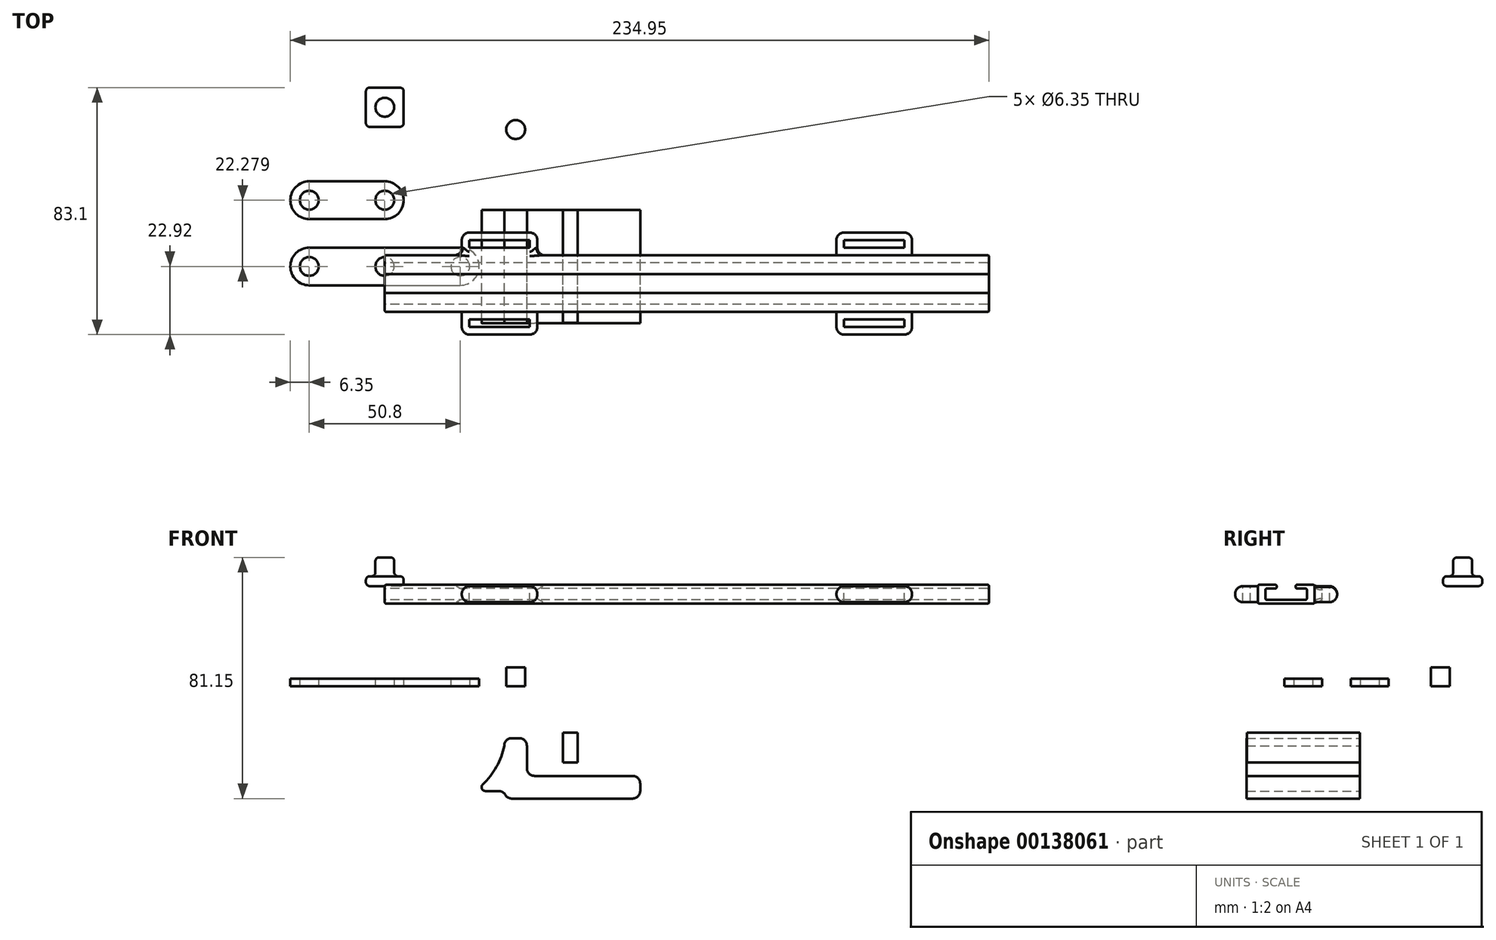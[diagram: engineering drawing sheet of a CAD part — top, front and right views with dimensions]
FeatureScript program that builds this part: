
annotation { "Feature Type Name" : "Feature", "Feature Type Description" : "" }
export const myFeature = defineFeature(function(context is Context, id is Id, definition is map)
    precondition{}
    {
        {
            var Q0;
            Q0=qCreatedBy(makeId("Top.planeOp"),FACE);
            var sketch = newSketch(context, id + "F0", { "sketchPlane" : qUnion([Q0])});
            skLineSegment(sketch, "E0.bottom", {"start": v(-25.4, 6.35) * mm, "end": v(25.4, 6.35) * mm});
            skLineSegment(sketch, "E0.top", {"start": v(-25.4, -6.35) * mm, "end": v(25.4, -6.35) * mm});
            skLineSegment(sketch, "E0.left", {"start": v(-25.4, 6.35) * mm, "end": v(-25.4, -6.35) * mm});
            skLineSegment(sketch, "E0.right", {"start": v(25.4, 6.35) * mm, "end": v(25.4, -6.35) * mm});
            skPoint(sketch, "E0.middle", {"position": v(0, 0) * mm});
            skLineSegment(sketch, "E1", {"start": v(-25.4, 0) * mm, "end": v(25.4, 0) * mm});
            skCircle(sketch, "E2", {"center": v(25.4, 0) * mm, "radius": 6.35 * mm});
            skCircle(sketch, "E3", {"center": v(25.4, 0) * mm, "radius": 3.18 * mm});
            skCircle(sketch, "E4", {"center": v(0, 0) * mm, "radius": 3.18 * mm});
            skCircle(sketch, "E5", {"center": v(-25.4, 0) * mm, "radius": 6.35 * mm});
            skCircle(sketch, "E6", {"center": v(-25.4, 0) * mm, "radius": 3.18 * mm});
            skSolve(sketch);
        }
        {
            var Q0;
            Q0 = qSketchRegion(id + "F0", true);
            extrude(context, id + "F1", {"entities" : qUnion([Q0]), "depth" : 2.54 * mm});
        }
        {
            var Q0;
            Q0=qCreatedBy(makeId("Right.planeOp"),FACE);
            var sketch = newSketch(context, id + "F2", { "sketchPlane" : qUnion([Q0])});
            skLineSegment(sketch, "E7", {"start": v(-8.95, 34.15) * mm, "end": v(-15.3, 34.15) * mm});
            skLineSegment(sketch, "E8", {"start": v(-15.3, 34.15) * mm, "end": v(-15.3, 27.8) * mm});
            skLineSegment(sketch, "E9", {"start": v(-15.3, 27.8) * mm, "end": v(3.75, 27.8) * mm});
            skLineSegment(sketch, "E10", {"start": v(3.75, 27.8) * mm, "end": v(3.75, 34.15) * mm});
            skLineSegment(sketch, "E11", {"start": v(3.75, 34.15) * mm, "end": v(-2.6, 34.15) * mm});
            skLineSegment(sketch, "E12", {"start": v(-8.95, 34.15) * mm, "end": v(-8.95, 32.88) * mm});
            skLineSegment(sketch, "E13", {"start": v(-8.95, 32.88) * mm, "end": v(-15.3, 32.88) * mm});
            skLineSegment(sketch, "E14", {"start": v(-15.3, 34.15) * mm, "end": v(-12.76, 34.15) * mm});
            skLineSegment(sketch, "E15", {"start": v(-12.76, 34.15) * mm, "end": v(-12.76, 27.8) * mm});
            skLineSegment(sketch, "E16", {"start": v(-12.76, 27.8) * mm, "end": v(-15.3, 27.8) * mm});
            skLineSegment(sketch, "E17", {"start": v(-15.3, 27.8) * mm, "end": v(-15.3, 29.07) * mm});
            skLineSegment(sketch, "E18", {"start": v(-15.3, 29.07) * mm, "end": v(3.75, 29.07) * mm});
            skLineSegment(sketch, "E19", {"start": v(3.75, 27.8) * mm, "end": v(1.21, 27.8) * mm});
            skLineSegment(sketch, "E20", {"start": v(1.21, 27.8) * mm, "end": v(1.21, 34.15) * mm});
            skLineSegment(sketch, "E21", {"start": v(1.21, 34.15) * mm, "end": v(3.75, 34.15) * mm});
            skLineSegment(sketch, "E22", {"start": v(3.75, 34.15) * mm, "end": v(3.75, 32.88) * mm});
            skLineSegment(sketch, "E23", {"start": v(3.75, 32.88) * mm, "end": v(-2.6, 32.88) * mm});
            skLineSegment(sketch, "E24", {"start": v(-2.6, 34.15) * mm, "end": v(-2.6, 32.88) * mm});
            skSolve(sketch);
        }
        {
            var Q0;
            {var subQ0=sQuery(id+"F2.wireOp",EDGE,"E21");Q0=makeQuery(id+"F2.imprint","IMPRINT",FACE,{"disambiguationData":[TD([[makeQuery(id+"F2.imprint","IMPRINT",EDGE,{"derivedFrom":subQ0}),-1.0]])]});}
            var Q1;
            {var subQ0=sQuery(id+"F2.wireOp",EDGE,"E16");Q1=makeQuery(id+"F2.imprint","IMPRINT",FACE,{"disambiguationData":[TD([[makeQuery(id+"F2.imprint","IMPRINT",EDGE,{"derivedFrom":subQ0}),-1.0]])]});}
            var Q2;
            {var subQ1=sQuery(id+"F2.wireOp",EDGE,"E10");var subQ3=sQuery(id+"F2.wireOp",EDGE,"E18");var subQ4=makeQuery(id+"F2.imprint","INTERSECT",VERTEX,{"derivedFrom":[subQ1,subQ3]});Q2=makeQuery(id+"F2.imprint","IMPRINT",FACE,{"disambiguationData":[TD([[makeQuery(id+"F2.imprint","IMPRINT",EDGE,{"disambiguationData":[TD([[subQ4,1.0]])],"derivedFrom":subQ3}),1.0]])]});}
            var Q3;
            {var subQ0=sQuery(id+"F2.wireOp",EDGE,"E19");Q3=makeQuery(id+"F2.imprint","IMPRINT",FACE,{"disambiguationData":[TD([[makeQuery(id+"F2.imprint","IMPRINT",EDGE,{"derivedFrom":subQ0}),-1.0]])]});}
            var Q4;
            {var subQ0=sQuery(id+"F2.wireOp",EDGE,"E9");Q4=makeQuery(id+"F2.imprint","IMPRINT",FACE,{"disambiguationData":[TD([[makeQuery(id+"F2.imprint","IMPRINT",EDGE,{"derivedFrom":subQ0}),1.0]])]});}
            var Q5;
            {var subQ1=sQuery(id+"F2.wireOp",EDGE,"E8");var subQ3=sQuery(id+"F2.wireOp",EDGE,"E13");var subQ4=makeQuery(id+"F2.imprint","INTERSECT",VERTEX,{"derivedFrom":[subQ1,subQ3]});Q5=makeQuery(id+"F2.imprint","IMPRINT",FACE,{"disambiguationData":[TD([[makeQuery(id+"F2.imprint","IMPRINT",EDGE,{"disambiguationData":[TD([[subQ4,1.0]])],"derivedFrom":subQ3}),1.0]])]});}
            var Q6;
            {var subQ0=sQuery(id+"F2.wireOp",EDGE,"E7");Q6=makeQuery(id+"F2.imprint","IMPRINT",FACE,{"disambiguationData":[TD([[makeQuery(id+"F2.imprint","IMPRINT",EDGE,{"derivedFrom":subQ0}),1.0]])]});}
            var Q7;
            {var subQ0=sQuery(id+"F2.wireOp",EDGE,"E14");Q7=makeQuery(id+"F2.imprint","IMPRINT",FACE,{"disambiguationData":[TD([[makeQuery(id+"F2.imprint","IMPRINT",EDGE,{"derivedFrom":subQ0}),-1.0]])]});}
            var Q8;
            {var subQ0=sQuery(id+"F2.wireOp",EDGE,"E11");Q8=makeQuery(id+"F2.imprint","IMPRINT",FACE,{"disambiguationData":[TD([[makeQuery(id+"F2.imprint","IMPRINT",EDGE,{"derivedFrom":subQ0}),1.0]])]});}
            var Q9;
            Q9 = qSketchRegion(id + "F60yiXwkqJstQ9W_2", true);
            extrude(context, id + "F3", {"entities" : qUnion([Q0, Q1, Q2, Q3, Q4, Q5, Q6, Q7, Q8, Q9]), "depth" : 203.2 * mm});
        }
        {
            var Q0;
            {var subQ0=sQuery(id+"F2.wireOp",EDGE,"E13");var subQ1=sQuery(id+"F2.wireOp",EDGE,"E12");Q0=makeQuery(id+"FPISK7QOFB9ojP9_2.opFillet","BLEND_FACE",FACE,{"disambiguationData":[OSD([subQ1,subQ0]),TDD([makeQuery(id+"F3.opExtrude","SWEPT_EDGE",EDGE,{"disambiguationData":[OSD([subQ1,subQ0])]})])]});}
            var Q1;
            {var subQ0=sQuery(id+"F2.wireOp",EDGE,"E14");Q1=makeQuery(id+"FPISK7QOFB9ojP9_2.opFillet","BLEND_EDGE",EDGE,{"blendedFrom":[makeQuery(id+"F3.opExtrude","SWEPT_EDGE",EDGE,{"disambiguationData":[OSD([sQuery(id+"F2.wireOp",EDGE,"E8"),subQ0])]}),makeQuery(id+"F3.opExtrude","SWEPT_FACE",FACE,{"disambiguationData":[OSD([sQuery(id+"F2.wireOp",EDGE,"E7"),subQ0])]})],"blendedInto":[makeQuery(id+"F3.opExtrude","SWEPT_FACE",FACE,{"disambiguationData":[OSD([sQuery(id+"F2.wireOp",EDGE,"E7"),subQ0])]})]});}
            var Q2;
            {var subQ0=sQuery(id+"F2.wireOp",EDGE,"E21");var subQ1=sQuery(id+"F2.wireOp",EDGE,"E11");Q2=makeQuery(id+"FPISK7QOFB9ojP9_2.opFillet","BLEND_FACE",FACE,{"disambiguationData":[OSD([subQ1,subQ0]),TDD([makeQuery(id+"F3.opExtrude","CAP_EDGE",EDGE,{"disambiguationData":[OSD([subQ1,subQ0])],"isStart":true})])]});}
            var Q3;
            {var subQ0=sQuery(id+"F2.wireOp",EDGE,"E12");var subQ1=sQuery(id+"F2.wireOp",EDGE,"E7");Q3=makeQuery(id+"FPISK7QOFB9ojP9_2.opFillet","BLEND_FACE",FACE,{"disambiguationData":[OSD([subQ1,subQ0]),TDD([makeQuery(id+"F3.opExtrude","SWEPT_EDGE",EDGE,{"disambiguationData":[OSD([subQ1,subQ0])]})])]});}
            var Q4;
            {var subQ0=sQuery(id+"F2.wireOp",EDGE,"E19");var subQ1=sQuery(id+"F2.wireOp",EDGE,"E16");var subQ2=sQuery(id+"F2.wireOp",EDGE,"E9");Q4=makeQuery(id+"FPISK7QOFB9ojP9_2.opFillet","BLEND_FACE",FACE,{"disambiguationData":[OSD([subQ2,subQ1,subQ0]),TDD([makeQuery(id+"F3.opExtrude","CAP_EDGE",EDGE,{"disambiguationData":[OSD([subQ2,subQ1,subQ0])],"isStart":false})])]});}
            var Q5;
            {var subQ0=sQuery(id+"F2.wireOp",EDGE,"E14");var subQ1=sQuery(id+"F2.wireOp",EDGE,"E8");Q5=makeQuery(id+"FPISK7QOFB9ojP9_2.opFillet","BLEND_FACE",FACE,{"disambiguationData":[OSD([subQ1,subQ0]),TDD([makeQuery(id+"F3.opExtrude","SWEPT_EDGE",EDGE,{"disambiguationData":[OSD([subQ1,subQ0])]})])]});}
            var Q6;
            {var subQ0=sQuery(id+"F2.wireOp",EDGE,"E13");Q6=makeQuery(id+"FPISK7QOFB9ojP9_2.opFillet","BLEND_EDGE",EDGE,{"blendedFrom":[makeQuery(id+"F3.opExtrude","SWEPT_EDGE",EDGE,{"disambiguationData":[OSD([sQuery(id+"F2.wireOp",EDGE,"E12"),subQ0])]}),makeQuery(id+"F3.opExtrude","SWEPT_FACE",FACE,{"disambiguationData":[OSD([subQ0])]})],"blendedInto":[makeQuery(id+"F3.opExtrude","SWEPT_FACE",FACE,{"disambiguationData":[OSD([subQ0])]})]});}
            var Q7;
            Q7=makeQuery(id+"F3.opExtrude","SWEPT_FACE",FACE,{"disambiguationData":[OSD([sQuery(id+"F2.wireOp",EDGE,"E11"),sQuery(id+"F2.wireOp",EDGE,"E21")])]});
            var Q8;
            {var subQ0=sQuery(id+"F2.wireOp",EDGE,"E11");Q8=makeQuery(id+"FPISK7QOFB9ojP9_2.opFillet","BLEND_EDGE",EDGE,{"blendedFrom":[makeQuery(id+"F3.opExtrude","SWEPT_EDGE",EDGE,{"disambiguationData":[OSD([subQ0,sQuery(id+"F2.wireOp",EDGE,"E24")])]}),makeQuery(id+"F3.opExtrude","SWEPT_FACE",FACE,{"disambiguationData":[OSD([subQ0,sQuery(id+"F2.wireOp",EDGE,"E21")])]})],"blendedInto":[makeQuery(id+"F3.opExtrude","SWEPT_FACE",FACE,{"disambiguationData":[OSD([subQ0,sQuery(id+"F2.wireOp",EDGE,"E21")])]})]});}
            var Q9;
            {var subQ0=sQuery(id+"F2.wireOp",EDGE,"E23");Q9=makeQuery(id+"FPISK7QOFB9ojP9_2.opFillet","BLEND_FACE",FACE,{"disambiguationData":[OSD([subQ0]),TDD([makeQuery(id+"F3.opExtrude","CAP_EDGE",EDGE,{"disambiguationData":[OSD([subQ0])],"isStart":false})])]});}
            var Q10;
            Q10=makeQuery(id+"F3.opExtrude","SWEPT_FACE",FACE,{"disambiguationData":[OSD([sQuery(id+"F2.wireOp",EDGE,"E12")])]});
            var Q11;
            {var subQ0=sQuery(id+"F2.wireOp",EDGE,"E15");Q11=makeQuery(id+"FPISK7QOFB9ojP9_2.opFillet","BLEND_FACE",FACE,{"disambiguationData":[OSD([subQ0]),TDD([makeQuery(id+"F3.opExtrude","CAP_EDGE",EDGE,{"disambiguationData":[OSD([subQ0])],"isStart":false})])]});}
            var Q12;
            {var subQ0=sQuery(id+"F2.wireOp",EDGE,"E18");Q12=makeQuery(id+"FPISK7QOFB9ojP9_2.opFillet","BLEND_EDGE",EDGE,{"blendedFrom":[makeQuery(id+"F3.opExtrude","SWEPT_EDGE",EDGE,{"disambiguationData":[OSD([sQuery(id+"F2.wireOp",EDGE,"E15"),subQ0])]}),makeQuery(id+"F3.opExtrude","SWEPT_FACE",FACE,{"disambiguationData":[OSD([subQ0])]})],"blendedInto":[makeQuery(id+"F3.opExtrude","SWEPT_FACE",FACE,{"disambiguationData":[OSD([subQ0])]})]});}
            var Q13;
            Q13=makeQuery(id+"F3.opExtrude","SWEPT_FACE",FACE,{"disambiguationData":[OSD([sQuery(id+"F2.wireOp",EDGE,"E18")])]});
            var Q14;
            {var subQ0=sQuery(id+"F2.wireOp",EDGE,"E24");var subQ1=sQuery(id+"F2.wireOp",EDGE,"E23");Q14=makeQuery(id+"FPISK7QOFB9ojP9_2.opFillet","BLEND_FACE",FACE,{"disambiguationData":[OSD([subQ1,subQ0]),TDD([makeQuery(id+"F3.opExtrude","CAP_VERTEX",VERTEX,{"disambiguationData":[OSD([subQ1,subQ0])],"isStart":false})])]});}
            var Q15;
            {var subQ0=sQuery(id+"F2.wireOp",EDGE,"E22");var subQ1=sQuery(id+"F2.wireOp",EDGE,"E10");Q15=makeQuery(id+"FPISK7QOFB9ojP9_2.opFillet","BLEND_FACE",FACE,{"disambiguationData":[OSD([subQ1,subQ0]),TDD([makeQuery(id+"F3.opExtrude","CAP_EDGE",EDGE,{"disambiguationData":[OSD([subQ1,subQ0])],"isStart":true})])]});}
            var Q16;
            {var subQ0=sQuery(id+"F2.wireOp",EDGE,"E19");var subQ1=sQuery(id+"F2.wireOp",EDGE,"E10");Q16=makeQuery(id+"FPISK7QOFB9ojP9_2.opFillet","BLEND_FACE",FACE,{"disambiguationData":[OSD([subQ1,subQ0]),TDD([makeQuery(id+"F3.opExtrude","SWEPT_EDGE",EDGE,{"disambiguationData":[OSD([subQ1,subQ0])]})])]});}
            var Q17;
            {var subQ0=sQuery(id+"F2.wireOp",EDGE,"E7");Q17=makeQuery(id+"FPISK7QOFB9ojP9_2.opFillet","BLEND_EDGE",EDGE,{"blendedFrom":[makeQuery(id+"F3.opExtrude","SWEPT_EDGE",EDGE,{"disambiguationData":[OSD([subQ0,sQuery(id+"F2.wireOp",EDGE,"E12")])]}),makeQuery(id+"F3.opExtrude","SWEPT_FACE",FACE,{"disambiguationData":[OSD([subQ0,sQuery(id+"F2.wireOp",EDGE,"E14")])]})],"blendedInto":[makeQuery(id+"F3.opExtrude","SWEPT_FACE",FACE,{"disambiguationData":[OSD([subQ0,sQuery(id+"F2.wireOp",EDGE,"E14")])]})]});}
            var Q18;
            {var subQ0=sQuery(id+"F2.wireOp",EDGE,"E14");var subQ1=sQuery(id+"F2.wireOp",EDGE,"E8");Q18=makeQuery(id+"FPISK7QOFB9ojP9_2.opFillet","BLEND_FACE",FACE,{"disambiguationData":[OSD([subQ1,subQ0]),TDD([makeQuery(id+"F3.opExtrude","CAP_VERTEX",VERTEX,{"disambiguationData":[OSD([subQ1,subQ0])],"isStart":false})])]});}
            var Q19;
            Q19=makeQuery(id+"F3.opExtrude","SWEPT_FACE",FACE,{"disambiguationData":[OSD([sQuery(id+"F2.wireOp",EDGE,"E13")])]});
            var Q20;
            Q20=makeQuery(id+"F3.opExtrude","CAP_FACE",FACE,{"disambiguationData":[OSD([sQuery(id+"F2.wireOp",EDGE,"E7"),sQuery(id+"F2.wireOp",EDGE,"E8"),sQuery(id+"F2.wireOp",EDGE,"E9"),sQuery(id+"F2.wireOp",EDGE,"E10"),sQuery(id+"F2.wireOp",EDGE,"E11"),sQuery(id+"F2.wireOp",EDGE,"E12"),sQuery(id+"F2.wireOp",EDGE,"E13"),sQuery(id+"F2.wireOp",EDGE,"E14"),sQuery(id+"F2.wireOp",EDGE,"E15"),sQuery(id+"F2.wireOp",EDGE,"E16"),sQuery(id+"F2.wireOp",EDGE,"E17"),sQuery(id+"F2.wireOp",EDGE,"E18"),sQuery(id+"F2.wireOp",EDGE,"E19"),sQuery(id+"F2.wireOp",EDGE,"E20"),sQuery(id+"F2.wireOp",EDGE,"E21"),sQuery(id+"F2.wireOp",EDGE,"E22"),sQuery(id+"F2.wireOp",EDGE,"E23"),sQuery(id+"F2.wireOp",EDGE,"E24")])],"isStart":false});
            var Q21;
            {var subQ0=sQuery(id+"F2.wireOp",EDGE,"E18");Q21=makeQuery(id+"FPISK7QOFB9ojP9_2.opFillet","BLEND_FACE",FACE,{"disambiguationData":[OSD([subQ0]),TDD([makeQuery(id+"F3.opExtrude","CAP_EDGE",EDGE,{"disambiguationData":[OSD([subQ0])],"isStart":true})])]});}
            var Q22;
            {var subQ0=sQuery(id+"F2.wireOp",EDGE,"E21");var subQ1=sQuery(id+"F2.wireOp",EDGE,"E11");Q22=makeQuery(id+"FPISK7QOFB9ojP9_2.opFillet","BLEND_FACE",FACE,{"disambiguationData":[OSD([subQ1,subQ0]),TDD([makeQuery(id+"F3.opExtrude","CAP_EDGE",EDGE,{"disambiguationData":[OSD([subQ1,subQ0])],"isStart":false})])]});}
            var Q23;
            {var subQ0=sQuery(id+"F2.wireOp",EDGE,"E14");var subQ1=sQuery(id+"F2.wireOp",EDGE,"E7");Q23=makeQuery(id+"FPISK7QOFB9ojP9_2.opFillet","BLEND_FACE",FACE,{"disambiguationData":[OSD([subQ1,subQ0]),TDD([makeQuery(id+"F3.opExtrude","CAP_EDGE",EDGE,{"disambiguationData":[OSD([subQ1,subQ0])],"isStart":true})])]});}
            var Q24;
            {var subQ0=sQuery(id+"F2.wireOp",EDGE,"E19");var subQ1=sQuery(id+"F2.wireOp",EDGE,"E10");Q24=makeQuery(id+"FPISK7QOFB9ojP9_2.opFillet","BLEND_FACE",FACE,{"disambiguationData":[OSD([subQ1,subQ0]),TDD([makeQuery(id+"F3.opExtrude","CAP_VERTEX",VERTEX,{"disambiguationData":[OSD([subQ1,subQ0])],"isStart":false})])]});}
            var Q25;
            {var subQ0=sQuery(id+"F2.wireOp",EDGE,"E24");var subQ1=sQuery(id+"F2.wireOp",EDGE,"E11");Q25=makeQuery(id+"FPISK7QOFB9ojP9_2.opFillet","BLEND_FACE",FACE,{"disambiguationData":[OSD([subQ1,subQ0]),TDD([makeQuery(id+"F3.opExtrude","CAP_VERTEX",VERTEX,{"disambiguationData":[OSD([subQ1,subQ0])],"isStart":true})])]});}
            var Q26;
            {var subQ0=sQuery(id+"F2.wireOp",EDGE,"E17");var subQ1=sQuery(id+"F2.wireOp",EDGE,"E16");Q26=makeQuery(id+"FPISK7QOFB9ojP9_2.opFillet","BLEND_FACE",FACE,{"disambiguationData":[OSD([subQ1,subQ0]),TDD([makeQuery(id+"F3.opExtrude","CAP_VERTEX",VERTEX,{"disambiguationData":[OSD([subQ1,subQ0])],"isStart":false})])]});}
            var Q27;
            {var subQ0=sQuery(id+"F2.wireOp",EDGE,"E21");Q27=makeQuery(id+"FPISK7QOFB9ojP9_2.opFillet","BLEND_EDGE",EDGE,{"blendedFrom":[makeQuery(id+"F3.opExtrude","SWEPT_EDGE",EDGE,{"disambiguationData":[OSD([subQ0,sQuery(id+"F2.wireOp",EDGE,"E22")])]}),makeQuery(id+"F3.opExtrude","SWEPT_FACE",FACE,{"disambiguationData":[OSD([sQuery(id+"F2.wireOp",EDGE,"E11"),subQ0])]})],"blendedInto":[makeQuery(id+"F3.opExtrude","SWEPT_FACE",FACE,{"disambiguationData":[OSD([sQuery(id+"F2.wireOp",EDGE,"E11"),subQ0])]})]});}
            var Q28;
            Q28=makeQuery(id+"F3.opExtrude","SWEPT_FACE",FACE,{"disambiguationData":[OSD([sQuery(id+"F2.wireOp",EDGE,"E20")])]});
            var Q29;
            {var subQ0=sQuery(id+"F2.wireOp",EDGE,"E20");Q29=makeQuery(id+"FPISK7QOFB9ojP9_2.opFillet","BLEND_FACE",FACE,{"disambiguationData":[OSD([subQ0]),TDD([makeQuery(id+"F3.opExtrude","CAP_EDGE",EDGE,{"disambiguationData":[OSD([subQ0])],"isStart":false})])]});}
            var Q30;
            {var subQ0=sQuery(id+"F2.wireOp",EDGE,"E22");var subQ1=sQuery(id+"F2.wireOp",EDGE,"E10");Q30=makeQuery(id+"FPISK7QOFB9ojP9_2.opFillet","BLEND_FACE",FACE,{"disambiguationData":[OSD([subQ1,subQ0]),TDD([makeQuery(id+"F3.opExtrude","CAP_EDGE",EDGE,{"disambiguationData":[OSD([subQ1,subQ0])],"isStart":false})])]});}
            var Q31;
            {var subQ0=sQuery(id+"F2.wireOp",EDGE,"E24");var subQ1=sQuery(id+"F2.wireOp",EDGE,"E11");Q31=makeQuery(id+"FPISK7QOFB9ojP9_2.opFillet","BLEND_FACE",FACE,{"disambiguationData":[OSD([subQ1,subQ0]),TDD([makeQuery(id+"F3.opExtrude","SWEPT_EDGE",EDGE,{"disambiguationData":[OSD([subQ1,subQ0])]})])]});}
            var Q32;
            {var subQ0=sQuery(id+"F2.wireOp",EDGE,"E17");var subQ1=sQuery(id+"F2.wireOp",EDGE,"E8");Q32=makeQuery(id+"FPISK7QOFB9ojP9_2.opFillet","BLEND_FACE",FACE,{"disambiguationData":[OSD([subQ1,subQ0]),TDD([makeQuery(id+"F3.opExtrude","CAP_EDGE",EDGE,{"disambiguationData":[OSD([subQ1,subQ0])],"isStart":false})])]});}
            var Q33;
            {var subQ0=sQuery(id+"F2.wireOp",EDGE,"E12");Q33=makeQuery(id+"FPISK7QOFB9ojP9_2.opFillet","BLEND_EDGE",EDGE,{"blendedFrom":[makeQuery(id+"F3.opExtrude","SWEPT_EDGE",EDGE,{"disambiguationData":[OSD([sQuery(id+"F2.wireOp",EDGE,"E7"),subQ0])]}),makeQuery(id+"F3.opExtrude","SWEPT_FACE",FACE,{"disambiguationData":[OSD([subQ0])]})],"blendedInto":[makeQuery(id+"F3.opExtrude","SWEPT_FACE",FACE,{"disambiguationData":[OSD([subQ0])]})]});}
            var Q34;
            {var subQ0=sQuery(id+"F2.wireOp",EDGE,"E22");Q34=makeQuery(id+"FPISK7QOFB9ojP9_2.opFillet","BLEND_EDGE",EDGE,{"blendedFrom":[makeQuery(id+"F3.opExtrude","SWEPT_EDGE",EDGE,{"disambiguationData":[OSD([sQuery(id+"F2.wireOp",EDGE,"E21"),subQ0])]}),makeQuery(id+"F3.opExtrude","SWEPT_FACE",FACE,{"disambiguationData":[OSD([sQuery(id+"F2.wireOp",EDGE,"E10"),subQ0])]})],"blendedInto":[makeQuery(id+"F3.opExtrude","SWEPT_FACE",FACE,{"disambiguationData":[OSD([sQuery(id+"F2.wireOp",EDGE,"E10"),subQ0])]})]});}
            var Q35;
            Q35=makeQuery(id+"F3.opExtrude","SWEPT_FACE",FACE,{"disambiguationData":[OSD([sQuery(id+"F2.wireOp",EDGE,"E15")])]});
            var Q36;
            Q36=makeQuery(id+"F3.opExtrude","SWEPT_FACE",FACE,{"disambiguationData":[OSD([sQuery(id+"F2.wireOp",EDGE,"E7"),sQuery(id+"F2.wireOp",EDGE,"E14")])]});
            var Q37;
            {var subQ0=sQuery(id+"F2.wireOp",EDGE,"E18");Q37=makeQuery(id+"FPISK7QOFB9ojP9_2.opFillet","BLEND_FACE",FACE,{"disambiguationData":[OSD([subQ0]),TDD([makeQuery(id+"F3.opExtrude","CAP_EDGE",EDGE,{"disambiguationData":[OSD([subQ0])],"isStart":false})])]});}
            var Q38;
            {var subQ0=sQuery(id+"F2.wireOp",EDGE,"E22");var subQ1=sQuery(id+"F2.wireOp",EDGE,"E21");Q38=makeQuery(id+"FPISK7QOFB9ojP9_2.opFillet","BLEND_FACE",FACE,{"disambiguationData":[OSD([subQ1,subQ0]),TDD([makeQuery(id+"F3.opExtrude","SWEPT_EDGE",EDGE,{"disambiguationData":[OSD([subQ1,subQ0])]})])]});}
            var Q39;
            {var subQ0=sQuery(id+"F2.wireOp",EDGE,"E14");var subQ1=sQuery(id+"F2.wireOp",EDGE,"E7");Q39=makeQuery(id+"FPISK7QOFB9ojP9_2.opFillet","BLEND_FACE",FACE,{"disambiguationData":[OSD([subQ1,subQ0]),TDD([makeQuery(id+"F3.opExtrude","CAP_EDGE",EDGE,{"disambiguationData":[OSD([subQ1,subQ0])],"isStart":false})])]});}
            var Q40;
            {var subQ0=sQuery(id+"F2.wireOp",EDGE,"E12");Q40=makeQuery(id+"FPISK7QOFB9ojP9_2.opFillet","BLEND_EDGE",EDGE,{"blendedFrom":[makeQuery(id+"F3.opExtrude","SWEPT_EDGE",EDGE,{"disambiguationData":[OSD([subQ0,sQuery(id+"F2.wireOp",EDGE,"E13")])]}),makeQuery(id+"F3.opExtrude","SWEPT_FACE",FACE,{"disambiguationData":[OSD([subQ0])]})],"blendedInto":[makeQuery(id+"F3.opExtrude","SWEPT_FACE",FACE,{"disambiguationData":[OSD([subQ0])]})]});}
            var Q41;
            Q41=makeQuery(id+"F3.opExtrude","SWEPT_FACE",FACE,{"disambiguationData":[OSD([sQuery(id+"F2.wireOp",EDGE,"E10"),sQuery(id+"F2.wireOp",EDGE,"E22")])]});
            var Q42;
            {var subQ0=sQuery(id+"F2.wireOp",EDGE,"E13");Q42=makeQuery(id+"FPISK7QOFB9ojP9_2.opFillet","BLEND_FACE",FACE,{"disambiguationData":[OSD([subQ0]),TDD([makeQuery(id+"F3.opExtrude","CAP_EDGE",EDGE,{"disambiguationData":[OSD([subQ0])],"isStart":false})])]});}
            var Q43;
            {var subQ0=sQuery(id+"F2.wireOp",EDGE,"E18");var subQ1=sQuery(id+"F2.wireOp",EDGE,"E15");Q43=makeQuery(id+"FPISK7QOFB9ojP9_2.opFillet","BLEND_FACE",FACE,{"disambiguationData":[OSD([subQ1,subQ0]),TDD([makeQuery(id+"F3.opExtrude","SWEPT_EDGE",EDGE,{"disambiguationData":[OSD([subQ1,subQ0])]})])]});}
            var Q44;
            {var subQ0=sQuery(id+"F2.wireOp",EDGE,"E10");Q44=makeQuery(id+"FPISK7QOFB9ojP9_2.opFillet","BLEND_EDGE",EDGE,{"blendedFrom":[makeQuery(id+"F3.opExtrude","SWEPT_EDGE",EDGE,{"disambiguationData":[OSD([subQ0,sQuery(id+"F2.wireOp",EDGE,"E19")])]}),makeQuery(id+"F3.opExtrude","SWEPT_FACE",FACE,{"disambiguationData":[OSD([subQ0,sQuery(id+"F2.wireOp",EDGE,"E22")])]})],"blendedInto":[makeQuery(id+"F3.opExtrude","SWEPT_FACE",FACE,{"disambiguationData":[OSD([subQ0,sQuery(id+"F2.wireOp",EDGE,"E22")])]})]});}
            var Q45;
            {var subQ0=sQuery(id+"F2.wireOp",EDGE,"E19");var subQ1=sQuery(id+"F2.wireOp",EDGE,"E16");var subQ2=sQuery(id+"F2.wireOp",EDGE,"E9");Q45=makeQuery(id+"FPISK7QOFB9ojP9_2.opFillet","BLEND_FACE",FACE,{"disambiguationData":[OSD([subQ2,subQ1,subQ0]),TDD([makeQuery(id+"F3.opExtrude","CAP_EDGE",EDGE,{"disambiguationData":[OSD([subQ2,subQ1,subQ0])],"isStart":true})])]});}
            var Q46;
            Q46=makeQuery(id+"F3.opExtrude","SWEPT_FACE",FACE,{"disambiguationData":[OSD([sQuery(id+"F2.wireOp",EDGE,"E23")])]});
            var Q47;
            {var subQ0=sQuery(id+"F2.wireOp",EDGE,"E20");var subQ1=sQuery(id+"F2.wireOp",EDGE,"E18");Q47=makeQuery(id+"FPISK7QOFB9ojP9_2.opFillet","BLEND_FACE",FACE,{"disambiguationData":[OSD([subQ1,subQ0]),TDD([makeQuery(id+"F3.opExtrude","SWEPT_EDGE",EDGE,{"disambiguationData":[OSD([subQ1,subQ0])]})])]});}
            var Q48;
            {var subQ0=sQuery(id+"F2.wireOp",EDGE,"E12");Q48=makeQuery(id+"FPISK7QOFB9ojP9_2.opFillet","BLEND_FACE",FACE,{"disambiguationData":[OSD([subQ0]),TDD([makeQuery(id+"F3.opExtrude","CAP_EDGE",EDGE,{"disambiguationData":[OSD([subQ0])],"isStart":false})])]});}
            var Q49;
            {var subQ0=sQuery(id+"F2.wireOp",EDGE,"E23");Q49=makeQuery(id+"FPISK7QOFB9ojP9_2.opFillet","BLEND_FACE",FACE,{"disambiguationData":[OSD([subQ0]),TDD([makeQuery(id+"F3.opExtrude","CAP_EDGE",EDGE,{"disambiguationData":[OSD([subQ0])],"isStart":true})])]});}
            var Q50;
            {var subQ0=sQuery(id+"F2.wireOp",EDGE,"E14");var subQ1=sQuery(id+"F2.wireOp",EDGE,"E7");Q50=makeQuery(id+"FPISK7QOFB9ojP9_2.opFillet","BLEND_EDGE",EDGE,{"blendedFrom":[makeQuery(id+"F3.opExtrude","CAP_EDGE",EDGE,{"disambiguationData":[OSD([subQ1,subQ0])],"isStart":true}),makeQuery(id+"F3.opExtrude","CAP_FACE",FACE,{"disambiguationData":[OSD([subQ1,sQuery(id+"F2.wireOp",EDGE,"E8"),sQuery(id+"F2.wireOp",EDGE,"E9"),sQuery(id+"F2.wireOp",EDGE,"E10"),sQuery(id+"F2.wireOp",EDGE,"E11"),sQuery(id+"F2.wireOp",EDGE,"E12"),sQuery(id+"F2.wireOp",EDGE,"E13"),subQ0,sQuery(id+"F2.wireOp",EDGE,"E15"),sQuery(id+"F2.wireOp",EDGE,"E16"),sQuery(id+"F2.wireOp",EDGE,"E17"),sQuery(id+"F2.wireOp",EDGE,"E18"),sQuery(id+"F2.wireOp",EDGE,"E19"),sQuery(id+"F2.wireOp",EDGE,"E20"),sQuery(id+"F2.wireOp",EDGE,"E21"),sQuery(id+"F2.wireOp",EDGE,"E22"),sQuery(id+"F2.wireOp",EDGE,"E23"),sQuery(id+"F2.wireOp",EDGE,"E24")])],"isStart":true})],"blendedInto":[makeQuery(id+"F3.opExtrude","CAP_FACE",FACE,{"disambiguationData":[OSD([subQ1,sQuery(id+"F2.wireOp",EDGE,"E8"),sQuery(id+"F2.wireOp",EDGE,"E9"),sQuery(id+"F2.wireOp",EDGE,"E10"),sQuery(id+"F2.wireOp",EDGE,"E11"),sQuery(id+"F2.wireOp",EDGE,"E12"),sQuery(id+"F2.wireOp",EDGE,"E13"),subQ0,sQuery(id+"F2.wireOp",EDGE,"E15"),sQuery(id+"F2.wireOp",EDGE,"E16"),sQuery(id+"F2.wireOp",EDGE,"E17"),sQuery(id+"F2.wireOp",EDGE,"E18"),sQuery(id+"F2.wireOp",EDGE,"E19"),sQuery(id+"F2.wireOp",EDGE,"E20"),sQuery(id+"F2.wireOp",EDGE,"E21"),sQuery(id+"F2.wireOp",EDGE,"E22"),sQuery(id+"F2.wireOp",EDGE,"E23"),sQuery(id+"F2.wireOp",EDGE,"E24")])],"isStart":true})]});}
            var Q51;
            Q51=makeQuery(id+"F3.opExtrude","CAP_FACE",FACE,{"disambiguationData":[OSD([sQuery(id+"F2.wireOp",EDGE,"E7"),sQuery(id+"F2.wireOp",EDGE,"E8"),sQuery(id+"F2.wireOp",EDGE,"E9"),sQuery(id+"F2.wireOp",EDGE,"E10"),sQuery(id+"F2.wireOp",EDGE,"E11"),sQuery(id+"F2.wireOp",EDGE,"E12"),sQuery(id+"F2.wireOp",EDGE,"E13"),sQuery(id+"F2.wireOp",EDGE,"E14"),sQuery(id+"F2.wireOp",EDGE,"E15"),sQuery(id+"F2.wireOp",EDGE,"E16"),sQuery(id+"F2.wireOp",EDGE,"E17"),sQuery(id+"F2.wireOp",EDGE,"E18"),sQuery(id+"F2.wireOp",EDGE,"E19"),sQuery(id+"F2.wireOp",EDGE,"E20"),sQuery(id+"F2.wireOp",EDGE,"E21"),sQuery(id+"F2.wireOp",EDGE,"E22"),sQuery(id+"F2.wireOp",EDGE,"E23"),sQuery(id+"F2.wireOp",EDGE,"E24")])],"isStart":true});
            var Q52;
            Q52=makeQuery(id+"F3.opExtrude","SWEPT_FACE",FACE,{"disambiguationData":[OSD([sQuery(id+"F2.wireOp",EDGE,"E8"),sQuery(id+"F2.wireOp",EDGE,"E17")])]});
            var Q53;
            {var subQ0=sQuery(id+"F2.wireOp",EDGE,"E23");Q53=makeQuery(id+"FPISK7QOFB9ojP9_2.opFillet","BLEND_EDGE",EDGE,{"blendedFrom":[makeQuery(id+"F3.opExtrude","CAP_EDGE",EDGE,{"disambiguationData":[OSD([subQ0])],"isStart":false}),makeQuery(id+"F3.opExtrude","CAP_FACE",FACE,{"disambiguationData":[OSD([sQuery(id+"F2.wireOp",EDGE,"E7"),sQuery(id+"F2.wireOp",EDGE,"E8"),sQuery(id+"F2.wireOp",EDGE,"E9"),sQuery(id+"F2.wireOp",EDGE,"E10"),sQuery(id+"F2.wireOp",EDGE,"E11"),sQuery(id+"F2.wireOp",EDGE,"E12"),sQuery(id+"F2.wireOp",EDGE,"E13"),sQuery(id+"F2.wireOp",EDGE,"E14"),sQuery(id+"F2.wireOp",EDGE,"E15"),sQuery(id+"F2.wireOp",EDGE,"E16"),sQuery(id+"F2.wireOp",EDGE,"E17"),sQuery(id+"F2.wireOp",EDGE,"E18"),sQuery(id+"F2.wireOp",EDGE,"E19"),sQuery(id+"F2.wireOp",EDGE,"E20"),sQuery(id+"F2.wireOp",EDGE,"E21"),sQuery(id+"F2.wireOp",EDGE,"E22"),subQ0,sQuery(id+"F2.wireOp",EDGE,"E24")])],"isStart":false})],"blendedInto":[makeQuery(id+"F3.opExtrude","CAP_FACE",FACE,{"disambiguationData":[OSD([sQuery(id+"F2.wireOp",EDGE,"E7"),sQuery(id+"F2.wireOp",EDGE,"E8"),sQuery(id+"F2.wireOp",EDGE,"E9"),sQuery(id+"F2.wireOp",EDGE,"E10"),sQuery(id+"F2.wireOp",EDGE,"E11"),sQuery(id+"F2.wireOp",EDGE,"E12"),sQuery(id+"F2.wireOp",EDGE,"E13"),sQuery(id+"F2.wireOp",EDGE,"E14"),sQuery(id+"F2.wireOp",EDGE,"E15"),sQuery(id+"F2.wireOp",EDGE,"E16"),sQuery(id+"F2.wireOp",EDGE,"E17"),sQuery(id+"F2.wireOp",EDGE,"E18"),sQuery(id+"F2.wireOp",EDGE,"E19"),sQuery(id+"F2.wireOp",EDGE,"E20"),sQuery(id+"F2.wireOp",EDGE,"E21"),sQuery(id+"F2.wireOp",EDGE,"E22"),subQ0,sQuery(id+"F2.wireOp",EDGE,"E24")])],"isStart":false})]});}
            var Q54;
            Q54=makeQuery(id+"F3.opExtrude","SWEPT_FACE",FACE,{"disambiguationData":[OSD([sQuery(id+"F2.wireOp",EDGE,"E24")])]});
            var Q55;
            {var subQ0=sQuery(id+"F2.wireOp",EDGE,"E15");Q55=makeQuery(id+"FPISK7QOFB9ojP9_2.opFillet","BLEND_FACE",FACE,{"disambiguationData":[OSD([subQ0]),TDD([makeQuery(id+"F3.opExtrude","CAP_EDGE",EDGE,{"disambiguationData":[OSD([subQ0])],"isStart":true})])]});}
            var Q56;
            {var subQ0=sQuery(id+"F2.wireOp",EDGE,"E13");Q56=makeQuery(id+"FPISK7QOFB9ojP9_2.opFillet","BLEND_EDGE",EDGE,{"blendedFrom":[makeQuery(id+"F3.opExtrude","CAP_EDGE",EDGE,{"disambiguationData":[OSD([subQ0])],"isStart":false}),makeQuery(id+"F3.opExtrude","CAP_FACE",FACE,{"disambiguationData":[OSD([sQuery(id+"F2.wireOp",EDGE,"E7"),sQuery(id+"F2.wireOp",EDGE,"E8"),sQuery(id+"F2.wireOp",EDGE,"E9"),sQuery(id+"F2.wireOp",EDGE,"E10"),sQuery(id+"F2.wireOp",EDGE,"E11"),sQuery(id+"F2.wireOp",EDGE,"E12"),subQ0,sQuery(id+"F2.wireOp",EDGE,"E14"),sQuery(id+"F2.wireOp",EDGE,"E15"),sQuery(id+"F2.wireOp",EDGE,"E16"),sQuery(id+"F2.wireOp",EDGE,"E17"),sQuery(id+"F2.wireOp",EDGE,"E18"),sQuery(id+"F2.wireOp",EDGE,"E19"),sQuery(id+"F2.wireOp",EDGE,"E20"),sQuery(id+"F2.wireOp",EDGE,"E21"),sQuery(id+"F2.wireOp",EDGE,"E22"),sQuery(id+"F2.wireOp",EDGE,"E23"),sQuery(id+"F2.wireOp",EDGE,"E24")])],"isStart":false})],"blendedInto":[makeQuery(id+"F3.opExtrude","CAP_FACE",FACE,{"disambiguationData":[OSD([sQuery(id+"F2.wireOp",EDGE,"E7"),sQuery(id+"F2.wireOp",EDGE,"E8"),sQuery(id+"F2.wireOp",EDGE,"E9"),sQuery(id+"F2.wireOp",EDGE,"E10"),sQuery(id+"F2.wireOp",EDGE,"E11"),sQuery(id+"F2.wireOp",EDGE,"E12"),subQ0,sQuery(id+"F2.wireOp",EDGE,"E14"),sQuery(id+"F2.wireOp",EDGE,"E15"),sQuery(id+"F2.wireOp",EDGE,"E16"),sQuery(id+"F2.wireOp",EDGE,"E17"),sQuery(id+"F2.wireOp",EDGE,"E18"),sQuery(id+"F2.wireOp",EDGE,"E19"),sQuery(id+"F2.wireOp",EDGE,"E20"),sQuery(id+"F2.wireOp",EDGE,"E21"),sQuery(id+"F2.wireOp",EDGE,"E22"),sQuery(id+"F2.wireOp",EDGE,"E23"),sQuery(id+"F2.wireOp",EDGE,"E24")])],"isStart":false})]});}
            var Q57;
            {var subQ0=sQuery(id+"F2.wireOp",EDGE,"E24");var subQ1=sQuery(id+"F2.wireOp",EDGE,"E23");Q57=makeQuery(id+"FPISK7QOFB9ojP9_2.opFillet","BLEND_FACE",FACE,{"disambiguationData":[OSD([subQ1,subQ0]),TDD([makeQuery(id+"F3.opExtrude","SWEPT_EDGE",EDGE,{"disambiguationData":[OSD([subQ1,subQ0])]})])]});}
            var Q58;
            {var subQ0=sQuery(id+"F2.wireOp",EDGE,"E18");Q58=makeQuery(id+"FPISK7QOFB9ojP9_2.opFillet","BLEND_EDGE",EDGE,{"blendedFrom":[makeQuery(id+"F3.opExtrude","CAP_EDGE",EDGE,{"disambiguationData":[OSD([subQ0])],"isStart":true}),makeQuery(id+"F3.opExtrude","SWEPT_FACE",FACE,{"disambiguationData":[OSD([subQ0])]})],"blendedInto":[makeQuery(id+"F3.opExtrude","SWEPT_FACE",FACE,{"disambiguationData":[OSD([subQ0])]})]});}
            var Q59;
            {var subQ0=sQuery(id+"F2.wireOp",EDGE,"E15");Q59=makeQuery(id+"FPISK7QOFB9ojP9_2.opFillet","BLEND_EDGE",EDGE,{"blendedFrom":[makeQuery(id+"F3.opExtrude","SWEPT_EDGE",EDGE,{"disambiguationData":[OSD([subQ0,sQuery(id+"F2.wireOp",EDGE,"E18")])]}),makeQuery(id+"F3.opExtrude","SWEPT_FACE",FACE,{"disambiguationData":[OSD([subQ0])]})],"blendedInto":[makeQuery(id+"F3.opExtrude","SWEPT_FACE",FACE,{"disambiguationData":[OSD([subQ0])]})]});}
            var Q60;
            {var subQ0=sQuery(id+"F2.wireOp",EDGE,"E18");var subQ1=sQuery(id+"F2.wireOp",EDGE,"E15");Q60=makeQuery(id+"FPISK7QOFB9ojP9_2.opFillet","BLEND_FACE",FACE,{"disambiguationData":[OSD([subQ1,subQ0]),TDD([makeQuery(id+"F3.opExtrude","CAP_VERTEX",VERTEX,{"disambiguationData":[OSD([subQ1,subQ0])],"isStart":true})])]});}
            var Q61;
            {var subQ0=sQuery(id+"F2.wireOp",EDGE,"E21");var subQ1=sQuery(id+"F2.wireOp",EDGE,"E11");Q61=makeQuery(id+"FPISK7QOFB9ojP9_2.opFillet","BLEND_EDGE",EDGE,{"blendedFrom":[makeQuery(id+"F3.opExtrude","CAP_EDGE",EDGE,{"disambiguationData":[OSD([subQ1,subQ0])],"isStart":true}),makeQuery(id+"F3.opExtrude","SWEPT_FACE",FACE,{"disambiguationData":[OSD([subQ1,subQ0])]})],"blendedInto":[makeQuery(id+"F3.opExtrude","SWEPT_FACE",FACE,{"disambiguationData":[OSD([subQ1,subQ0])]})]});}
            var Q62;
            {var subQ0=sQuery(id+"F2.wireOp",EDGE,"E14");var subQ1=sQuery(id+"F2.wireOp",EDGE,"E7");Q62=makeQuery(id+"FPISK7QOFB9ojP9_2.opFillet","BLEND_EDGE",EDGE,{"blendedFrom":[makeQuery(id+"F3.opExtrude","CAP_EDGE",EDGE,{"disambiguationData":[OSD([subQ1,subQ0])],"isStart":true}),makeQuery(id+"F3.opExtrude","SWEPT_FACE",FACE,{"disambiguationData":[OSD([subQ1,subQ0])]})],"blendedInto":[makeQuery(id+"F3.opExtrude","SWEPT_FACE",FACE,{"disambiguationData":[OSD([subQ1,subQ0])]})]});}
            var Q63;
            {var subQ0=sQuery(id+"F2.wireOp",EDGE,"E19");var subQ1=sQuery(id+"F2.wireOp",EDGE,"E16");var subQ2=sQuery(id+"F2.wireOp",EDGE,"E9");Q63=makeQuery(id+"FPISK7QOFB9ojP9_2.opFillet","BLEND_EDGE",EDGE,{"blendedFrom":[makeQuery(id+"F3.opExtrude","CAP_EDGE",EDGE,{"disambiguationData":[OSD([subQ2,subQ1,subQ0])],"isStart":false}),makeQuery(id+"F3.opExtrude","CAP_FACE",FACE,{"disambiguationData":[OSD([sQuery(id+"F2.wireOp",EDGE,"E7"),sQuery(id+"F2.wireOp",EDGE,"E8"),subQ2,sQuery(id+"F2.wireOp",EDGE,"E10"),sQuery(id+"F2.wireOp",EDGE,"E11"),sQuery(id+"F2.wireOp",EDGE,"E12"),sQuery(id+"F2.wireOp",EDGE,"E13"),sQuery(id+"F2.wireOp",EDGE,"E14"),sQuery(id+"F2.wireOp",EDGE,"E15"),subQ1,sQuery(id+"F2.wireOp",EDGE,"E17"),sQuery(id+"F2.wireOp",EDGE,"E18"),subQ0,sQuery(id+"F2.wireOp",EDGE,"E20"),sQuery(id+"F2.wireOp",EDGE,"E21"),sQuery(id+"F2.wireOp",EDGE,"E22"),sQuery(id+"F2.wireOp",EDGE,"E23"),sQuery(id+"F2.wireOp",EDGE,"E24")])],"isStart":false})],"blendedInto":[makeQuery(id+"F3.opExtrude","CAP_FACE",FACE,{"disambiguationData":[OSD([sQuery(id+"F2.wireOp",EDGE,"E7"),sQuery(id+"F2.wireOp",EDGE,"E8"),subQ2,sQuery(id+"F2.wireOp",EDGE,"E10"),sQuery(id+"F2.wireOp",EDGE,"E11"),sQuery(id+"F2.wireOp",EDGE,"E12"),sQuery(id+"F2.wireOp",EDGE,"E13"),sQuery(id+"F2.wireOp",EDGE,"E14"),sQuery(id+"F2.wireOp",EDGE,"E15"),subQ1,sQuery(id+"F2.wireOp",EDGE,"E17"),sQuery(id+"F2.wireOp",EDGE,"E18"),subQ0,sQuery(id+"F2.wireOp",EDGE,"E20"),sQuery(id+"F2.wireOp",EDGE,"E21"),sQuery(id+"F2.wireOp",EDGE,"E22"),sQuery(id+"F2.wireOp",EDGE,"E23"),sQuery(id+"F2.wireOp",EDGE,"E24")])],"isStart":false})]});}
            var Q64;
            {var subQ0=sQuery(id+"F2.wireOp",EDGE,"E17");Q64=makeQuery(id+"FPISK7QOFB9ojP9_2.opFillet","BLEND_EDGE",EDGE,{"blendedFrom":[makeQuery(id+"F3.opExtrude","CAP_VERTEX",VERTEX,{"disambiguationData":[OSD([sQuery(id+"F2.wireOp",EDGE,"E16"),subQ0])],"isStart":false}),makeQuery(id+"F3.opExtrude","CAP_EDGE",EDGE,{"disambiguationData":[OSD([sQuery(id+"F2.wireOp",EDGE,"E8"),subQ0])],"isStart":false})],"blendedInto":[]});}
            var Q65;
            {var subQ0=sQuery(id+"F2.wireOp",EDGE,"E20");Q65=makeQuery(id+"FPISK7QOFB9ojP9_2.opFillet","BLEND_EDGE",EDGE,{"blendedFrom":[makeQuery(id+"F3.opExtrude","SWEPT_EDGE",EDGE,{"disambiguationData":[OSD([subQ0,sQuery(id+"F2.wireOp",EDGE,"E23")])]}),makeQuery(id+"F3.opExtrude","SWEPT_FACE",FACE,{"disambiguationData":[OSD([subQ0])]})],"blendedInto":[makeQuery(id+"F3.opExtrude","SWEPT_FACE",FACE,{"disambiguationData":[OSD([subQ0])]})]});}
            var Q66;
            {var subQ0=sQuery(id+"F2.wireOp",EDGE,"E15");Q66=makeQuery(id+"FPISK7QOFB9ojP9_2.opFillet","BLEND_EDGE",EDGE,{"blendedFrom":[makeQuery(id+"F3.opExtrude","CAP_EDGE",EDGE,{"disambiguationData":[OSD([subQ0])],"isStart":false}),makeQuery(id+"F3.opExtrude","CAP_FACE",FACE,{"disambiguationData":[OSD([sQuery(id+"F2.wireOp",EDGE,"E7"),sQuery(id+"F2.wireOp",EDGE,"E8"),sQuery(id+"F2.wireOp",EDGE,"E9"),sQuery(id+"F2.wireOp",EDGE,"E10"),sQuery(id+"F2.wireOp",EDGE,"E11"),sQuery(id+"F2.wireOp",EDGE,"E12"),sQuery(id+"F2.wireOp",EDGE,"E13"),sQuery(id+"F2.wireOp",EDGE,"E14"),subQ0,sQuery(id+"F2.wireOp",EDGE,"E16"),sQuery(id+"F2.wireOp",EDGE,"E17"),sQuery(id+"F2.wireOp",EDGE,"E18"),sQuery(id+"F2.wireOp",EDGE,"E19"),sQuery(id+"F2.wireOp",EDGE,"E20"),sQuery(id+"F2.wireOp",EDGE,"E21"),sQuery(id+"F2.wireOp",EDGE,"E22"),sQuery(id+"F2.wireOp",EDGE,"E23"),sQuery(id+"F2.wireOp",EDGE,"E24")])],"isStart":false})],"blendedInto":[makeQuery(id+"F3.opExtrude","CAP_FACE",FACE,{"disambiguationData":[OSD([sQuery(id+"F2.wireOp",EDGE,"E7"),sQuery(id+"F2.wireOp",EDGE,"E8"),sQuery(id+"F2.wireOp",EDGE,"E9"),sQuery(id+"F2.wireOp",EDGE,"E10"),sQuery(id+"F2.wireOp",EDGE,"E11"),sQuery(id+"F2.wireOp",EDGE,"E12"),sQuery(id+"F2.wireOp",EDGE,"E13"),sQuery(id+"F2.wireOp",EDGE,"E14"),subQ0,sQuery(id+"F2.wireOp",EDGE,"E16"),sQuery(id+"F2.wireOp",EDGE,"E17"),sQuery(id+"F2.wireOp",EDGE,"E18"),sQuery(id+"F2.wireOp",EDGE,"E19"),sQuery(id+"F2.wireOp",EDGE,"E20"),sQuery(id+"F2.wireOp",EDGE,"E21"),sQuery(id+"F2.wireOp",EDGE,"E22"),sQuery(id+"F2.wireOp",EDGE,"E23"),sQuery(id+"F2.wireOp",EDGE,"E24")])],"isStart":false})]});}
            var Q67;
            {var subQ0=sQuery(id+"F2.wireOp",EDGE,"E22");var subQ1=sQuery(id+"F2.wireOp",EDGE,"E10");Q67=makeQuery(id+"FPISK7QOFB9ojP9_2.opFillet","BLEND_EDGE",EDGE,{"blendedFrom":[makeQuery(id+"F3.opExtrude","CAP_EDGE",EDGE,{"disambiguationData":[OSD([subQ1,subQ0])],"isStart":false}),makeQuery(id+"F3.opExtrude","CAP_FACE",FACE,{"disambiguationData":[OSD([sQuery(id+"F2.wireOp",EDGE,"E7"),sQuery(id+"F2.wireOp",EDGE,"E8"),sQuery(id+"F2.wireOp",EDGE,"E9"),subQ1,sQuery(id+"F2.wireOp",EDGE,"E11"),sQuery(id+"F2.wireOp",EDGE,"E12"),sQuery(id+"F2.wireOp",EDGE,"E13"),sQuery(id+"F2.wireOp",EDGE,"E14"),sQuery(id+"F2.wireOp",EDGE,"E15"),sQuery(id+"F2.wireOp",EDGE,"E16"),sQuery(id+"F2.wireOp",EDGE,"E17"),sQuery(id+"F2.wireOp",EDGE,"E18"),sQuery(id+"F2.wireOp",EDGE,"E19"),sQuery(id+"F2.wireOp",EDGE,"E20"),sQuery(id+"F2.wireOp",EDGE,"E21"),subQ0,sQuery(id+"F2.wireOp",EDGE,"E23"),sQuery(id+"F2.wireOp",EDGE,"E24")])],"isStart":false})],"blendedInto":[makeQuery(id+"F3.opExtrude","CAP_FACE",FACE,{"disambiguationData":[OSD([sQuery(id+"F2.wireOp",EDGE,"E7"),sQuery(id+"F2.wireOp",EDGE,"E8"),sQuery(id+"F2.wireOp",EDGE,"E9"),subQ1,sQuery(id+"F2.wireOp",EDGE,"E11"),sQuery(id+"F2.wireOp",EDGE,"E12"),sQuery(id+"F2.wireOp",EDGE,"E13"),sQuery(id+"F2.wireOp",EDGE,"E14"),sQuery(id+"F2.wireOp",EDGE,"E15"),sQuery(id+"F2.wireOp",EDGE,"E16"),sQuery(id+"F2.wireOp",EDGE,"E17"),sQuery(id+"F2.wireOp",EDGE,"E18"),sQuery(id+"F2.wireOp",EDGE,"E19"),sQuery(id+"F2.wireOp",EDGE,"E20"),sQuery(id+"F2.wireOp",EDGE,"E21"),subQ0,sQuery(id+"F2.wireOp",EDGE,"E23"),sQuery(id+"F2.wireOp",EDGE,"E24")])],"isStart":false})]});}
            var Q68;
            {var subQ0=sQuery(id+"F2.wireOp",EDGE,"E17");Q68=makeQuery(id+"FPISK7QOFB9ojP9_2.opFillet","BLEND_EDGE",EDGE,{"blendedFrom":[makeQuery(id+"F3.opExtrude","SWEPT_EDGE",EDGE,{"disambiguationData":[OSD([sQuery(id+"F2.wireOp",EDGE,"E16"),subQ0])]}),makeQuery(id+"F3.opExtrude","SWEPT_FACE",FACE,{"disambiguationData":[OSD([sQuery(id+"F2.wireOp",EDGE,"E8"),subQ0])]})],"blendedInto":[makeQuery(id+"F3.opExtrude","SWEPT_FACE",FACE,{"disambiguationData":[OSD([sQuery(id+"F2.wireOp",EDGE,"E8"),subQ0])]})]});}
            var Q69;
            {var subQ0=sQuery(id+"F2.wireOp",EDGE,"E23");var subQ1=sQuery(id+"F2.wireOp",EDGE,"E20");Q69=makeQuery(id+"FPISK7QOFB9ojP9_2.opFillet","BLEND_FACE",FACE,{"disambiguationData":[OSD([subQ1,subQ0]),TDD([makeQuery(id+"F3.opExtrude","SWEPT_EDGE",EDGE,{"disambiguationData":[OSD([subQ1,subQ0])]})])]});}
            var Q70;
            {var subQ0=sQuery(id+"F2.wireOp",EDGE,"E18");var subQ1=sQuery(id+"F2.wireOp",EDGE,"E15");Q70=makeQuery(id+"FPISK7QOFB9ojP9_2.opFillet","BLEND_FACE",FACE,{"disambiguationData":[OSD([subQ1,subQ0]),TDD([makeQuery(id+"F3.opExtrude","CAP_VERTEX",VERTEX,{"disambiguationData":[OSD([subQ1,subQ0])],"isStart":false})])]});}
            var Q71;
            {var subQ0=sQuery(id+"F2.wireOp",EDGE,"E18");Q71=makeQuery(id+"FPISK7QOFB9ojP9_2.opFillet","BLEND_EDGE",EDGE,{"blendedFrom":[makeQuery(id+"F3.opExtrude","CAP_EDGE",EDGE,{"disambiguationData":[OSD([subQ0])],"isStart":false}),makeQuery(id+"F3.opExtrude","CAP_FACE",FACE,{"disambiguationData":[OSD([sQuery(id+"F2.wireOp",EDGE,"E7"),sQuery(id+"F2.wireOp",EDGE,"E8"),sQuery(id+"F2.wireOp",EDGE,"E9"),sQuery(id+"F2.wireOp",EDGE,"E10"),sQuery(id+"F2.wireOp",EDGE,"E11"),sQuery(id+"F2.wireOp",EDGE,"E12"),sQuery(id+"F2.wireOp",EDGE,"E13"),sQuery(id+"F2.wireOp",EDGE,"E14"),sQuery(id+"F2.wireOp",EDGE,"E15"),sQuery(id+"F2.wireOp",EDGE,"E16"),sQuery(id+"F2.wireOp",EDGE,"E17"),subQ0,sQuery(id+"F2.wireOp",EDGE,"E19"),sQuery(id+"F2.wireOp",EDGE,"E20"),sQuery(id+"F2.wireOp",EDGE,"E21"),sQuery(id+"F2.wireOp",EDGE,"E22"),sQuery(id+"F2.wireOp",EDGE,"E23"),sQuery(id+"F2.wireOp",EDGE,"E24")])],"isStart":false})],"blendedInto":[makeQuery(id+"F3.opExtrude","CAP_FACE",FACE,{"disambiguationData":[OSD([sQuery(id+"F2.wireOp",EDGE,"E7"),sQuery(id+"F2.wireOp",EDGE,"E8"),sQuery(id+"F2.wireOp",EDGE,"E9"),sQuery(id+"F2.wireOp",EDGE,"E10"),sQuery(id+"F2.wireOp",EDGE,"E11"),sQuery(id+"F2.wireOp",EDGE,"E12"),sQuery(id+"F2.wireOp",EDGE,"E13"),sQuery(id+"F2.wireOp",EDGE,"E14"),sQuery(id+"F2.wireOp",EDGE,"E15"),sQuery(id+"F2.wireOp",EDGE,"E16"),sQuery(id+"F2.wireOp",EDGE,"E17"),subQ0,sQuery(id+"F2.wireOp",EDGE,"E19"),sQuery(id+"F2.wireOp",EDGE,"E20"),sQuery(id+"F2.wireOp",EDGE,"E21"),sQuery(id+"F2.wireOp",EDGE,"E22"),sQuery(id+"F2.wireOp",EDGE,"E23"),sQuery(id+"F2.wireOp",EDGE,"E24")])],"isStart":false})]});}
            var Q72;
            {var subQ0=sQuery(id+"F2.wireOp",EDGE,"E21");var subQ1=sQuery(id+"F2.wireOp",EDGE,"E11");Q72=makeQuery(id+"FPISK7QOFB9ojP9_2.opFillet","BLEND_EDGE",EDGE,{"blendedFrom":[makeQuery(id+"F3.opExtrude","CAP_EDGE",EDGE,{"disambiguationData":[OSD([subQ1,subQ0])],"isStart":false}),makeQuery(id+"F3.opExtrude","CAP_FACE",FACE,{"disambiguationData":[OSD([sQuery(id+"F2.wireOp",EDGE,"E7"),sQuery(id+"F2.wireOp",EDGE,"E8"),sQuery(id+"F2.wireOp",EDGE,"E9"),sQuery(id+"F2.wireOp",EDGE,"E10"),subQ1,sQuery(id+"F2.wireOp",EDGE,"E12"),sQuery(id+"F2.wireOp",EDGE,"E13"),sQuery(id+"F2.wireOp",EDGE,"E14"),sQuery(id+"F2.wireOp",EDGE,"E15"),sQuery(id+"F2.wireOp",EDGE,"E16"),sQuery(id+"F2.wireOp",EDGE,"E17"),sQuery(id+"F2.wireOp",EDGE,"E18"),sQuery(id+"F2.wireOp",EDGE,"E19"),sQuery(id+"F2.wireOp",EDGE,"E20"),subQ0,sQuery(id+"F2.wireOp",EDGE,"E22"),sQuery(id+"F2.wireOp",EDGE,"E23"),sQuery(id+"F2.wireOp",EDGE,"E24")])],"isStart":false})],"blendedInto":[makeQuery(id+"F3.opExtrude","CAP_FACE",FACE,{"disambiguationData":[OSD([sQuery(id+"F2.wireOp",EDGE,"E7"),sQuery(id+"F2.wireOp",EDGE,"E8"),sQuery(id+"F2.wireOp",EDGE,"E9"),sQuery(id+"F2.wireOp",EDGE,"E10"),subQ1,sQuery(id+"F2.wireOp",EDGE,"E12"),sQuery(id+"F2.wireOp",EDGE,"E13"),sQuery(id+"F2.wireOp",EDGE,"E14"),sQuery(id+"F2.wireOp",EDGE,"E15"),sQuery(id+"F2.wireOp",EDGE,"E16"),sQuery(id+"F2.wireOp",EDGE,"E17"),sQuery(id+"F2.wireOp",EDGE,"E18"),sQuery(id+"F2.wireOp",EDGE,"E19"),sQuery(id+"F2.wireOp",EDGE,"E20"),subQ0,sQuery(id+"F2.wireOp",EDGE,"E22"),sQuery(id+"F2.wireOp",EDGE,"E23"),sQuery(id+"F2.wireOp",EDGE,"E24")])],"isStart":false})]});}
            var Q73;
            {var subQ0=sQuery(id+"F2.wireOp",EDGE,"E14");var subQ1=sQuery(id+"F2.wireOp",EDGE,"E7");Q73=makeQuery(id+"FPISK7QOFB9ojP9_2.opFillet","BLEND_EDGE",EDGE,{"blendedFrom":[makeQuery(id+"F3.opExtrude","CAP_EDGE",EDGE,{"disambiguationData":[OSD([subQ1,subQ0])],"isStart":false}),makeQuery(id+"F3.opExtrude","CAP_FACE",FACE,{"disambiguationData":[OSD([subQ1,sQuery(id+"F2.wireOp",EDGE,"E8"),sQuery(id+"F2.wireOp",EDGE,"E9"),sQuery(id+"F2.wireOp",EDGE,"E10"),sQuery(id+"F2.wireOp",EDGE,"E11"),sQuery(id+"F2.wireOp",EDGE,"E12"),sQuery(id+"F2.wireOp",EDGE,"E13"),subQ0,sQuery(id+"F2.wireOp",EDGE,"E15"),sQuery(id+"F2.wireOp",EDGE,"E16"),sQuery(id+"F2.wireOp",EDGE,"E17"),sQuery(id+"F2.wireOp",EDGE,"E18"),sQuery(id+"F2.wireOp",EDGE,"E19"),sQuery(id+"F2.wireOp",EDGE,"E20"),sQuery(id+"F2.wireOp",EDGE,"E21"),sQuery(id+"F2.wireOp",EDGE,"E22"),sQuery(id+"F2.wireOp",EDGE,"E23"),sQuery(id+"F2.wireOp",EDGE,"E24")])],"isStart":false})],"blendedInto":[makeQuery(id+"F3.opExtrude","CAP_FACE",FACE,{"disambiguationData":[OSD([subQ1,sQuery(id+"F2.wireOp",EDGE,"E8"),sQuery(id+"F2.wireOp",EDGE,"E9"),sQuery(id+"F2.wireOp",EDGE,"E10"),sQuery(id+"F2.wireOp",EDGE,"E11"),sQuery(id+"F2.wireOp",EDGE,"E12"),sQuery(id+"F2.wireOp",EDGE,"E13"),subQ0,sQuery(id+"F2.wireOp",EDGE,"E15"),sQuery(id+"F2.wireOp",EDGE,"E16"),sQuery(id+"F2.wireOp",EDGE,"E17"),sQuery(id+"F2.wireOp",EDGE,"E18"),sQuery(id+"F2.wireOp",EDGE,"E19"),sQuery(id+"F2.wireOp",EDGE,"E20"),sQuery(id+"F2.wireOp",EDGE,"E21"),sQuery(id+"F2.wireOp",EDGE,"E22"),sQuery(id+"F2.wireOp",EDGE,"E23"),sQuery(id+"F2.wireOp",EDGE,"E24")])],"isStart":false})]});}
            var Q74;
            {var subQ0=sQuery(id+"F2.wireOp",EDGE,"E16");Q74=makeQuery(id+"FPISK7QOFB9ojP9_2.opFillet","BLEND_EDGE",EDGE,{"blendedFrom":[makeQuery(id+"F3.opExtrude","CAP_VERTEX",VERTEX,{"disambiguationData":[OSD([subQ0,sQuery(id+"F2.wireOp",EDGE,"E17")])],"isStart":false}),makeQuery(id+"F3.opExtrude","CAP_EDGE",EDGE,{"disambiguationData":[OSD([sQuery(id+"F2.wireOp",EDGE,"E9"),subQ0,sQuery(id+"F2.wireOp",EDGE,"E19")])],"isStart":false})],"blendedInto":[]});}
            var Q75;
            {var subQ0=sQuery(id+"F2.wireOp",EDGE,"E19");var subQ1=sQuery(id+"F2.wireOp",EDGE,"E16");var subQ2=sQuery(id+"F2.wireOp",EDGE,"E9");Q75=makeQuery(id+"FPISK7QOFB9ojP9_2.opFillet","BLEND_EDGE",EDGE,{"blendedFrom":[makeQuery(id+"F3.opExtrude","CAP_EDGE",EDGE,{"disambiguationData":[OSD([subQ2,subQ1,subQ0])],"isStart":false}),makeQuery(id+"F3.opExtrude","SWEPT_FACE",FACE,{"disambiguationData":[OSD([subQ2,subQ1,subQ0])]})],"blendedInto":[makeQuery(id+"F3.opExtrude","SWEPT_FACE",FACE,{"disambiguationData":[OSD([subQ2,subQ1,subQ0])]})]});}
            var Q76;
            {var subQ0=sQuery(id+"F2.wireOp",EDGE,"E8");Q76=makeQuery(id+"FPISK7QOFB9ojP9_2.opFillet","BLEND_EDGE",EDGE,{"blendedFrom":[makeQuery(id+"F3.opExtrude","SWEPT_EDGE",EDGE,{"disambiguationData":[OSD([subQ0,sQuery(id+"F2.wireOp",EDGE,"E14")])]}),makeQuery(id+"F3.opExtrude","SWEPT_FACE",FACE,{"disambiguationData":[OSD([subQ0,sQuery(id+"F2.wireOp",EDGE,"E17")])]})],"blendedInto":[makeQuery(id+"F3.opExtrude","SWEPT_FACE",FACE,{"disambiguationData":[OSD([subQ0,sQuery(id+"F2.wireOp",EDGE,"E17")])]})]});}
            var Q77;
            {var subQ0=sQuery(id+"F2.wireOp",EDGE,"E23");Q77=makeQuery(id+"FPISK7QOFB9ojP9_2.opFillet","BLEND_EDGE",EDGE,{"blendedFrom":[makeQuery(id+"F3.opExtrude","CAP_EDGE",EDGE,{"disambiguationData":[OSD([subQ0])],"isStart":false}),makeQuery(id+"F3.opExtrude","SWEPT_FACE",FACE,{"disambiguationData":[OSD([subQ0])]})],"blendedInto":[makeQuery(id+"F3.opExtrude","SWEPT_FACE",FACE,{"disambiguationData":[OSD([subQ0])]})]});}
            var Q78;
            {var subQ0=sQuery(id+"F2.wireOp",EDGE,"E17");var subQ1=sQuery(id+"F2.wireOp",EDGE,"E8");Q78=makeQuery(id+"FPISK7QOFB9ojP9_2.opFillet","BLEND_FACE",FACE,{"disambiguationData":[OSD([subQ1,subQ0]),TDD([makeQuery(id+"F3.opExtrude","CAP_EDGE",EDGE,{"disambiguationData":[OSD([subQ1,subQ0])],"isStart":true})])]});}
            var Q79;
            {var subQ0=sQuery(id+"F2.wireOp",EDGE,"E20");Q79=makeQuery(id+"FPISK7QOFB9ojP9_2.opFillet","BLEND_FACE",FACE,{"disambiguationData":[OSD([subQ0]),TDD([makeQuery(id+"F3.opExtrude","CAP_EDGE",EDGE,{"disambiguationData":[OSD([subQ0])],"isStart":true})])]});}
            var Q80;
            {var subQ0=sQuery(id+"F2.wireOp",EDGE,"E22");var subQ1=sQuery(id+"F2.wireOp",EDGE,"E21");Q80=makeQuery(id+"FPISK7QOFB9ojP9_2.opFillet","BLEND_FACE",FACE,{"disambiguationData":[OSD([subQ1,subQ0]),TDD([makeQuery(id+"F3.opExtrude","CAP_VERTEX",VERTEX,{"disambiguationData":[OSD([subQ1,subQ0])],"isStart":false})])]});}
            var Q81;
            {var subQ0=sQuery(id+"F2.wireOp",EDGE,"E12");var subQ1=sQuery(id+"F2.wireOp",EDGE,"E7");Q81=makeQuery(id+"FPISK7QOFB9ojP9_2.opFillet","BLEND_FACE",FACE,{"disambiguationData":[OSD([subQ1,subQ0]),TDD([makeQuery(id+"F3.opExtrude","CAP_VERTEX",VERTEX,{"disambiguationData":[OSD([subQ1,subQ0])],"isStart":true})])]});}
            var Q82;
            {var subQ0=sQuery(id+"F2.wireOp",EDGE,"E12");var subQ1=sQuery(id+"F2.wireOp",EDGE,"E7");Q82=makeQuery(id+"FPISK7QOFB9ojP9_2.opFillet","BLEND_FACE",FACE,{"disambiguationData":[OSD([subQ1,subQ0]),TDD([makeQuery(id+"F3.opExtrude","CAP_VERTEX",VERTEX,{"disambiguationData":[OSD([subQ1,subQ0])],"isStart":false})])]});}
            var Q83;
            {var subQ0=sQuery(id+"F2.wireOp",EDGE,"E13");Q83=makeQuery(id+"FPISK7QOFB9ojP9_2.opFillet","BLEND_EDGE",EDGE,{"blendedFrom":[makeQuery(id+"F3.opExtrude","SWEPT_EDGE",EDGE,{"disambiguationData":[OSD([subQ0,sQuery(id+"F2.wireOp",EDGE,"E15")])]}),makeQuery(id+"F3.opExtrude","SWEPT_FACE",FACE,{"disambiguationData":[OSD([subQ0])]})],"blendedInto":[makeQuery(id+"F3.opExtrude","SWEPT_FACE",FACE,{"disambiguationData":[OSD([subQ0])]})]});}
            var Q84;
            {var subQ0=sQuery(id+"F2.wireOp",EDGE,"E14");var subQ1=sQuery(id+"F2.wireOp",EDGE,"E8");Q84=makeQuery(id+"FPISK7QOFB9ojP9_2.opFillet","BLEND_FACE",FACE,{"disambiguationData":[OSD([subQ1,subQ0]),TDD([makeQuery(id+"F3.opExtrude","CAP_VERTEX",VERTEX,{"disambiguationData":[OSD([subQ1,subQ0])],"isStart":true})])]});}
            var Q85;
            {var subQ0=sQuery(id+"F2.wireOp",EDGE,"E19");var subQ1=sQuery(id+"F2.wireOp",EDGE,"E10");Q85=makeQuery(id+"FPISK7QOFB9ojP9_2.opFillet","BLEND_FACE",FACE,{"disambiguationData":[OSD([subQ1,subQ0]),TDD([makeQuery(id+"F3.opExtrude","CAP_VERTEX",VERTEX,{"disambiguationData":[OSD([subQ1,subQ0])],"isStart":true})])]});}
            var Q86;
            {var subQ0=sQuery(id+"F2.wireOp",EDGE,"E17");var subQ1=sQuery(id+"F2.wireOp",EDGE,"E16");Q86=makeQuery(id+"FPISK7QOFB9ojP9_2.opFillet","BLEND_FACE",FACE,{"disambiguationData":[OSD([subQ1,subQ0]),TDD([makeQuery(id+"F3.opExtrude","SWEPT_EDGE",EDGE,{"disambiguationData":[OSD([subQ1,subQ0])]})])]});}
            var Q87;
            {var subQ0=sQuery(id+"F2.wireOp",EDGE,"E18");Q87=makeQuery(id+"FPISK7QOFB9ojP9_2.opFillet","BLEND_EDGE",EDGE,{"blendedFrom":[makeQuery(id+"F3.opExtrude","CAP_EDGE",EDGE,{"disambiguationData":[OSD([subQ0])],"isStart":false}),makeQuery(id+"F3.opExtrude","SWEPT_FACE",FACE,{"disambiguationData":[OSD([subQ0])]})],"blendedInto":[makeQuery(id+"F3.opExtrude","SWEPT_FACE",FACE,{"disambiguationData":[OSD([subQ0])]})]});}
            var Q88;
            {var subQ0=sQuery(id+"F2.wireOp",EDGE,"E24");var subQ1=sQuery(id+"F2.wireOp",EDGE,"E11");Q88=makeQuery(id+"FPISK7QOFB9ojP9_2.opFillet","BLEND_FACE",FACE,{"disambiguationData":[OSD([subQ1,subQ0]),TDD([makeQuery(id+"F3.opExtrude","CAP_VERTEX",VERTEX,{"disambiguationData":[OSD([subQ1,subQ0])],"isStart":false})])]});}
            var Q89;
            {var subQ0=sQuery(id+"F2.wireOp",EDGE,"E13");var subQ1=sQuery(id+"F2.wireOp",EDGE,"E12");Q89=makeQuery(id+"FPISK7QOFB9ojP9_2.opFillet","BLEND_FACE",FACE,{"disambiguationData":[OSD([subQ1,subQ0]),TDD([makeQuery(id+"F3.opExtrude","CAP_VERTEX",VERTEX,{"disambiguationData":[OSD([subQ1,subQ0])],"isStart":true})])]});}
            var Q90;
            {var subQ0=sQuery(id+"F2.wireOp",EDGE,"E13");var subQ1=sQuery(id+"F2.wireOp",EDGE,"E12");Q90=makeQuery(id+"FPISK7QOFB9ojP9_2.opFillet","BLEND_FACE",FACE,{"disambiguationData":[OSD([subQ1,subQ0]),TDD([makeQuery(id+"F3.opExtrude","CAP_VERTEX",VERTEX,{"disambiguationData":[OSD([subQ1,subQ0])],"isStart":false})])]});}
            var Q91;
            {var subQ0=sQuery(id+"F2.wireOp",EDGE,"E14");Q91=makeQuery(id+"FPISK7QOFB9ojP9_2.opFillet","BLEND_EDGE",EDGE,{"blendedFrom":[makeQuery(id+"F3.opExtrude","CAP_VERTEX",VERTEX,{"disambiguationData":[OSD([sQuery(id+"F2.wireOp",EDGE,"E8"),subQ0])],"isStart":false}),makeQuery(id+"F3.opExtrude","CAP_EDGE",EDGE,{"disambiguationData":[OSD([sQuery(id+"F2.wireOp",EDGE,"E7"),subQ0])],"isStart":false})],"blendedInto":[]});}
            var Q92;
            {var subQ0=sQuery(id+"F2.wireOp",EDGE,"E22");var subQ1=sQuery(id+"F2.wireOp",EDGE,"E21");Q92=makeQuery(id+"FPISK7QOFB9ojP9_2.opFillet","BLEND_FACE",FACE,{"disambiguationData":[OSD([subQ1,subQ0]),TDD([makeQuery(id+"F3.opExtrude","CAP_VERTEX",VERTEX,{"disambiguationData":[OSD([subQ1,subQ0])],"isStart":true})])]});}
            var Q93;
            {var subQ0=sQuery(id+"F2.wireOp",EDGE,"E19");Q93=makeQuery(id+"FPISK7QOFB9ojP9_2.opFillet","BLEND_EDGE",EDGE,{"blendedFrom":[makeQuery(id+"F3.opExtrude","SWEPT_EDGE",EDGE,{"disambiguationData":[OSD([sQuery(id+"F2.wireOp",EDGE,"E10"),subQ0])]}),makeQuery(id+"F3.opExtrude","SWEPT_FACE",FACE,{"disambiguationData":[OSD([sQuery(id+"F2.wireOp",EDGE,"E9"),sQuery(id+"F2.wireOp",EDGE,"E16"),subQ0])]})],"blendedInto":[makeQuery(id+"F3.opExtrude","SWEPT_FACE",FACE,{"disambiguationData":[OSD([sQuery(id+"F2.wireOp",EDGE,"E9"),sQuery(id+"F2.wireOp",EDGE,"E16"),subQ0])]})]});}
            var Q94;
            {var subQ0=sQuery(id+"F2.wireOp",EDGE,"E24");Q94=makeQuery(id+"FPISK7QOFB9ojP9_2.opFillet","BLEND_EDGE",EDGE,{"blendedFrom":[makeQuery(id+"F3.opExtrude","SWEPT_EDGE",EDGE,{"disambiguationData":[OSD([sQuery(id+"F2.wireOp",EDGE,"E11"),subQ0])]}),makeQuery(id+"F3.opExtrude","SWEPT_FACE",FACE,{"disambiguationData":[OSD([subQ0])]})],"blendedInto":[makeQuery(id+"F3.opExtrude","SWEPT_FACE",FACE,{"disambiguationData":[OSD([subQ0])]})]});}
            var Q95;
            Q95=makeQuery(id+"F3.opExtrude","SWEPT_FACE",FACE,{"disambiguationData":[OSD([sQuery(id+"F2.wireOp",EDGE,"E9"),sQuery(id+"F2.wireOp",EDGE,"E16"),sQuery(id+"F2.wireOp",EDGE,"E19")])]});
            var Q96;
            {var subQ0=sQuery(id+"F2.wireOp",EDGE,"E13");Q96=makeQuery(id+"FPISK7QOFB9ojP9_2.opFillet","BLEND_FACE",FACE,{"disambiguationData":[OSD([subQ0]),TDD([makeQuery(id+"F3.opExtrude","CAP_EDGE",EDGE,{"disambiguationData":[OSD([subQ0])],"isStart":true})])]});}
            var Q97;
            {var subQ0=sQuery(id+"F2.wireOp",EDGE,"E15");var subQ1=sQuery(id+"F2.wireOp",EDGE,"E13");Q97=makeQuery(id+"FPISK7QOFB9ojP9_2.opFillet","BLEND_FACE",FACE,{"disambiguationData":[OSD([subQ1,subQ0]),TDD([makeQuery(id+"F3.opExtrude","SWEPT_EDGE",EDGE,{"disambiguationData":[OSD([subQ1,subQ0])]})])]});}
            var Q98;
            {var subQ0=sQuery(id+"F2.wireOp",EDGE,"E15");Q98=makeQuery(id+"FPISK7QOFB9ojP9_2.opFillet","BLEND_EDGE",EDGE,{"blendedFrom":[makeQuery(id+"F3.opExtrude","CAP_EDGE",EDGE,{"disambiguationData":[OSD([subQ0])],"isStart":false}),makeQuery(id+"F3.opExtrude","SWEPT_FACE",FACE,{"disambiguationData":[OSD([subQ0])]})],"blendedInto":[makeQuery(id+"F3.opExtrude","SWEPT_FACE",FACE,{"disambiguationData":[OSD([subQ0])]})]});}
            var Q99;
            {var subQ0=sQuery(id+"F2.wireOp",EDGE,"E22");var subQ1=sQuery(id+"F2.wireOp",EDGE,"E10");Q99=makeQuery(id+"FPISK7QOFB9ojP9_2.opFillet","BLEND_EDGE",EDGE,{"blendedFrom":[makeQuery(id+"F3.opExtrude","CAP_EDGE",EDGE,{"disambiguationData":[OSD([subQ1,subQ0])],"isStart":false}),makeQuery(id+"F3.opExtrude","SWEPT_FACE",FACE,{"disambiguationData":[OSD([subQ1,subQ0])]})],"blendedInto":[makeQuery(id+"F3.opExtrude","SWEPT_FACE",FACE,{"disambiguationData":[OSD([subQ1,subQ0])]})]});}
            var Q100;
            {var subQ0=sQuery(id+"F2.wireOp",EDGE,"E23");Q100=makeQuery(id+"FPISK7QOFB9ojP9_2.opFillet","BLEND_EDGE",EDGE,{"blendedFrom":[makeQuery(id+"F3.opExtrude","SWEPT_EDGE",EDGE,{"disambiguationData":[OSD([sQuery(id+"F2.wireOp",EDGE,"E20"),subQ0])]}),makeQuery(id+"F3.opExtrude","SWEPT_FACE",FACE,{"disambiguationData":[OSD([subQ0])]})],"blendedInto":[makeQuery(id+"F3.opExtrude","SWEPT_FACE",FACE,{"disambiguationData":[OSD([subQ0])]})]});}
            var Q101;
            {var subQ0=sQuery(id+"F2.wireOp",EDGE,"E24");Q101=makeQuery(id+"FPISK7QOFB9ojP9_2.opFillet","BLEND_FACE",FACE,{"disambiguationData":[OSD([subQ0]),TDD([makeQuery(id+"F3.opExtrude","CAP_EDGE",EDGE,{"disambiguationData":[OSD([subQ0])],"isStart":false})])]});}
            var Q102;
            {var subQ0=sQuery(id+"F2.wireOp",EDGE,"E23");var subQ1=sQuery(id+"F2.wireOp",EDGE,"E20");Q102=makeQuery(id+"FPISK7QOFB9ojP9_2.opFillet","BLEND_FACE",FACE,{"disambiguationData":[OSD([subQ1,subQ0]),TDD([makeQuery(id+"F3.opExtrude","CAP_VERTEX",VERTEX,{"disambiguationData":[OSD([subQ1,subQ0])],"isStart":false})])]});}
            var Q103;
            {var subQ0=sQuery(id+"F2.wireOp",EDGE,"E15");Q103=makeQuery(id+"FPISK7QOFB9ojP9_2.opFillet","BLEND_EDGE",EDGE,{"blendedFrom":[makeQuery(id+"F3.opExtrude","SWEPT_EDGE",EDGE,{"disambiguationData":[OSD([sQuery(id+"F2.wireOp",EDGE,"E13"),subQ0])]}),makeQuery(id+"F3.opExtrude","SWEPT_FACE",FACE,{"disambiguationData":[OSD([subQ0])]})],"blendedInto":[makeQuery(id+"F3.opExtrude","SWEPT_FACE",FACE,{"disambiguationData":[OSD([subQ0])]})]});}
            var Q104;
            {var subQ0=sQuery(id+"F2.wireOp",EDGE,"E20");var subQ1=sQuery(id+"F2.wireOp",EDGE,"E18");Q104=makeQuery(id+"FPISK7QOFB9ojP9_2.opFillet","BLEND_FACE",FACE,{"disambiguationData":[OSD([subQ1,subQ0]),TDD([makeQuery(id+"F3.opExtrude","CAP_VERTEX",VERTEX,{"disambiguationData":[OSD([subQ1,subQ0])],"isStart":false})])]});}
            var Q105;
            {var subQ0=sQuery(id+"F2.wireOp",EDGE,"E15");var subQ1=sQuery(id+"F2.wireOp",EDGE,"E13");Q105=makeQuery(id+"FPISK7QOFB9ojP9_2.opFillet","BLEND_FACE",FACE,{"disambiguationData":[OSD([subQ1,subQ0]),TDD([makeQuery(id+"F3.opExtrude","CAP_VERTEX",VERTEX,{"disambiguationData":[OSD([subQ1,subQ0])],"isStart":false})])]});}
            var Q106;
            {var subQ0=sQuery(id+"F2.wireOp",EDGE,"E22");var subQ1=sQuery(id+"F2.wireOp",EDGE,"E10");Q106=makeQuery(id+"FPISK7QOFB9ojP9_2.opFillet","BLEND_EDGE",EDGE,{"blendedFrom":[makeQuery(id+"F3.opExtrude","CAP_EDGE",EDGE,{"disambiguationData":[OSD([subQ1,subQ0])],"isStart":true}),makeQuery(id+"F3.opExtrude","SWEPT_FACE",FACE,{"disambiguationData":[OSD([subQ1,subQ0])]})],"blendedInto":[makeQuery(id+"F3.opExtrude","SWEPT_FACE",FACE,{"disambiguationData":[OSD([subQ1,subQ0])]})]});}
            var Q107;
            {var subQ0=sQuery(id+"F2.wireOp",EDGE,"E17");var subQ1=sQuery(id+"F2.wireOp",EDGE,"E8");Q107=makeQuery(id+"FPISK7QOFB9ojP9_2.opFillet","BLEND_EDGE",EDGE,{"blendedFrom":[makeQuery(id+"F3.opExtrude","CAP_EDGE",EDGE,{"disambiguationData":[OSD([subQ1,subQ0])],"isStart":false}),makeQuery(id+"F3.opExtrude","CAP_FACE",FACE,{"disambiguationData":[OSD([sQuery(id+"F2.wireOp",EDGE,"E7"),subQ1,sQuery(id+"F2.wireOp",EDGE,"E9"),sQuery(id+"F2.wireOp",EDGE,"E10"),sQuery(id+"F2.wireOp",EDGE,"E11"),sQuery(id+"F2.wireOp",EDGE,"E12"),sQuery(id+"F2.wireOp",EDGE,"E13"),sQuery(id+"F2.wireOp",EDGE,"E14"),sQuery(id+"F2.wireOp",EDGE,"E15"),sQuery(id+"F2.wireOp",EDGE,"E16"),subQ0,sQuery(id+"F2.wireOp",EDGE,"E18"),sQuery(id+"F2.wireOp",EDGE,"E19"),sQuery(id+"F2.wireOp",EDGE,"E20"),sQuery(id+"F2.wireOp",EDGE,"E21"),sQuery(id+"F2.wireOp",EDGE,"E22"),sQuery(id+"F2.wireOp",EDGE,"E23"),sQuery(id+"F2.wireOp",EDGE,"E24")])],"isStart":false})],"blendedInto":[makeQuery(id+"F3.opExtrude","CAP_FACE",FACE,{"disambiguationData":[OSD([sQuery(id+"F2.wireOp",EDGE,"E7"),subQ1,sQuery(id+"F2.wireOp",EDGE,"E9"),sQuery(id+"F2.wireOp",EDGE,"E10"),sQuery(id+"F2.wireOp",EDGE,"E11"),sQuery(id+"F2.wireOp",EDGE,"E12"),sQuery(id+"F2.wireOp",EDGE,"E13"),sQuery(id+"F2.wireOp",EDGE,"E14"),sQuery(id+"F2.wireOp",EDGE,"E15"),sQuery(id+"F2.wireOp",EDGE,"E16"),subQ0,sQuery(id+"F2.wireOp",EDGE,"E18"),sQuery(id+"F2.wireOp",EDGE,"E19"),sQuery(id+"F2.wireOp",EDGE,"E20"),sQuery(id+"F2.wireOp",EDGE,"E21"),sQuery(id+"F2.wireOp",EDGE,"E22"),sQuery(id+"F2.wireOp",EDGE,"E23"),sQuery(id+"F2.wireOp",EDGE,"E24")])],"isStart":false})]});}
            var Q108;
            {var subQ0=sQuery(id+"F2.wireOp",EDGE,"E23");Q108=makeQuery(id+"FPISK7QOFB9ojP9_2.opFillet","BLEND_EDGE",EDGE,{"blendedFrom":[makeQuery(id+"F3.opExtrude","SWEPT_EDGE",EDGE,{"disambiguationData":[OSD([subQ0,sQuery(id+"F2.wireOp",EDGE,"E24")])]}),makeQuery(id+"F3.opExtrude","SWEPT_FACE",FACE,{"disambiguationData":[OSD([subQ0])]})],"blendedInto":[makeQuery(id+"F3.opExtrude","SWEPT_FACE",FACE,{"disambiguationData":[OSD([subQ0])]})]});}
            var Q109;
            {var subQ0=sQuery(id+"F2.wireOp",EDGE,"E20");Q109=makeQuery(id+"FPISK7QOFB9ojP9_2.opFillet","BLEND_EDGE",EDGE,{"blendedFrom":[makeQuery(id+"F3.opExtrude","SWEPT_EDGE",EDGE,{"disambiguationData":[OSD([sQuery(id+"F2.wireOp",EDGE,"E18"),subQ0])]}),makeQuery(id+"F3.opExtrude","SWEPT_FACE",FACE,{"disambiguationData":[OSD([subQ0])]})],"blendedInto":[makeQuery(id+"F3.opExtrude","SWEPT_FACE",FACE,{"disambiguationData":[OSD([subQ0])]})]});}
            var Q110;
            {var subQ0=sQuery(id+"F2.wireOp",EDGE,"E20");Q110=makeQuery(id+"FPISK7QOFB9ojP9_2.opFillet","BLEND_EDGE",EDGE,{"blendedFrom":[makeQuery(id+"F3.opExtrude","CAP_EDGE",EDGE,{"disambiguationData":[OSD([subQ0])],"isStart":false}),makeQuery(id+"F3.opExtrude","CAP_FACE",FACE,{"disambiguationData":[OSD([sQuery(id+"F2.wireOp",EDGE,"E7"),sQuery(id+"F2.wireOp",EDGE,"E8"),sQuery(id+"F2.wireOp",EDGE,"E9"),sQuery(id+"F2.wireOp",EDGE,"E10"),sQuery(id+"F2.wireOp",EDGE,"E11"),sQuery(id+"F2.wireOp",EDGE,"E12"),sQuery(id+"F2.wireOp",EDGE,"E13"),sQuery(id+"F2.wireOp",EDGE,"E14"),sQuery(id+"F2.wireOp",EDGE,"E15"),sQuery(id+"F2.wireOp",EDGE,"E16"),sQuery(id+"F2.wireOp",EDGE,"E17"),sQuery(id+"F2.wireOp",EDGE,"E18"),sQuery(id+"F2.wireOp",EDGE,"E19"),subQ0,sQuery(id+"F2.wireOp",EDGE,"E21"),sQuery(id+"F2.wireOp",EDGE,"E22"),sQuery(id+"F2.wireOp",EDGE,"E23"),sQuery(id+"F2.wireOp",EDGE,"E24")])],"isStart":false})],"blendedInto":[makeQuery(id+"F3.opExtrude","CAP_FACE",FACE,{"disambiguationData":[OSD([sQuery(id+"F2.wireOp",EDGE,"E7"),sQuery(id+"F2.wireOp",EDGE,"E8"),sQuery(id+"F2.wireOp",EDGE,"E9"),sQuery(id+"F2.wireOp",EDGE,"E10"),sQuery(id+"F2.wireOp",EDGE,"E11"),sQuery(id+"F2.wireOp",EDGE,"E12"),sQuery(id+"F2.wireOp",EDGE,"E13"),sQuery(id+"F2.wireOp",EDGE,"E14"),sQuery(id+"F2.wireOp",EDGE,"E15"),sQuery(id+"F2.wireOp",EDGE,"E16"),sQuery(id+"F2.wireOp",EDGE,"E17"),sQuery(id+"F2.wireOp",EDGE,"E18"),sQuery(id+"F2.wireOp",EDGE,"E19"),subQ0,sQuery(id+"F2.wireOp",EDGE,"E21"),sQuery(id+"F2.wireOp",EDGE,"E22"),sQuery(id+"F2.wireOp",EDGE,"E23"),sQuery(id+"F2.wireOp",EDGE,"E24")])],"isStart":false})]});}
            var Q111;
            {var subQ0=sQuery(id+"F2.wireOp",EDGE,"E10");Q111=makeQuery(id+"FPISK7QOFB9ojP9_2.opFillet","BLEND_EDGE",EDGE,{"blendedFrom":[makeQuery(id+"F3.opExtrude","CAP_VERTEX",VERTEX,{"disambiguationData":[OSD([subQ0,sQuery(id+"F2.wireOp",EDGE,"E19")])],"isStart":false}),makeQuery(id+"F3.opExtrude","CAP_EDGE",EDGE,{"disambiguationData":[OSD([subQ0,sQuery(id+"F2.wireOp",EDGE,"E22")])],"isStart":false})],"blendedInto":[]});}
            var Q112;
            {var subQ0=sQuery(id+"F2.wireOp",EDGE,"E21");var subQ1=sQuery(id+"F2.wireOp",EDGE,"E11");Q112=makeQuery(id+"FPISK7QOFB9ojP9_2.opFillet","BLEND_EDGE",EDGE,{"blendedFrom":[makeQuery(id+"F3.opExtrude","CAP_EDGE",EDGE,{"disambiguationData":[OSD([subQ1,subQ0])],"isStart":true}),makeQuery(id+"F3.opExtrude","CAP_FACE",FACE,{"disambiguationData":[OSD([sQuery(id+"F2.wireOp",EDGE,"E7"),sQuery(id+"F2.wireOp",EDGE,"E8"),sQuery(id+"F2.wireOp",EDGE,"E9"),sQuery(id+"F2.wireOp",EDGE,"E10"),subQ1,sQuery(id+"F2.wireOp",EDGE,"E12"),sQuery(id+"F2.wireOp",EDGE,"E13"),sQuery(id+"F2.wireOp",EDGE,"E14"),sQuery(id+"F2.wireOp",EDGE,"E15"),sQuery(id+"F2.wireOp",EDGE,"E16"),sQuery(id+"F2.wireOp",EDGE,"E17"),sQuery(id+"F2.wireOp",EDGE,"E18"),sQuery(id+"F2.wireOp",EDGE,"E19"),sQuery(id+"F2.wireOp",EDGE,"E20"),subQ0,sQuery(id+"F2.wireOp",EDGE,"E22"),sQuery(id+"F2.wireOp",EDGE,"E23"),sQuery(id+"F2.wireOp",EDGE,"E24")])],"isStart":true})],"blendedInto":[makeQuery(id+"F3.opExtrude","CAP_FACE",FACE,{"disambiguationData":[OSD([sQuery(id+"F2.wireOp",EDGE,"E7"),sQuery(id+"F2.wireOp",EDGE,"E8"),sQuery(id+"F2.wireOp",EDGE,"E9"),sQuery(id+"F2.wireOp",EDGE,"E10"),subQ1,sQuery(id+"F2.wireOp",EDGE,"E12"),sQuery(id+"F2.wireOp",EDGE,"E13"),sQuery(id+"F2.wireOp",EDGE,"E14"),sQuery(id+"F2.wireOp",EDGE,"E15"),sQuery(id+"F2.wireOp",EDGE,"E16"),sQuery(id+"F2.wireOp",EDGE,"E17"),sQuery(id+"F2.wireOp",EDGE,"E18"),sQuery(id+"F2.wireOp",EDGE,"E19"),sQuery(id+"F2.wireOp",EDGE,"E20"),subQ0,sQuery(id+"F2.wireOp",EDGE,"E22"),sQuery(id+"F2.wireOp",EDGE,"E23"),sQuery(id+"F2.wireOp",EDGE,"E24")])],"isStart":true})]});}
            var Q113;
            {var subQ0=sQuery(id+"F2.wireOp",EDGE,"E18");Q113=makeQuery(id+"FPISK7QOFB9ojP9_2.opFillet","BLEND_EDGE",EDGE,{"blendedFrom":[makeQuery(id+"F3.opExtrude","CAP_EDGE",EDGE,{"disambiguationData":[OSD([subQ0])],"isStart":true}),makeQuery(id+"F3.opExtrude","CAP_FACE",FACE,{"disambiguationData":[OSD([sQuery(id+"F2.wireOp",EDGE,"E7"),sQuery(id+"F2.wireOp",EDGE,"E8"),sQuery(id+"F2.wireOp",EDGE,"E9"),sQuery(id+"F2.wireOp",EDGE,"E10"),sQuery(id+"F2.wireOp",EDGE,"E11"),sQuery(id+"F2.wireOp",EDGE,"E12"),sQuery(id+"F2.wireOp",EDGE,"E13"),sQuery(id+"F2.wireOp",EDGE,"E14"),sQuery(id+"F2.wireOp",EDGE,"E15"),sQuery(id+"F2.wireOp",EDGE,"E16"),sQuery(id+"F2.wireOp",EDGE,"E17"),subQ0,sQuery(id+"F2.wireOp",EDGE,"E19"),sQuery(id+"F2.wireOp",EDGE,"E20"),sQuery(id+"F2.wireOp",EDGE,"E21"),sQuery(id+"F2.wireOp",EDGE,"E22"),sQuery(id+"F2.wireOp",EDGE,"E23"),sQuery(id+"F2.wireOp",EDGE,"E24")])],"isStart":true})],"blendedInto":[makeQuery(id+"F3.opExtrude","CAP_FACE",FACE,{"disambiguationData":[OSD([sQuery(id+"F2.wireOp",EDGE,"E7"),sQuery(id+"F2.wireOp",EDGE,"E8"),sQuery(id+"F2.wireOp",EDGE,"E9"),sQuery(id+"F2.wireOp",EDGE,"E10"),sQuery(id+"F2.wireOp",EDGE,"E11"),sQuery(id+"F2.wireOp",EDGE,"E12"),sQuery(id+"F2.wireOp",EDGE,"E13"),sQuery(id+"F2.wireOp",EDGE,"E14"),sQuery(id+"F2.wireOp",EDGE,"E15"),sQuery(id+"F2.wireOp",EDGE,"E16"),sQuery(id+"F2.wireOp",EDGE,"E17"),subQ0,sQuery(id+"F2.wireOp",EDGE,"E19"),sQuery(id+"F2.wireOp",EDGE,"E20"),sQuery(id+"F2.wireOp",EDGE,"E21"),sQuery(id+"F2.wireOp",EDGE,"E22"),sQuery(id+"F2.wireOp",EDGE,"E23"),sQuery(id+"F2.wireOp",EDGE,"E24")])],"isStart":true})]});}
            var Q114;
            {var subQ0=sQuery(id+"F2.wireOp",EDGE,"E15");Q114=makeQuery(id+"FPISK7QOFB9ojP9_2.opFillet","BLEND_EDGE",EDGE,{"blendedFrom":[makeQuery(id+"F3.opExtrude","CAP_VERTEX",VERTEX,{"disambiguationData":[OSD([subQ0,sQuery(id+"F2.wireOp",EDGE,"E18")])],"isStart":true}),makeQuery(id+"F3.opExtrude","CAP_EDGE",EDGE,{"disambiguationData":[OSD([subQ0])],"isStart":true})],"blendedInto":[]});}
            var Q115;
            {var subQ0=sQuery(id+"F2.wireOp",EDGE,"E23");var subQ1=sQuery(id+"F2.wireOp",EDGE,"E20");Q115=makeQuery(id+"FPISK7QOFB9ojP9_2.opFillet","BLEND_EDGE",EDGE,{"blendedFrom":[makeQuery(id+"F3.opExtrude","CAP_VERTEX",VERTEX,{"disambiguationData":[OSD([subQ1,subQ0])],"isStart":false}),makeQuery(id+"F3.opExtrude","CAP_FACE",FACE,{"disambiguationData":[OSD([sQuery(id+"F2.wireOp",EDGE,"E7"),sQuery(id+"F2.wireOp",EDGE,"E8"),sQuery(id+"F2.wireOp",EDGE,"E9"),sQuery(id+"F2.wireOp",EDGE,"E10"),sQuery(id+"F2.wireOp",EDGE,"E11"),sQuery(id+"F2.wireOp",EDGE,"E12"),sQuery(id+"F2.wireOp",EDGE,"E13"),sQuery(id+"F2.wireOp",EDGE,"E14"),sQuery(id+"F2.wireOp",EDGE,"E15"),sQuery(id+"F2.wireOp",EDGE,"E16"),sQuery(id+"F2.wireOp",EDGE,"E17"),sQuery(id+"F2.wireOp",EDGE,"E18"),sQuery(id+"F2.wireOp",EDGE,"E19"),subQ1,sQuery(id+"F2.wireOp",EDGE,"E21"),sQuery(id+"F2.wireOp",EDGE,"E22"),subQ0,sQuery(id+"F2.wireOp",EDGE,"E24")])],"isStart":false})],"blendedInto":[makeQuery(id+"F3.opExtrude","CAP_FACE",FACE,{"disambiguationData":[OSD([sQuery(id+"F2.wireOp",EDGE,"E7"),sQuery(id+"F2.wireOp",EDGE,"E8"),sQuery(id+"F2.wireOp",EDGE,"E9"),sQuery(id+"F2.wireOp",EDGE,"E10"),sQuery(id+"F2.wireOp",EDGE,"E11"),sQuery(id+"F2.wireOp",EDGE,"E12"),sQuery(id+"F2.wireOp",EDGE,"E13"),sQuery(id+"F2.wireOp",EDGE,"E14"),sQuery(id+"F2.wireOp",EDGE,"E15"),sQuery(id+"F2.wireOp",EDGE,"E16"),sQuery(id+"F2.wireOp",EDGE,"E17"),sQuery(id+"F2.wireOp",EDGE,"E18"),sQuery(id+"F2.wireOp",EDGE,"E19"),subQ1,sQuery(id+"F2.wireOp",EDGE,"E21"),sQuery(id+"F2.wireOp",EDGE,"E22"),subQ0,sQuery(id+"F2.wireOp",EDGE,"E24")])],"isStart":false})]});}
            var Q116;
            {var subQ0=sQuery(id+"F2.wireOp",EDGE,"E24");Q116=makeQuery(id+"FPISK7QOFB9ojP9_2.opFillet","BLEND_EDGE",EDGE,{"blendedFrom":[makeQuery(id+"F3.opExtrude","CAP_VERTEX",VERTEX,{"disambiguationData":[OSD([sQuery(id+"F2.wireOp",EDGE,"E23"),subQ0])],"isStart":false}),makeQuery(id+"F3.opExtrude","CAP_EDGE",EDGE,{"disambiguationData":[OSD([subQ0])],"isStart":false})],"blendedInto":[]});}
            var Q117;
            {var subQ0=sQuery(id+"F2.wireOp",EDGE,"E24");var subQ1=sQuery(id+"F2.wireOp",EDGE,"E11");Q117=makeQuery(id+"FPISK7QOFB9ojP9_2.opFillet","BLEND_EDGE",EDGE,{"blendedFrom":[makeQuery(id+"F3.opExtrude","CAP_VERTEX",VERTEX,{"disambiguationData":[OSD([subQ1,subQ0])],"isStart":true}),makeQuery(id+"F3.opExtrude","SWEPT_EDGE",EDGE,{"disambiguationData":[OSD([subQ1,subQ0])]})],"blendedInto":[]});}
            var Q118;
            {var subQ0=sQuery(id+"F2.wireOp",EDGE,"E20");Q118=makeQuery(id+"FPISK7QOFB9ojP9_2.opFillet","BLEND_EDGE",EDGE,{"blendedFrom":[makeQuery(id+"F3.opExtrude","CAP_EDGE",EDGE,{"disambiguationData":[OSD([subQ0])],"isStart":false}),makeQuery(id+"F3.opExtrude","SWEPT_FACE",FACE,{"disambiguationData":[OSD([subQ0])]})],"blendedInto":[makeQuery(id+"F3.opExtrude","SWEPT_FACE",FACE,{"disambiguationData":[OSD([subQ0])]})]});}
            var Q119;
            {var subQ0=sQuery(id+"F2.wireOp",EDGE,"E18");var subQ1=sQuery(id+"F2.wireOp",EDGE,"E15");Q119=makeQuery(id+"FPISK7QOFB9ojP9_2.opFillet","BLEND_EDGE",EDGE,{"blendedFrom":[makeQuery(id+"F3.opExtrude","CAP_VERTEX",VERTEX,{"disambiguationData":[OSD([subQ1,subQ0])],"isStart":false}),makeQuery(id+"F3.opExtrude","CAP_FACE",FACE,{"disambiguationData":[OSD([sQuery(id+"F2.wireOp",EDGE,"E7"),sQuery(id+"F2.wireOp",EDGE,"E8"),sQuery(id+"F2.wireOp",EDGE,"E9"),sQuery(id+"F2.wireOp",EDGE,"E10"),sQuery(id+"F2.wireOp",EDGE,"E11"),sQuery(id+"F2.wireOp",EDGE,"E12"),sQuery(id+"F2.wireOp",EDGE,"E13"),sQuery(id+"F2.wireOp",EDGE,"E14"),subQ1,sQuery(id+"F2.wireOp",EDGE,"E16"),sQuery(id+"F2.wireOp",EDGE,"E17"),subQ0,sQuery(id+"F2.wireOp",EDGE,"E19"),sQuery(id+"F2.wireOp",EDGE,"E20"),sQuery(id+"F2.wireOp",EDGE,"E21"),sQuery(id+"F2.wireOp",EDGE,"E22"),sQuery(id+"F2.wireOp",EDGE,"E23"),sQuery(id+"F2.wireOp",EDGE,"E24")])],"isStart":false})],"blendedInto":[makeQuery(id+"F3.opExtrude","CAP_FACE",FACE,{"disambiguationData":[OSD([sQuery(id+"F2.wireOp",EDGE,"E7"),sQuery(id+"F2.wireOp",EDGE,"E8"),sQuery(id+"F2.wireOp",EDGE,"E9"),sQuery(id+"F2.wireOp",EDGE,"E10"),sQuery(id+"F2.wireOp",EDGE,"E11"),sQuery(id+"F2.wireOp",EDGE,"E12"),sQuery(id+"F2.wireOp",EDGE,"E13"),sQuery(id+"F2.wireOp",EDGE,"E14"),subQ1,sQuery(id+"F2.wireOp",EDGE,"E16"),sQuery(id+"F2.wireOp",EDGE,"E17"),subQ0,sQuery(id+"F2.wireOp",EDGE,"E19"),sQuery(id+"F2.wireOp",EDGE,"E20"),sQuery(id+"F2.wireOp",EDGE,"E21"),sQuery(id+"F2.wireOp",EDGE,"E22"),sQuery(id+"F2.wireOp",EDGE,"E23"),sQuery(id+"F2.wireOp",EDGE,"E24")])],"isStart":false})]});}
            var Q120;
            {var subQ0=sQuery(id+"F2.wireOp",EDGE,"E20");Q120=makeQuery(id+"FPISK7QOFB9ojP9_2.opFillet","BLEND_EDGE",EDGE,{"blendedFrom":[makeQuery(id+"F3.opExtrude","CAP_VERTEX",VERTEX,{"disambiguationData":[OSD([sQuery(id+"F2.wireOp",EDGE,"E18"),subQ0])],"isStart":false}),makeQuery(id+"F3.opExtrude","CAP_EDGE",EDGE,{"disambiguationData":[OSD([subQ0])],"isStart":false})],"blendedInto":[]});}
            var Q121;
            {var subQ0=sQuery(id+"F2.wireOp",EDGE,"E11");Q121=makeQuery(id+"FPISK7QOFB9ojP9_2.opFillet","BLEND_EDGE",EDGE,{"blendedFrom":[makeQuery(id+"F3.opExtrude","CAP_VERTEX",VERTEX,{"disambiguationData":[OSD([subQ0,sQuery(id+"F2.wireOp",EDGE,"E24")])],"isStart":false}),makeQuery(id+"F3.opExtrude","CAP_EDGE",EDGE,{"disambiguationData":[OSD([subQ0,sQuery(id+"F2.wireOp",EDGE,"E21")])],"isStart":false})],"blendedInto":[]});}
            var Q122;
            {var subQ0=sQuery(id+"F2.wireOp",EDGE,"E17");var subQ1=sQuery(id+"F2.wireOp",EDGE,"E8");Q122=makeQuery(id+"FPISK7QOFB9ojP9_2.opFillet","BLEND_EDGE",EDGE,{"blendedFrom":[makeQuery(id+"F3.opExtrude","CAP_EDGE",EDGE,{"disambiguationData":[OSD([subQ1,subQ0])],"isStart":false}),makeQuery(id+"F3.opExtrude","SWEPT_FACE",FACE,{"disambiguationData":[OSD([subQ1,subQ0])]})],"blendedInto":[makeQuery(id+"F3.opExtrude","SWEPT_FACE",FACE,{"disambiguationData":[OSD([subQ1,subQ0])]})]});}
            var Q123;
            {var subQ0=sQuery(id+"F2.wireOp",EDGE,"E24");Q123=makeQuery(id+"FPISK7QOFB9ojP9_2.opFillet","BLEND_EDGE",EDGE,{"blendedFrom":[makeQuery(id+"F3.opExtrude","SWEPT_EDGE",EDGE,{"disambiguationData":[OSD([sQuery(id+"F2.wireOp",EDGE,"E23"),subQ0])]}),makeQuery(id+"F3.opExtrude","SWEPT_FACE",FACE,{"disambiguationData":[OSD([subQ0])]})],"blendedInto":[makeQuery(id+"F3.opExtrude","SWEPT_FACE",FACE,{"disambiguationData":[OSD([subQ0])]})]});}
            var Q124;
            {var subQ0=sQuery(id+"F2.wireOp",EDGE,"E18");Q124=makeQuery(id+"FPISK7QOFB9ojP9_2.opFillet","BLEND_EDGE",EDGE,{"blendedFrom":[makeQuery(id+"F3.opExtrude","CAP_VERTEX",VERTEX,{"disambiguationData":[OSD([sQuery(id+"F2.wireOp",EDGE,"E15"),subQ0])],"isStart":true}),makeQuery(id+"F3.opExtrude","CAP_EDGE",EDGE,{"disambiguationData":[OSD([subQ0])],"isStart":true})],"blendedInto":[]});}
            var Q125;
            {var subQ0=sQuery(id+"F2.wireOp",EDGE,"E13");Q125=makeQuery(id+"FPISK7QOFB9ojP9_2.opFillet","BLEND_EDGE",EDGE,{"blendedFrom":[makeQuery(id+"F3.opExtrude","CAP_EDGE",EDGE,{"disambiguationData":[OSD([subQ0])],"isStart":false}),makeQuery(id+"F3.opExtrude","SWEPT_FACE",FACE,{"disambiguationData":[OSD([subQ0])]})],"blendedInto":[makeQuery(id+"F3.opExtrude","SWEPT_FACE",FACE,{"disambiguationData":[OSD([subQ0])]})]});}
            var Q126;
            {var subQ0=sQuery(id+"F2.wireOp",EDGE,"E23");var subQ1=sQuery(id+"F2.wireOp",EDGE,"E20");Q126=makeQuery(id+"FPISK7QOFB9ojP9_2.opFillet","BLEND_FACE",FACE,{"disambiguationData":[OSD([subQ1,subQ0]),TDD([makeQuery(id+"F3.opExtrude","CAP_VERTEX",VERTEX,{"disambiguationData":[OSD([subQ1,subQ0])],"isStart":true})])]});}
            var Q127;
            {var subQ0=sQuery(id+"F2.wireOp",EDGE,"E10");Q127=makeQuery(id+"FPISK7QOFB9ojP9_2.opFillet","BLEND_EDGE",EDGE,{"blendedFrom":[makeQuery(id+"F3.opExtrude","CAP_VERTEX",VERTEX,{"disambiguationData":[OSD([subQ0,sQuery(id+"F2.wireOp",EDGE,"E19")])],"isStart":true}),makeQuery(id+"F3.opExtrude","CAP_EDGE",EDGE,{"disambiguationData":[OSD([subQ0,sQuery(id+"F2.wireOp",EDGE,"E22")])],"isStart":true})],"blendedInto":[]});}
            var Q128;
            {var subQ0=sQuery(id+"F2.wireOp",EDGE,"E24");var subQ1=sQuery(id+"F2.wireOp",EDGE,"E23");Q128=makeQuery(id+"FPISK7QOFB9ojP9_2.opFillet","BLEND_FACE",FACE,{"disambiguationData":[OSD([subQ1,subQ0]),TDD([makeQuery(id+"F3.opExtrude","CAP_VERTEX",VERTEX,{"disambiguationData":[OSD([subQ1,subQ0])],"isStart":true})])]});}
            var Q129;
            {var subQ0=sQuery(id+"F2.wireOp",EDGE,"E19");var subQ1=sQuery(id+"F2.wireOp",EDGE,"E10");Q129=makeQuery(id+"FPISK7QOFB9ojP9_2.opFillet","BLEND_EDGE",EDGE,{"blendedFrom":[makeQuery(id+"F3.opExtrude","CAP_VERTEX",VERTEX,{"disambiguationData":[OSD([subQ1,subQ0])],"isStart":false}),makeQuery(id+"F3.opExtrude","SWEPT_EDGE",EDGE,{"disambiguationData":[OSD([subQ1,subQ0])]})],"blendedInto":[]});}
            var Q130;
            {var subQ0=sQuery(id+"F2.wireOp",EDGE,"E24");Q130=makeQuery(id+"FPISK7QOFB9ojP9_2.opFillet","BLEND_FACE",FACE,{"disambiguationData":[OSD([subQ0]),TDD([makeQuery(id+"F3.opExtrude","CAP_EDGE",EDGE,{"disambiguationData":[OSD([subQ0])],"isStart":true})])]});}
            var Q131;
            {var subQ0=sQuery(id+"F2.wireOp",EDGE,"E12");var subQ1=sQuery(id+"F2.wireOp",EDGE,"E7");Q131=makeQuery(id+"FPISK7QOFB9ojP9_2.opFillet","BLEND_EDGE",EDGE,{"blendedFrom":[makeQuery(id+"F3.opExtrude","CAP_VERTEX",VERTEX,{"disambiguationData":[OSD([subQ1,subQ0])],"isStart":true}),makeQuery(id+"F3.opExtrude","SWEPT_EDGE",EDGE,{"disambiguationData":[OSD([subQ1,subQ0])]})],"blendedInto":[]});}
            var Q132;
            {var subQ0=sQuery(id+"F2.wireOp",EDGE,"E19");Q132=makeQuery(id+"FPISK7QOFB9ojP9_2.opFillet","BLEND_EDGE",EDGE,{"blendedFrom":[makeQuery(id+"F3.opExtrude","CAP_VERTEX",VERTEX,{"disambiguationData":[OSD([sQuery(id+"F2.wireOp",EDGE,"E10"),subQ0])],"isStart":false}),makeQuery(id+"F3.opExtrude","CAP_EDGE",EDGE,{"disambiguationData":[OSD([sQuery(id+"F2.wireOp",EDGE,"E9"),sQuery(id+"F2.wireOp",EDGE,"E16"),subQ0])],"isStart":false})],"blendedInto":[]});}
            var Q133;
            {var subQ0=sQuery(id+"F2.wireOp",EDGE,"E19");var subQ1=sQuery(id+"F2.wireOp",EDGE,"E16");var subQ2=sQuery(id+"F2.wireOp",EDGE,"E9");Q133=makeQuery(id+"FPISK7QOFB9ojP9_2.opFillet","BLEND_EDGE",EDGE,{"blendedFrom":[makeQuery(id+"F3.opExtrude","CAP_EDGE",EDGE,{"disambiguationData":[OSD([subQ2,subQ1,subQ0])],"isStart":true}),makeQuery(id+"F3.opExtrude","CAP_FACE",FACE,{"disambiguationData":[OSD([sQuery(id+"F2.wireOp",EDGE,"E7"),sQuery(id+"F2.wireOp",EDGE,"E8"),subQ2,sQuery(id+"F2.wireOp",EDGE,"E10"),sQuery(id+"F2.wireOp",EDGE,"E11"),sQuery(id+"F2.wireOp",EDGE,"E12"),sQuery(id+"F2.wireOp",EDGE,"E13"),sQuery(id+"F2.wireOp",EDGE,"E14"),sQuery(id+"F2.wireOp",EDGE,"E15"),subQ1,sQuery(id+"F2.wireOp",EDGE,"E17"),sQuery(id+"F2.wireOp",EDGE,"E18"),subQ0,sQuery(id+"F2.wireOp",EDGE,"E20"),sQuery(id+"F2.wireOp",EDGE,"E21"),sQuery(id+"F2.wireOp",EDGE,"E22"),sQuery(id+"F2.wireOp",EDGE,"E23"),sQuery(id+"F2.wireOp",EDGE,"E24")])],"isStart":true})],"blendedInto":[makeQuery(id+"F3.opExtrude","CAP_FACE",FACE,{"disambiguationData":[OSD([sQuery(id+"F2.wireOp",EDGE,"E7"),sQuery(id+"F2.wireOp",EDGE,"E8"),subQ2,sQuery(id+"F2.wireOp",EDGE,"E10"),sQuery(id+"F2.wireOp",EDGE,"E11"),sQuery(id+"F2.wireOp",EDGE,"E12"),sQuery(id+"F2.wireOp",EDGE,"E13"),sQuery(id+"F2.wireOp",EDGE,"E14"),sQuery(id+"F2.wireOp",EDGE,"E15"),subQ1,sQuery(id+"F2.wireOp",EDGE,"E17"),sQuery(id+"F2.wireOp",EDGE,"E18"),subQ0,sQuery(id+"F2.wireOp",EDGE,"E20"),sQuery(id+"F2.wireOp",EDGE,"E21"),sQuery(id+"F2.wireOp",EDGE,"E22"),sQuery(id+"F2.wireOp",EDGE,"E23"),sQuery(id+"F2.wireOp",EDGE,"E24")])],"isStart":true})]});}
            var Q134;
            {var subQ0=sQuery(id+"F2.wireOp",EDGE,"E16");Q134=makeQuery(id+"FPISK7QOFB9ojP9_2.opFillet","BLEND_EDGE",EDGE,{"blendedFrom":[makeQuery(id+"F3.opExtrude","SWEPT_EDGE",EDGE,{"disambiguationData":[OSD([subQ0,sQuery(id+"F2.wireOp",EDGE,"E17")])]}),makeQuery(id+"F3.opExtrude","SWEPT_FACE",FACE,{"disambiguationData":[OSD([sQuery(id+"F2.wireOp",EDGE,"E9"),subQ0,sQuery(id+"F2.wireOp",EDGE,"E19")])]})],"blendedInto":[makeQuery(id+"F3.opExtrude","SWEPT_FACE",FACE,{"disambiguationData":[OSD([sQuery(id+"F2.wireOp",EDGE,"E9"),subQ0,sQuery(id+"F2.wireOp",EDGE,"E19")])]})]});}
            var Q135;
            {var subQ0=sQuery(id+"F2.wireOp",EDGE,"E20");var subQ1=sQuery(id+"F2.wireOp",EDGE,"E18");Q135=makeQuery(id+"FPISK7QOFB9ojP9_2.opFillet","BLEND_FACE",FACE,{"disambiguationData":[OSD([subQ1,subQ0]),TDD([makeQuery(id+"F3.opExtrude","CAP_VERTEX",VERTEX,{"disambiguationData":[OSD([subQ1,subQ0])],"isStart":true})])]});}
            var Q136;
            {var subQ0=sQuery(id+"F2.wireOp",EDGE,"E12");Q136=makeQuery(id+"FPISK7QOFB9ojP9_2.opFillet","BLEND_EDGE",EDGE,{"blendedFrom":[makeQuery(id+"F3.opExtrude","CAP_VERTEX",VERTEX,{"disambiguationData":[OSD([sQuery(id+"F2.wireOp",EDGE,"E7"),subQ0])],"isStart":false}),makeQuery(id+"F3.opExtrude","CAP_EDGE",EDGE,{"disambiguationData":[OSD([subQ0])],"isStart":false})],"blendedInto":[]});}
            var Q137;
            {var subQ0=sQuery(id+"F2.wireOp",EDGE,"E21");var subQ1=sQuery(id+"F2.wireOp",EDGE,"E11");Q137=makeQuery(id+"FPISK7QOFB9ojP9_2.opFillet","BLEND_EDGE",EDGE,{"blendedFrom":[makeQuery(id+"F3.opExtrude","CAP_EDGE",EDGE,{"disambiguationData":[OSD([subQ1,subQ0])],"isStart":false}),makeQuery(id+"F3.opExtrude","SWEPT_FACE",FACE,{"disambiguationData":[OSD([subQ1,subQ0])]})],"blendedInto":[makeQuery(id+"F3.opExtrude","SWEPT_FACE",FACE,{"disambiguationData":[OSD([subQ1,subQ0])]})]});}
            var Q138;
            {var subQ0=sQuery(id+"F2.wireOp",EDGE,"E14");var subQ1=sQuery(id+"F2.wireOp",EDGE,"E7");Q138=makeQuery(id+"FPISK7QOFB9ojP9_2.opFillet","BLEND_EDGE",EDGE,{"blendedFrom":[makeQuery(id+"F3.opExtrude","CAP_EDGE",EDGE,{"disambiguationData":[OSD([subQ1,subQ0])],"isStart":false}),makeQuery(id+"F3.opExtrude","SWEPT_FACE",FACE,{"disambiguationData":[OSD([subQ1,subQ0])]})],"blendedInto":[makeQuery(id+"F3.opExtrude","SWEPT_FACE",FACE,{"disambiguationData":[OSD([subQ1,subQ0])]})]});}
            var Q139;
            {var subQ0=sQuery(id+"F2.wireOp",EDGE,"E14");var subQ1=sQuery(id+"F2.wireOp",EDGE,"E8");Q139=makeQuery(id+"FPISK7QOFB9ojP9_2.opFillet","BLEND_EDGE",EDGE,{"blendedFrom":[makeQuery(id+"F3.opExtrude","CAP_VERTEX",VERTEX,{"disambiguationData":[OSD([subQ1,subQ0])],"isStart":true}),makeQuery(id+"F3.opExtrude","SWEPT_EDGE",EDGE,{"disambiguationData":[OSD([subQ1,subQ0])]})],"blendedInto":[]});}
            var Q140;
            {var subQ0=sQuery(id+"F2.wireOp",EDGE,"E17");var subQ1=sQuery(id+"F2.wireOp",EDGE,"E16");Q140=makeQuery(id+"FPISK7QOFB9ojP9_2.opFillet","BLEND_FACE",FACE,{"disambiguationData":[OSD([subQ1,subQ0]),TDD([makeQuery(id+"F3.opExtrude","CAP_VERTEX",VERTEX,{"disambiguationData":[OSD([subQ1,subQ0])],"isStart":true})])]});}
            var Q141;
            {var subQ0=sQuery(id+"F2.wireOp",EDGE,"E22");var subQ1=sQuery(id+"F2.wireOp",EDGE,"E21");Q141=makeQuery(id+"FPISK7QOFB9ojP9_2.opFillet","BLEND_EDGE",EDGE,{"blendedFrom":[makeQuery(id+"F3.opExtrude","CAP_VERTEX",VERTEX,{"disambiguationData":[OSD([subQ1,subQ0])],"isStart":true}),makeQuery(id+"F3.opExtrude","SWEPT_EDGE",EDGE,{"disambiguationData":[OSD([subQ1,subQ0])]})],"blendedInto":[]});}
            var Q142;
            {var subQ0=sQuery(id+"F2.wireOp",EDGE,"E13");Q142=makeQuery(id+"FPISK7QOFB9ojP9_2.opFillet","BLEND_EDGE",EDGE,{"blendedFrom":[makeQuery(id+"F3.opExtrude","CAP_VERTEX",VERTEX,{"disambiguationData":[OSD([sQuery(id+"F2.wireOp",EDGE,"E12"),subQ0])],"isStart":false}),makeQuery(id+"F3.opExtrude","CAP_EDGE",EDGE,{"disambiguationData":[OSD([subQ0])],"isStart":false})],"blendedInto":[]});}
            var Q143;
            {var subQ0=sQuery(id+"F2.wireOp",EDGE,"E8");Q143=makeQuery(id+"FPISK7QOFB9ojP9_2.opFillet","BLEND_EDGE",EDGE,{"blendedFrom":[makeQuery(id+"F3.opExtrude","CAP_VERTEX",VERTEX,{"disambiguationData":[OSD([subQ0,sQuery(id+"F2.wireOp",EDGE,"E14")])],"isStart":false}),makeQuery(id+"F3.opExtrude","CAP_EDGE",EDGE,{"disambiguationData":[OSD([subQ0,sQuery(id+"F2.wireOp",EDGE,"E17")])],"isStart":false})],"blendedInto":[]});}
            var Q144;
            {var subQ0=sQuery(id+"F2.wireOp",EDGE,"E17");var subQ1=sQuery(id+"F2.wireOp",EDGE,"E8");Q144=makeQuery(id+"FPISK7QOFB9ojP9_2.opFillet","BLEND_EDGE",EDGE,{"blendedFrom":[makeQuery(id+"F3.opExtrude","CAP_EDGE",EDGE,{"disambiguationData":[OSD([subQ1,subQ0])],"isStart":true}),makeQuery(id+"F3.opExtrude","SWEPT_FACE",FACE,{"disambiguationData":[OSD([subQ1,subQ0])]})],"blendedInto":[makeQuery(id+"F3.opExtrude","SWEPT_FACE",FACE,{"disambiguationData":[OSD([subQ1,subQ0])]})]});}
            var Q145;
            {var subQ0=sQuery(id+"F2.wireOp",EDGE,"E22");var subQ1=sQuery(id+"F2.wireOp",EDGE,"E10");Q145=makeQuery(id+"FPISK7QOFB9ojP9_2.opFillet","BLEND_EDGE",EDGE,{"blendedFrom":[makeQuery(id+"F3.opExtrude","CAP_EDGE",EDGE,{"disambiguationData":[OSD([subQ1,subQ0])],"isStart":true}),makeQuery(id+"F3.opExtrude","CAP_FACE",FACE,{"disambiguationData":[OSD([sQuery(id+"F2.wireOp",EDGE,"E7"),sQuery(id+"F2.wireOp",EDGE,"E8"),sQuery(id+"F2.wireOp",EDGE,"E9"),subQ1,sQuery(id+"F2.wireOp",EDGE,"E11"),sQuery(id+"F2.wireOp",EDGE,"E12"),sQuery(id+"F2.wireOp",EDGE,"E13"),sQuery(id+"F2.wireOp",EDGE,"E14"),sQuery(id+"F2.wireOp",EDGE,"E15"),sQuery(id+"F2.wireOp",EDGE,"E16"),sQuery(id+"F2.wireOp",EDGE,"E17"),sQuery(id+"F2.wireOp",EDGE,"E18"),sQuery(id+"F2.wireOp",EDGE,"E19"),sQuery(id+"F2.wireOp",EDGE,"E20"),sQuery(id+"F2.wireOp",EDGE,"E21"),subQ0,sQuery(id+"F2.wireOp",EDGE,"E23"),sQuery(id+"F2.wireOp",EDGE,"E24")])],"isStart":true})],"blendedInto":[makeQuery(id+"F3.opExtrude","CAP_FACE",FACE,{"disambiguationData":[OSD([sQuery(id+"F2.wireOp",EDGE,"E7"),sQuery(id+"F2.wireOp",EDGE,"E8"),sQuery(id+"F2.wireOp",EDGE,"E9"),subQ1,sQuery(id+"F2.wireOp",EDGE,"E11"),sQuery(id+"F2.wireOp",EDGE,"E12"),sQuery(id+"F2.wireOp",EDGE,"E13"),sQuery(id+"F2.wireOp",EDGE,"E14"),sQuery(id+"F2.wireOp",EDGE,"E15"),sQuery(id+"F2.wireOp",EDGE,"E16"),sQuery(id+"F2.wireOp",EDGE,"E17"),sQuery(id+"F2.wireOp",EDGE,"E18"),sQuery(id+"F2.wireOp",EDGE,"E19"),sQuery(id+"F2.wireOp",EDGE,"E20"),sQuery(id+"F2.wireOp",EDGE,"E21"),subQ0,sQuery(id+"F2.wireOp",EDGE,"E23"),sQuery(id+"F2.wireOp",EDGE,"E24")])],"isStart":true})]});}
            var Q146;
            {var subQ0=sQuery(id+"F2.wireOp",EDGE,"E18");Q146=makeQuery(id+"FPISK7QOFB9ojP9_2.opFillet","BLEND_EDGE",EDGE,{"blendedFrom":[makeQuery(id+"F3.opExtrude","SWEPT_EDGE",EDGE,{"disambiguationData":[OSD([subQ0,sQuery(id+"F2.wireOp",EDGE,"E20")])]}),makeQuery(id+"F3.opExtrude","SWEPT_FACE",FACE,{"disambiguationData":[OSD([subQ0])]})],"blendedInto":[makeQuery(id+"F3.opExtrude","SWEPT_FACE",FACE,{"disambiguationData":[OSD([subQ0])]})]});}
            var Q147;
            {var subQ0=sQuery(id+"F2.wireOp",EDGE,"E15");Q147=makeQuery(id+"FPISK7QOFB9ojP9_2.opFillet","BLEND_EDGE",EDGE,{"blendedFrom":[makeQuery(id+"F3.opExtrude","CAP_VERTEX",VERTEX,{"disambiguationData":[OSD([subQ0,sQuery(id+"F2.wireOp",EDGE,"E18")])],"isStart":false}),makeQuery(id+"F3.opExtrude","CAP_EDGE",EDGE,{"disambiguationData":[OSD([subQ0])],"isStart":false})],"blendedInto":[]});}
            var Q148;
            {var subQ0=sQuery(id+"F2.wireOp",EDGE,"E19");var subQ1=sQuery(id+"F2.wireOp",EDGE,"E10");Q148=makeQuery(id+"FPISK7QOFB9ojP9_2.opFillet","BLEND_EDGE",EDGE,{"blendedFrom":[makeQuery(id+"F3.opExtrude","CAP_VERTEX",VERTEX,{"disambiguationData":[OSD([subQ1,subQ0])],"isStart":true}),makeQuery(id+"F3.opExtrude","SWEPT_EDGE",EDGE,{"disambiguationData":[OSD([subQ1,subQ0])]})],"blendedInto":[]});}
            var Q149;
            {var subQ0=sQuery(id+"F2.wireOp",EDGE,"E20");Q149=makeQuery(id+"FPISK7QOFB9ojP9_2.opFillet","BLEND_EDGE",EDGE,{"blendedFrom":[makeQuery(id+"F3.opExtrude","CAP_EDGE",EDGE,{"disambiguationData":[OSD([subQ0])],"isStart":true}),makeQuery(id+"F3.opExtrude","SWEPT_FACE",FACE,{"disambiguationData":[OSD([subQ0])]})],"blendedInto":[makeQuery(id+"F3.opExtrude","SWEPT_FACE",FACE,{"disambiguationData":[OSD([subQ0])]})]});}
            var Q150;
            {var subQ0=sQuery(id+"F2.wireOp",EDGE,"E20");var subQ1=sQuery(id+"F2.wireOp",EDGE,"E18");Q150=makeQuery(id+"FPISK7QOFB9ojP9_2.opFillet","BLEND_EDGE",EDGE,{"blendedFrom":[makeQuery(id+"F3.opExtrude","CAP_VERTEX",VERTEX,{"disambiguationData":[OSD([subQ1,subQ0])],"isStart":false}),makeQuery(id+"F3.opExtrude","CAP_FACE",FACE,{"disambiguationData":[OSD([sQuery(id+"F2.wireOp",EDGE,"E7"),sQuery(id+"F2.wireOp",EDGE,"E8"),sQuery(id+"F2.wireOp",EDGE,"E9"),sQuery(id+"F2.wireOp",EDGE,"E10"),sQuery(id+"F2.wireOp",EDGE,"E11"),sQuery(id+"F2.wireOp",EDGE,"E12"),sQuery(id+"F2.wireOp",EDGE,"E13"),sQuery(id+"F2.wireOp",EDGE,"E14"),sQuery(id+"F2.wireOp",EDGE,"E15"),sQuery(id+"F2.wireOp",EDGE,"E16"),sQuery(id+"F2.wireOp",EDGE,"E17"),subQ1,sQuery(id+"F2.wireOp",EDGE,"E19"),subQ0,sQuery(id+"F2.wireOp",EDGE,"E21"),sQuery(id+"F2.wireOp",EDGE,"E22"),sQuery(id+"F2.wireOp",EDGE,"E23"),sQuery(id+"F2.wireOp",EDGE,"E24")])],"isStart":false})],"blendedInto":[makeQuery(id+"F3.opExtrude","CAP_FACE",FACE,{"disambiguationData":[OSD([sQuery(id+"F2.wireOp",EDGE,"E7"),sQuery(id+"F2.wireOp",EDGE,"E8"),sQuery(id+"F2.wireOp",EDGE,"E9"),sQuery(id+"F2.wireOp",EDGE,"E10"),sQuery(id+"F2.wireOp",EDGE,"E11"),sQuery(id+"F2.wireOp",EDGE,"E12"),sQuery(id+"F2.wireOp",EDGE,"E13"),sQuery(id+"F2.wireOp",EDGE,"E14"),sQuery(id+"F2.wireOp",EDGE,"E15"),sQuery(id+"F2.wireOp",EDGE,"E16"),sQuery(id+"F2.wireOp",EDGE,"E17"),subQ1,sQuery(id+"F2.wireOp",EDGE,"E19"),subQ0,sQuery(id+"F2.wireOp",EDGE,"E21"),sQuery(id+"F2.wireOp",EDGE,"E22"),sQuery(id+"F2.wireOp",EDGE,"E23"),sQuery(id+"F2.wireOp",EDGE,"E24")])],"isStart":false})]});}
            var Q151;
            {var subQ0=sQuery(id+"F2.wireOp",EDGE,"E15");var subQ1=sQuery(id+"F2.wireOp",EDGE,"E13");Q151=makeQuery(id+"FPISK7QOFB9ojP9_2.opFillet","BLEND_EDGE",EDGE,{"blendedFrom":[makeQuery(id+"F3.opExtrude","CAP_VERTEX",VERTEX,{"disambiguationData":[OSD([subQ1,subQ0])],"isStart":false}),makeQuery(id+"F3.opExtrude","CAP_FACE",FACE,{"disambiguationData":[OSD([sQuery(id+"F2.wireOp",EDGE,"E7"),sQuery(id+"F2.wireOp",EDGE,"E8"),sQuery(id+"F2.wireOp",EDGE,"E9"),sQuery(id+"F2.wireOp",EDGE,"E10"),sQuery(id+"F2.wireOp",EDGE,"E11"),sQuery(id+"F2.wireOp",EDGE,"E12"),subQ1,sQuery(id+"F2.wireOp",EDGE,"E14"),subQ0,sQuery(id+"F2.wireOp",EDGE,"E16"),sQuery(id+"F2.wireOp",EDGE,"E17"),sQuery(id+"F2.wireOp",EDGE,"E18"),sQuery(id+"F2.wireOp",EDGE,"E19"),sQuery(id+"F2.wireOp",EDGE,"E20"),sQuery(id+"F2.wireOp",EDGE,"E21"),sQuery(id+"F2.wireOp",EDGE,"E22"),sQuery(id+"F2.wireOp",EDGE,"E23"),sQuery(id+"F2.wireOp",EDGE,"E24")])],"isStart":false})],"blendedInto":[makeQuery(id+"F3.opExtrude","CAP_FACE",FACE,{"disambiguationData":[OSD([sQuery(id+"F2.wireOp",EDGE,"E7"),sQuery(id+"F2.wireOp",EDGE,"E8"),sQuery(id+"F2.wireOp",EDGE,"E9"),sQuery(id+"F2.wireOp",EDGE,"E10"),sQuery(id+"F2.wireOp",EDGE,"E11"),sQuery(id+"F2.wireOp",EDGE,"E12"),subQ1,sQuery(id+"F2.wireOp",EDGE,"E14"),subQ0,sQuery(id+"F2.wireOp",EDGE,"E16"),sQuery(id+"F2.wireOp",EDGE,"E17"),sQuery(id+"F2.wireOp",EDGE,"E18"),sQuery(id+"F2.wireOp",EDGE,"E19"),sQuery(id+"F2.wireOp",EDGE,"E20"),sQuery(id+"F2.wireOp",EDGE,"E21"),sQuery(id+"F2.wireOp",EDGE,"E22"),sQuery(id+"F2.wireOp",EDGE,"E23"),sQuery(id+"F2.wireOp",EDGE,"E24")])],"isStart":false})]});}
            var Q152;
            {var subQ0=sQuery(id+"F2.wireOp",EDGE,"E15");var subQ1=sQuery(id+"F2.wireOp",EDGE,"E13");Q152=makeQuery(id+"FPISK7QOFB9ojP9_2.opFillet","BLEND_FACE",FACE,{"disambiguationData":[OSD([subQ1,subQ0]),TDD([makeQuery(id+"F3.opExtrude","CAP_VERTEX",VERTEX,{"disambiguationData":[OSD([subQ1,subQ0])],"isStart":true})])]});}
            var Q153;
            {var subQ0=sQuery(id+"F2.wireOp",EDGE,"E19");var subQ1=sQuery(id+"F2.wireOp",EDGE,"E16");var subQ2=sQuery(id+"F2.wireOp",EDGE,"E9");Q153=makeQuery(id+"FPISK7QOFB9ojP9_2.opFillet","BLEND_EDGE",EDGE,{"blendedFrom":[makeQuery(id+"F3.opExtrude","CAP_EDGE",EDGE,{"disambiguationData":[OSD([subQ2,subQ1,subQ0])],"isStart":true}),makeQuery(id+"F3.opExtrude","SWEPT_FACE",FACE,{"disambiguationData":[OSD([subQ2,subQ1,subQ0])]})],"blendedInto":[makeQuery(id+"F3.opExtrude","SWEPT_FACE",FACE,{"disambiguationData":[OSD([subQ2,subQ1,subQ0])]})]});}
            var Q154;
            {var subQ0=sQuery(id+"F2.wireOp",EDGE,"E23");Q154=makeQuery(id+"FPISK7QOFB9ojP9_2.opFillet","BLEND_EDGE",EDGE,{"blendedFrom":[makeQuery(id+"F3.opExtrude","CAP_EDGE",EDGE,{"disambiguationData":[OSD([subQ0])],"isStart":true}),makeQuery(id+"F3.opExtrude","SWEPT_FACE",FACE,{"disambiguationData":[OSD([subQ0])]})],"blendedInto":[makeQuery(id+"F3.opExtrude","SWEPT_FACE",FACE,{"disambiguationData":[OSD([subQ0])]})]});}
            var Q155;
            {var subQ0=sQuery(id+"F2.wireOp",EDGE,"E13");Q155=makeQuery(id+"FPISK7QOFB9ojP9_2.opFillet","BLEND_EDGE",EDGE,{"blendedFrom":[makeQuery(id+"F3.opExtrude","CAP_EDGE",EDGE,{"disambiguationData":[OSD([subQ0])],"isStart":true}),makeQuery(id+"F3.opExtrude","SWEPT_FACE",FACE,{"disambiguationData":[OSD([subQ0])]})],"blendedInto":[makeQuery(id+"F3.opExtrude","SWEPT_FACE",FACE,{"disambiguationData":[OSD([subQ0])]})]});}
            var Q156;
            {var subQ0=sQuery(id+"F2.wireOp",EDGE,"E12");Q156=makeQuery(id+"FPISK7QOFB9ojP9_2.opFillet","BLEND_EDGE",EDGE,{"blendedFrom":[makeQuery(id+"F3.opExtrude","CAP_VERTEX",VERTEX,{"disambiguationData":[OSD([subQ0,sQuery(id+"F2.wireOp",EDGE,"E13")])],"isStart":false}),makeQuery(id+"F3.opExtrude","CAP_EDGE",EDGE,{"disambiguationData":[OSD([subQ0])],"isStart":false})],"blendedInto":[]});}
            var Q157;
            {var subQ0=sQuery(id+"F2.wireOp",EDGE,"E12");Q157=makeQuery(id+"FPISK7QOFB9ojP9_2.opFillet","BLEND_FACE",FACE,{"disambiguationData":[OSD([subQ0]),TDD([makeQuery(id+"F3.opExtrude","CAP_EDGE",EDGE,{"disambiguationData":[OSD([subQ0])],"isStart":true})])]});}
            var Q158;
            {var subQ0=sQuery(id+"F2.wireOp",EDGE,"E20");Q158=makeQuery(id+"FPISK7QOFB9ojP9_2.opFillet","BLEND_EDGE",EDGE,{"blendedFrom":[makeQuery(id+"F3.opExtrude","CAP_EDGE",EDGE,{"disambiguationData":[OSD([subQ0])],"isStart":true}),makeQuery(id+"F3.opExtrude","CAP_FACE",FACE,{"disambiguationData":[OSD([sQuery(id+"F2.wireOp",EDGE,"E7"),sQuery(id+"F2.wireOp",EDGE,"E8"),sQuery(id+"F2.wireOp",EDGE,"E9"),sQuery(id+"F2.wireOp",EDGE,"E10"),sQuery(id+"F2.wireOp",EDGE,"E11"),sQuery(id+"F2.wireOp",EDGE,"E12"),sQuery(id+"F2.wireOp",EDGE,"E13"),sQuery(id+"F2.wireOp",EDGE,"E14"),sQuery(id+"F2.wireOp",EDGE,"E15"),sQuery(id+"F2.wireOp",EDGE,"E16"),sQuery(id+"F2.wireOp",EDGE,"E17"),sQuery(id+"F2.wireOp",EDGE,"E18"),sQuery(id+"F2.wireOp",EDGE,"E19"),subQ0,sQuery(id+"F2.wireOp",EDGE,"E21"),sQuery(id+"F2.wireOp",EDGE,"E22"),sQuery(id+"F2.wireOp",EDGE,"E23"),sQuery(id+"F2.wireOp",EDGE,"E24")])],"isStart":true})],"blendedInto":[makeQuery(id+"F3.opExtrude","CAP_FACE",FACE,{"disambiguationData":[OSD([sQuery(id+"F2.wireOp",EDGE,"E7"),sQuery(id+"F2.wireOp",EDGE,"E8"),sQuery(id+"F2.wireOp",EDGE,"E9"),sQuery(id+"F2.wireOp",EDGE,"E10"),sQuery(id+"F2.wireOp",EDGE,"E11"),sQuery(id+"F2.wireOp",EDGE,"E12"),sQuery(id+"F2.wireOp",EDGE,"E13"),sQuery(id+"F2.wireOp",EDGE,"E14"),sQuery(id+"F2.wireOp",EDGE,"E15"),sQuery(id+"F2.wireOp",EDGE,"E16"),sQuery(id+"F2.wireOp",EDGE,"E17"),sQuery(id+"F2.wireOp",EDGE,"E18"),sQuery(id+"F2.wireOp",EDGE,"E19"),subQ0,sQuery(id+"F2.wireOp",EDGE,"E21"),sQuery(id+"F2.wireOp",EDGE,"E22"),sQuery(id+"F2.wireOp",EDGE,"E23"),sQuery(id+"F2.wireOp",EDGE,"E24")])],"isStart":true})]});}
            var Q159;
            {var subQ0=sQuery(id+"F2.wireOp",EDGE,"E17");var subQ1=sQuery(id+"F2.wireOp",EDGE,"E8");Q159=makeQuery(id+"FPISK7QOFB9ojP9_2.opFillet","BLEND_EDGE",EDGE,{"blendedFrom":[makeQuery(id+"F3.opExtrude","CAP_EDGE",EDGE,{"disambiguationData":[OSD([subQ1,subQ0])],"isStart":true}),makeQuery(id+"F3.opExtrude","CAP_FACE",FACE,{"disambiguationData":[OSD([sQuery(id+"F2.wireOp",EDGE,"E7"),subQ1,sQuery(id+"F2.wireOp",EDGE,"E9"),sQuery(id+"F2.wireOp",EDGE,"E10"),sQuery(id+"F2.wireOp",EDGE,"E11"),sQuery(id+"F2.wireOp",EDGE,"E12"),sQuery(id+"F2.wireOp",EDGE,"E13"),sQuery(id+"F2.wireOp",EDGE,"E14"),sQuery(id+"F2.wireOp",EDGE,"E15"),sQuery(id+"F2.wireOp",EDGE,"E16"),subQ0,sQuery(id+"F2.wireOp",EDGE,"E18"),sQuery(id+"F2.wireOp",EDGE,"E19"),sQuery(id+"F2.wireOp",EDGE,"E20"),sQuery(id+"F2.wireOp",EDGE,"E21"),sQuery(id+"F2.wireOp",EDGE,"E22"),sQuery(id+"F2.wireOp",EDGE,"E23"),sQuery(id+"F2.wireOp",EDGE,"E24")])],"isStart":true})],"blendedInto":[makeQuery(id+"F3.opExtrude","CAP_FACE",FACE,{"disambiguationData":[OSD([sQuery(id+"F2.wireOp",EDGE,"E7"),subQ1,sQuery(id+"F2.wireOp",EDGE,"E9"),sQuery(id+"F2.wireOp",EDGE,"E10"),sQuery(id+"F2.wireOp",EDGE,"E11"),sQuery(id+"F2.wireOp",EDGE,"E12"),sQuery(id+"F2.wireOp",EDGE,"E13"),sQuery(id+"F2.wireOp",EDGE,"E14"),sQuery(id+"F2.wireOp",EDGE,"E15"),sQuery(id+"F2.wireOp",EDGE,"E16"),subQ0,sQuery(id+"F2.wireOp",EDGE,"E18"),sQuery(id+"F2.wireOp",EDGE,"E19"),sQuery(id+"F2.wireOp",EDGE,"E20"),sQuery(id+"F2.wireOp",EDGE,"E21"),sQuery(id+"F2.wireOp",EDGE,"E22"),sQuery(id+"F2.wireOp",EDGE,"E23"),sQuery(id+"F2.wireOp",EDGE,"E24")])],"isStart":true})]});}
            var Q160;
            {var subQ0=sQuery(id+"F2.wireOp",EDGE,"E22");Q160=makeQuery(id+"FPISK7QOFB9ojP9_2.opFillet","BLEND_EDGE",EDGE,{"blendedFrom":[makeQuery(id+"F3.opExtrude","CAP_VERTEX",VERTEX,{"disambiguationData":[OSD([sQuery(id+"F2.wireOp",EDGE,"E21"),subQ0])],"isStart":false}),makeQuery(id+"F3.opExtrude","CAP_EDGE",EDGE,{"disambiguationData":[OSD([sQuery(id+"F2.wireOp",EDGE,"E10"),subQ0])],"isStart":false})],"blendedInto":[]});}
            var Q161;
            {var subQ0=sQuery(id+"F2.wireOp",EDGE,"E23");Q161=makeQuery(id+"FPISK7QOFB9ojP9_2.opFillet","BLEND_EDGE",EDGE,{"blendedFrom":[makeQuery(id+"F3.opExtrude","CAP_VERTEX",VERTEX,{"disambiguationData":[OSD([subQ0,sQuery(id+"F2.wireOp",EDGE,"E24")])],"isStart":false}),makeQuery(id+"F3.opExtrude","CAP_EDGE",EDGE,{"disambiguationData":[OSD([subQ0])],"isStart":false})],"blendedInto":[]});}
            var Q162;
            {var subQ0=sQuery(id+"F2.wireOp",EDGE,"E23");Q162=makeQuery(id+"FPISK7QOFB9ojP9_2.opFillet","BLEND_EDGE",EDGE,{"blendedFrom":[makeQuery(id+"F3.opExtrude","CAP_VERTEX",VERTEX,{"disambiguationData":[OSD([sQuery(id+"F2.wireOp",EDGE,"E20"),subQ0])],"isStart":false}),makeQuery(id+"F3.opExtrude","CAP_EDGE",EDGE,{"disambiguationData":[OSD([subQ0])],"isStart":false})],"blendedInto":[]});}
            var Q163;
            {var subQ0=sQuery(id+"F2.wireOp",EDGE,"E18");Q163=makeQuery(id+"FPISK7QOFB9ojP9_2.opFillet","BLEND_EDGE",EDGE,{"blendedFrom":[makeQuery(id+"F3.opExtrude","CAP_VERTEX",VERTEX,{"disambiguationData":[OSD([subQ0,sQuery(id+"F2.wireOp",EDGE,"E20")])],"isStart":false}),makeQuery(id+"F3.opExtrude","CAP_EDGE",EDGE,{"disambiguationData":[OSD([subQ0])],"isStart":false})],"blendedInto":[]});}
            var Q164;
            {var subQ0=sQuery(id+"F2.wireOp",EDGE,"E18");Q164=makeQuery(id+"FPISK7QOFB9ojP9_2.opFillet","BLEND_EDGE",EDGE,{"blendedFrom":[makeQuery(id+"F3.opExtrude","CAP_VERTEX",VERTEX,{"disambiguationData":[OSD([sQuery(id+"F2.wireOp",EDGE,"E15"),subQ0])],"isStart":false}),makeQuery(id+"F3.opExtrude","CAP_EDGE",EDGE,{"disambiguationData":[OSD([subQ0])],"isStart":false})],"blendedInto":[]});}
            var Q165;
            {var subQ0=sQuery(id+"F2.wireOp",EDGE,"E15");Q165=makeQuery(id+"FPISK7QOFB9ojP9_2.opFillet","BLEND_EDGE",EDGE,{"blendedFrom":[makeQuery(id+"F3.opExtrude","CAP_EDGE",EDGE,{"disambiguationData":[OSD([subQ0])],"isStart":true}),makeQuery(id+"F3.opExtrude","SWEPT_FACE",FACE,{"disambiguationData":[OSD([subQ0])]})],"blendedInto":[makeQuery(id+"F3.opExtrude","SWEPT_FACE",FACE,{"disambiguationData":[OSD([subQ0])]})]});}
            var Q166;
            {var subQ0=sQuery(id+"F2.wireOp",EDGE,"E12");Q166=makeQuery(id+"FPISK7QOFB9ojP9_2.opFillet","BLEND_EDGE",EDGE,{"blendedFrom":[makeQuery(id+"F3.opExtrude","CAP_VERTEX",VERTEX,{"disambiguationData":[OSD([subQ0,sQuery(id+"F2.wireOp",EDGE,"E13")])],"isStart":true}),makeQuery(id+"F3.opExtrude","CAP_EDGE",EDGE,{"disambiguationData":[OSD([subQ0])],"isStart":true})],"blendedInto":[]});}
            var Q167;
            {var subQ0=sQuery(id+"F2.wireOp",EDGE,"E20");Q167=makeQuery(id+"FPISK7QOFB9ojP9_2.opFillet","BLEND_EDGE",EDGE,{"blendedFrom":[makeQuery(id+"F3.opExtrude","CAP_VERTEX",VERTEX,{"disambiguationData":[OSD([subQ0,sQuery(id+"F2.wireOp",EDGE,"E23")])],"isStart":true}),makeQuery(id+"F3.opExtrude","CAP_EDGE",EDGE,{"disambiguationData":[OSD([subQ0])],"isStart":true})],"blendedInto":[]});}
            var Q168;
            {var subQ0=sQuery(id+"F2.wireOp",EDGE,"E21");Q168=makeQuery(id+"FPISK7QOFB9ojP9_2.opFillet","BLEND_EDGE",EDGE,{"blendedFrom":[makeQuery(id+"F3.opExtrude","CAP_VERTEX",VERTEX,{"disambiguationData":[OSD([subQ0,sQuery(id+"F2.wireOp",EDGE,"E22")])],"isStart":false}),makeQuery(id+"F3.opExtrude","CAP_EDGE",EDGE,{"disambiguationData":[OSD([sQuery(id+"F2.wireOp",EDGE,"E11"),subQ0])],"isStart":false})],"blendedInto":[]});}
            var Q169;
            {var subQ0=sQuery(id+"F2.wireOp",EDGE,"E20");Q169=makeQuery(id+"FPISK7QOFB9ojP9_2.opFillet","BLEND_EDGE",EDGE,{"blendedFrom":[makeQuery(id+"F3.opExtrude","CAP_VERTEX",VERTEX,{"disambiguationData":[OSD([sQuery(id+"F2.wireOp",EDGE,"E18"),subQ0])],"isStart":true}),makeQuery(id+"F3.opExtrude","CAP_EDGE",EDGE,{"disambiguationData":[OSD([subQ0])],"isStart":true})],"blendedInto":[]});}
            var Q170;
            {var subQ0=sQuery(id+"F2.wireOp",EDGE,"E15");Q170=makeQuery(id+"FPISK7QOFB9ojP9_2.opFillet","BLEND_EDGE",EDGE,{"blendedFrom":[makeQuery(id+"F3.opExtrude","CAP_VERTEX",VERTEX,{"disambiguationData":[OSD([sQuery(id+"F2.wireOp",EDGE,"E13"),subQ0])],"isStart":false}),makeQuery(id+"F3.opExtrude","CAP_EDGE",EDGE,{"disambiguationData":[OSD([subQ0])],"isStart":false})],"blendedInto":[]});}
            var Q171;
            {var subQ0=sQuery(id+"F2.wireOp",EDGE,"E24");Q171=makeQuery(id+"FPISK7QOFB9ojP9_2.opFillet","BLEND_EDGE",EDGE,{"blendedFrom":[makeQuery(id+"F3.opExtrude","CAP_EDGE",EDGE,{"disambiguationData":[OSD([subQ0])],"isStart":false}),makeQuery(id+"F3.opExtrude","CAP_FACE",FACE,{"disambiguationData":[OSD([sQuery(id+"F2.wireOp",EDGE,"E7"),sQuery(id+"F2.wireOp",EDGE,"E8"),sQuery(id+"F2.wireOp",EDGE,"E9"),sQuery(id+"F2.wireOp",EDGE,"E10"),sQuery(id+"F2.wireOp",EDGE,"E11"),sQuery(id+"F2.wireOp",EDGE,"E12"),sQuery(id+"F2.wireOp",EDGE,"E13"),sQuery(id+"F2.wireOp",EDGE,"E14"),sQuery(id+"F2.wireOp",EDGE,"E15"),sQuery(id+"F2.wireOp",EDGE,"E16"),sQuery(id+"F2.wireOp",EDGE,"E17"),sQuery(id+"F2.wireOp",EDGE,"E18"),sQuery(id+"F2.wireOp",EDGE,"E19"),sQuery(id+"F2.wireOp",EDGE,"E20"),sQuery(id+"F2.wireOp",EDGE,"E21"),sQuery(id+"F2.wireOp",EDGE,"E22"),sQuery(id+"F2.wireOp",EDGE,"E23"),subQ0])],"isStart":false})],"blendedInto":[makeQuery(id+"F3.opExtrude","CAP_FACE",FACE,{"disambiguationData":[OSD([sQuery(id+"F2.wireOp",EDGE,"E7"),sQuery(id+"F2.wireOp",EDGE,"E8"),sQuery(id+"F2.wireOp",EDGE,"E9"),sQuery(id+"F2.wireOp",EDGE,"E10"),sQuery(id+"F2.wireOp",EDGE,"E11"),sQuery(id+"F2.wireOp",EDGE,"E12"),sQuery(id+"F2.wireOp",EDGE,"E13"),sQuery(id+"F2.wireOp",EDGE,"E14"),sQuery(id+"F2.wireOp",EDGE,"E15"),sQuery(id+"F2.wireOp",EDGE,"E16"),sQuery(id+"F2.wireOp",EDGE,"E17"),sQuery(id+"F2.wireOp",EDGE,"E18"),sQuery(id+"F2.wireOp",EDGE,"E19"),sQuery(id+"F2.wireOp",EDGE,"E20"),sQuery(id+"F2.wireOp",EDGE,"E21"),sQuery(id+"F2.wireOp",EDGE,"E22"),sQuery(id+"F2.wireOp",EDGE,"E23"),subQ0])],"isStart":false})]});}
            var Q172;
            {var subQ0=sQuery(id+"F2.wireOp",EDGE,"E24");var subQ1=sQuery(id+"F2.wireOp",EDGE,"E23");Q172=makeQuery(id+"FPISK7QOFB9ojP9_2.opFillet","BLEND_EDGE",EDGE,{"blendedFrom":[makeQuery(id+"F3.opExtrude","CAP_VERTEX",VERTEX,{"disambiguationData":[OSD([subQ1,subQ0])],"isStart":true}),makeQuery(id+"F3.opExtrude","SWEPT_EDGE",EDGE,{"disambiguationData":[OSD([subQ1,subQ0])]})],"blendedInto":[]});}
            var Q173;
            {var subQ0=sQuery(id+"F2.wireOp",EDGE,"E11");Q173=makeQuery(id+"FPISK7QOFB9ojP9_2.opFillet","BLEND_EDGE",EDGE,{"blendedFrom":[makeQuery(id+"F3.opExtrude","CAP_VERTEX",VERTEX,{"disambiguationData":[OSD([subQ0,sQuery(id+"F2.wireOp",EDGE,"E24")])],"isStart":true}),makeQuery(id+"F3.opExtrude","CAP_EDGE",EDGE,{"disambiguationData":[OSD([subQ0,sQuery(id+"F2.wireOp",EDGE,"E21")])],"isStart":true})],"blendedInto":[]});}
            var Q174;
            {var subQ0=sQuery(id+"F2.wireOp",EDGE,"E19");Q174=makeQuery(id+"FPISK7QOFB9ojP9_2.opFillet","BLEND_EDGE",EDGE,{"blendedFrom":[makeQuery(id+"F3.opExtrude","CAP_VERTEX",VERTEX,{"disambiguationData":[OSD([sQuery(id+"F2.wireOp",EDGE,"E10"),subQ0])],"isStart":true}),makeQuery(id+"F3.opExtrude","CAP_EDGE",EDGE,{"disambiguationData":[OSD([sQuery(id+"F2.wireOp",EDGE,"E9"),sQuery(id+"F2.wireOp",EDGE,"E16"),subQ0])],"isStart":true})],"blendedInto":[]});}
            var Q175;
            {var subQ0=sQuery(id+"F2.wireOp",EDGE,"E15");var subQ1=sQuery(id+"F2.wireOp",EDGE,"E13");Q175=makeQuery(id+"FPISK7QOFB9ojP9_2.opFillet","BLEND_EDGE",EDGE,{"blendedFrom":[makeQuery(id+"F3.opExtrude","CAP_VERTEX",VERTEX,{"disambiguationData":[OSD([subQ1,subQ0])],"isStart":true}),makeQuery(id+"F3.opExtrude","SWEPT_EDGE",EDGE,{"disambiguationData":[OSD([subQ1,subQ0])]})],"blendedInto":[]});}
            var Q176;
            {var subQ0=sQuery(id+"F2.wireOp",EDGE,"E16");Q176=makeQuery(id+"FPISK7QOFB9ojP9_2.opFillet","BLEND_EDGE",EDGE,{"blendedFrom":[makeQuery(id+"F3.opExtrude","CAP_VERTEX",VERTEX,{"disambiguationData":[OSD([subQ0,sQuery(id+"F2.wireOp",EDGE,"E17")])],"isStart":true}),makeQuery(id+"F3.opExtrude","CAP_EDGE",EDGE,{"disambiguationData":[OSD([sQuery(id+"F2.wireOp",EDGE,"E9"),subQ0,sQuery(id+"F2.wireOp",EDGE,"E19")])],"isStart":true})],"blendedInto":[]});}
            var Q177;
            {var subQ0=sQuery(id+"F2.wireOp",EDGE,"E7");Q177=makeQuery(id+"FPISK7QOFB9ojP9_2.opFillet","BLEND_EDGE",EDGE,{"blendedFrom":[makeQuery(id+"F3.opExtrude","CAP_VERTEX",VERTEX,{"disambiguationData":[OSD([subQ0,sQuery(id+"F2.wireOp",EDGE,"E12")])],"isStart":true}),makeQuery(id+"F3.opExtrude","CAP_EDGE",EDGE,{"disambiguationData":[OSD([subQ0,sQuery(id+"F2.wireOp",EDGE,"E14")])],"isStart":true})],"blendedInto":[]});}
            var Q178;
            {var subQ0=sQuery(id+"F2.wireOp",EDGE,"E20");var subQ1=sQuery(id+"F2.wireOp",EDGE,"E18");Q178=makeQuery(id+"FPISK7QOFB9ojP9_2.opFillet","BLEND_EDGE",EDGE,{"blendedFrom":[makeQuery(id+"F3.opExtrude","CAP_VERTEX",VERTEX,{"disambiguationData":[OSD([subQ1,subQ0])],"isStart":true}),makeQuery(id+"F3.opExtrude","SWEPT_EDGE",EDGE,{"disambiguationData":[OSD([subQ1,subQ0])]})],"blendedInto":[]});}
            var Q179;
            {var subQ0=sQuery(id+"F2.wireOp",EDGE,"E12");Q179=makeQuery(id+"FPISK7QOFB9ojP9_2.opFillet","BLEND_EDGE",EDGE,{"blendedFrom":[makeQuery(id+"F3.opExtrude","CAP_VERTEX",VERTEX,{"disambiguationData":[OSD([sQuery(id+"F2.wireOp",EDGE,"E7"),subQ0])],"isStart":true}),makeQuery(id+"F3.opExtrude","CAP_EDGE",EDGE,{"disambiguationData":[OSD([subQ0])],"isStart":true})],"blendedInto":[]});}
            var Q180;
            {var subQ0=sQuery(id+"F2.wireOp",EDGE,"E23");Q180=makeQuery(id+"FPISK7QOFB9ojP9_2.opFillet","BLEND_EDGE",EDGE,{"blendedFrom":[makeQuery(id+"F3.opExtrude","CAP_EDGE",EDGE,{"disambiguationData":[OSD([subQ0])],"isStart":true}),makeQuery(id+"F3.opExtrude","CAP_FACE",FACE,{"disambiguationData":[OSD([sQuery(id+"F2.wireOp",EDGE,"E7"),sQuery(id+"F2.wireOp",EDGE,"E8"),sQuery(id+"F2.wireOp",EDGE,"E9"),sQuery(id+"F2.wireOp",EDGE,"E10"),sQuery(id+"F2.wireOp",EDGE,"E11"),sQuery(id+"F2.wireOp",EDGE,"E12"),sQuery(id+"F2.wireOp",EDGE,"E13"),sQuery(id+"F2.wireOp",EDGE,"E14"),sQuery(id+"F2.wireOp",EDGE,"E15"),sQuery(id+"F2.wireOp",EDGE,"E16"),sQuery(id+"F2.wireOp",EDGE,"E17"),sQuery(id+"F2.wireOp",EDGE,"E18"),sQuery(id+"F2.wireOp",EDGE,"E19"),sQuery(id+"F2.wireOp",EDGE,"E20"),sQuery(id+"F2.wireOp",EDGE,"E21"),sQuery(id+"F2.wireOp",EDGE,"E22"),subQ0,sQuery(id+"F2.wireOp",EDGE,"E24")])],"isStart":true})],"blendedInto":[makeQuery(id+"F3.opExtrude","CAP_FACE",FACE,{"disambiguationData":[OSD([sQuery(id+"F2.wireOp",EDGE,"E7"),sQuery(id+"F2.wireOp",EDGE,"E8"),sQuery(id+"F2.wireOp",EDGE,"E9"),sQuery(id+"F2.wireOp",EDGE,"E10"),sQuery(id+"F2.wireOp",EDGE,"E11"),sQuery(id+"F2.wireOp",EDGE,"E12"),sQuery(id+"F2.wireOp",EDGE,"E13"),sQuery(id+"F2.wireOp",EDGE,"E14"),sQuery(id+"F2.wireOp",EDGE,"E15"),sQuery(id+"F2.wireOp",EDGE,"E16"),sQuery(id+"F2.wireOp",EDGE,"E17"),sQuery(id+"F2.wireOp",EDGE,"E18"),sQuery(id+"F2.wireOp",EDGE,"E19"),sQuery(id+"F2.wireOp",EDGE,"E20"),sQuery(id+"F2.wireOp",EDGE,"E21"),sQuery(id+"F2.wireOp",EDGE,"E22"),subQ0,sQuery(id+"F2.wireOp",EDGE,"E24")])],"isStart":true})]});}
            var Q181;
            {var subQ0=sQuery(id+"F2.wireOp",EDGE,"E13");Q181=makeQuery(id+"FPISK7QOFB9ojP9_2.opFillet","BLEND_EDGE",EDGE,{"blendedFrom":[makeQuery(id+"F3.opExtrude","CAP_EDGE",EDGE,{"disambiguationData":[OSD([subQ0])],"isStart":true}),makeQuery(id+"F3.opExtrude","CAP_FACE",FACE,{"disambiguationData":[OSD([sQuery(id+"F2.wireOp",EDGE,"E7"),sQuery(id+"F2.wireOp",EDGE,"E8"),sQuery(id+"F2.wireOp",EDGE,"E9"),sQuery(id+"F2.wireOp",EDGE,"E10"),sQuery(id+"F2.wireOp",EDGE,"E11"),sQuery(id+"F2.wireOp",EDGE,"E12"),subQ0,sQuery(id+"F2.wireOp",EDGE,"E14"),sQuery(id+"F2.wireOp",EDGE,"E15"),sQuery(id+"F2.wireOp",EDGE,"E16"),sQuery(id+"F2.wireOp",EDGE,"E17"),sQuery(id+"F2.wireOp",EDGE,"E18"),sQuery(id+"F2.wireOp",EDGE,"E19"),sQuery(id+"F2.wireOp",EDGE,"E20"),sQuery(id+"F2.wireOp",EDGE,"E21"),sQuery(id+"F2.wireOp",EDGE,"E22"),sQuery(id+"F2.wireOp",EDGE,"E23"),sQuery(id+"F2.wireOp",EDGE,"E24")])],"isStart":true})],"blendedInto":[makeQuery(id+"F3.opExtrude","CAP_FACE",FACE,{"disambiguationData":[OSD([sQuery(id+"F2.wireOp",EDGE,"E7"),sQuery(id+"F2.wireOp",EDGE,"E8"),sQuery(id+"F2.wireOp",EDGE,"E9"),sQuery(id+"F2.wireOp",EDGE,"E10"),sQuery(id+"F2.wireOp",EDGE,"E11"),sQuery(id+"F2.wireOp",EDGE,"E12"),subQ0,sQuery(id+"F2.wireOp",EDGE,"E14"),sQuery(id+"F2.wireOp",EDGE,"E15"),sQuery(id+"F2.wireOp",EDGE,"E16"),sQuery(id+"F2.wireOp",EDGE,"E17"),sQuery(id+"F2.wireOp",EDGE,"E18"),sQuery(id+"F2.wireOp",EDGE,"E19"),sQuery(id+"F2.wireOp",EDGE,"E20"),sQuery(id+"F2.wireOp",EDGE,"E21"),sQuery(id+"F2.wireOp",EDGE,"E22"),sQuery(id+"F2.wireOp",EDGE,"E23"),sQuery(id+"F2.wireOp",EDGE,"E24")])],"isStart":true})]});}
            var Q182;
            {var subQ0=sQuery(id+"F2.wireOp",EDGE,"E13");var subQ1=sQuery(id+"F2.wireOp",EDGE,"E12");Q182=makeQuery(id+"FPISK7QOFB9ojP9_2.opFillet","BLEND_EDGE",EDGE,{"blendedFrom":[makeQuery(id+"F3.opExtrude","CAP_VERTEX",VERTEX,{"disambiguationData":[OSD([subQ1,subQ0])],"isStart":false}),makeQuery(id+"F3.opExtrude","SWEPT_EDGE",EDGE,{"disambiguationData":[OSD([subQ1,subQ0])]})],"blendedInto":[]});}
            var Q183;
            {var subQ0=sQuery(id+"F2.wireOp",EDGE,"E7");Q183=makeQuery(id+"FPISK7QOFB9ojP9_2.opFillet","BLEND_EDGE",EDGE,{"blendedFrom":[makeQuery(id+"F3.opExtrude","CAP_VERTEX",VERTEX,{"disambiguationData":[OSD([subQ0,sQuery(id+"F2.wireOp",EDGE,"E12")])],"isStart":false}),makeQuery(id+"F3.opExtrude","CAP_EDGE",EDGE,{"disambiguationData":[OSD([subQ0,sQuery(id+"F2.wireOp",EDGE,"E14")])],"isStart":false})],"blendedInto":[]});}
            var Q184;
            {var subQ0=sQuery(id+"F2.wireOp",EDGE,"E14");Q184=makeQuery(id+"FPISK7QOFB9ojP9_2.opFillet","BLEND_EDGE",EDGE,{"blendedFrom":[makeQuery(id+"F3.opExtrude","CAP_VERTEX",VERTEX,{"disambiguationData":[OSD([sQuery(id+"F2.wireOp",EDGE,"E8"),subQ0])],"isStart":true}),makeQuery(id+"F3.opExtrude","CAP_EDGE",EDGE,{"disambiguationData":[OSD([sQuery(id+"F2.wireOp",EDGE,"E7"),subQ0])],"isStart":true})],"blendedInto":[]});}
            var Q185;
            {var subQ0=sQuery(id+"F2.wireOp",EDGE,"E8");Q185=makeQuery(id+"FPISK7QOFB9ojP9_2.opFillet","BLEND_EDGE",EDGE,{"blendedFrom":[makeQuery(id+"F3.opExtrude","CAP_VERTEX",VERTEX,{"disambiguationData":[OSD([subQ0,sQuery(id+"F2.wireOp",EDGE,"E14")])],"isStart":true}),makeQuery(id+"F3.opExtrude","CAP_EDGE",EDGE,{"disambiguationData":[OSD([subQ0,sQuery(id+"F2.wireOp",EDGE,"E17")])],"isStart":true})],"blendedInto":[]});}
            var Q186;
            {var subQ0=sQuery(id+"F2.wireOp",EDGE,"E14");var subQ1=sQuery(id+"F2.wireOp",EDGE,"E8");Q186=makeQuery(id+"FPISK7QOFB9ojP9_2.opFillet","BLEND_EDGE",EDGE,{"blendedFrom":[makeQuery(id+"F3.opExtrude","CAP_VERTEX",VERTEX,{"disambiguationData":[OSD([subQ1,subQ0])],"isStart":false}),makeQuery(id+"F3.opExtrude","SWEPT_EDGE",EDGE,{"disambiguationData":[OSD([subQ1,subQ0])]})],"blendedInto":[]});}
            var Q187;
            {var subQ0=sQuery(id+"F2.wireOp",EDGE,"E24");var subQ1=sQuery(id+"F2.wireOp",EDGE,"E23");Q187=makeQuery(id+"FPISK7QOFB9ojP9_2.opFillet","BLEND_EDGE",EDGE,{"blendedFrom":[makeQuery(id+"F3.opExtrude","CAP_VERTEX",VERTEX,{"disambiguationData":[OSD([subQ1,subQ0])],"isStart":false}),makeQuery(id+"F3.opExtrude","SWEPT_EDGE",EDGE,{"disambiguationData":[OSD([subQ1,subQ0])]})],"blendedInto":[]});}
            var Q188;
            {var subQ0=sQuery(id+"F2.wireOp",EDGE,"E24");Q188=makeQuery(id+"FPISK7QOFB9ojP9_2.opFillet","BLEND_EDGE",EDGE,{"blendedFrom":[makeQuery(id+"F3.opExtrude","CAP_VERTEX",VERTEX,{"disambiguationData":[OSD([sQuery(id+"F2.wireOp",EDGE,"E11"),subQ0])],"isStart":true}),makeQuery(id+"F3.opExtrude","CAP_EDGE",EDGE,{"disambiguationData":[OSD([subQ0])],"isStart":true})],"blendedInto":[]});}
            var Q189;
            {var subQ0=sQuery(id+"F2.wireOp",EDGE,"E20");Q189=makeQuery(id+"FPISK7QOFB9ojP9_2.opFillet","BLEND_EDGE",EDGE,{"blendedFrom":[makeQuery(id+"F3.opExtrude","CAP_VERTEX",VERTEX,{"disambiguationData":[OSD([subQ0,sQuery(id+"F2.wireOp",EDGE,"E23")])],"isStart":false}),makeQuery(id+"F3.opExtrude","CAP_EDGE",EDGE,{"disambiguationData":[OSD([subQ0])],"isStart":false})],"blendedInto":[]});}
            var Q190;
            {var subQ0=sQuery(id+"F2.wireOp",EDGE,"E20");var subQ1=sQuery(id+"F2.wireOp",EDGE,"E18");Q190=makeQuery(id+"FPISK7QOFB9ojP9_2.opFillet","BLEND_EDGE",EDGE,{"blendedFrom":[makeQuery(id+"F3.opExtrude","CAP_VERTEX",VERTEX,{"disambiguationData":[OSD([subQ1,subQ0])],"isStart":false}),makeQuery(id+"F3.opExtrude","SWEPT_EDGE",EDGE,{"disambiguationData":[OSD([subQ1,subQ0])]})],"blendedInto":[]});}
            var Q191;
            {var subQ0=sQuery(id+"F2.wireOp",EDGE,"E15");Q191=makeQuery(id+"FPISK7QOFB9ojP9_2.opFillet","BLEND_EDGE",EDGE,{"blendedFrom":[makeQuery(id+"F3.opExtrude","CAP_EDGE",EDGE,{"disambiguationData":[OSD([subQ0])],"isStart":true}),makeQuery(id+"F3.opExtrude","CAP_FACE",FACE,{"disambiguationData":[OSD([sQuery(id+"F2.wireOp",EDGE,"E7"),sQuery(id+"F2.wireOp",EDGE,"E8"),sQuery(id+"F2.wireOp",EDGE,"E9"),sQuery(id+"F2.wireOp",EDGE,"E10"),sQuery(id+"F2.wireOp",EDGE,"E11"),sQuery(id+"F2.wireOp",EDGE,"E12"),sQuery(id+"F2.wireOp",EDGE,"E13"),sQuery(id+"F2.wireOp",EDGE,"E14"),subQ0,sQuery(id+"F2.wireOp",EDGE,"E16"),sQuery(id+"F2.wireOp",EDGE,"E17"),sQuery(id+"F2.wireOp",EDGE,"E18"),sQuery(id+"F2.wireOp",EDGE,"E19"),sQuery(id+"F2.wireOp",EDGE,"E20"),sQuery(id+"F2.wireOp",EDGE,"E21"),sQuery(id+"F2.wireOp",EDGE,"E22"),sQuery(id+"F2.wireOp",EDGE,"E23"),sQuery(id+"F2.wireOp",EDGE,"E24")])],"isStart":true})],"blendedInto":[makeQuery(id+"F3.opExtrude","CAP_FACE",FACE,{"disambiguationData":[OSD([sQuery(id+"F2.wireOp",EDGE,"E7"),sQuery(id+"F2.wireOp",EDGE,"E8"),sQuery(id+"F2.wireOp",EDGE,"E9"),sQuery(id+"F2.wireOp",EDGE,"E10"),sQuery(id+"F2.wireOp",EDGE,"E11"),sQuery(id+"F2.wireOp",EDGE,"E12"),sQuery(id+"F2.wireOp",EDGE,"E13"),sQuery(id+"F2.wireOp",EDGE,"E14"),subQ0,sQuery(id+"F2.wireOp",EDGE,"E16"),sQuery(id+"F2.wireOp",EDGE,"E17"),sQuery(id+"F2.wireOp",EDGE,"E18"),sQuery(id+"F2.wireOp",EDGE,"E19"),sQuery(id+"F2.wireOp",EDGE,"E20"),sQuery(id+"F2.wireOp",EDGE,"E21"),sQuery(id+"F2.wireOp",EDGE,"E22"),sQuery(id+"F2.wireOp",EDGE,"E23"),sQuery(id+"F2.wireOp",EDGE,"E24")])],"isStart":true})]});}
            var Q192;
            {var subQ0=sQuery(id+"F2.wireOp",EDGE,"E23");var subQ1=sQuery(id+"F2.wireOp",EDGE,"E20");Q192=makeQuery(id+"FPISK7QOFB9ojP9_2.opFillet","BLEND_EDGE",EDGE,{"blendedFrom":[makeQuery(id+"F3.opExtrude","CAP_VERTEX",VERTEX,{"disambiguationData":[OSD([subQ1,subQ0])],"isStart":false}),makeQuery(id+"F3.opExtrude","SWEPT_EDGE",EDGE,{"disambiguationData":[OSD([subQ1,subQ0])]})],"blendedInto":[]});}
            var Q193;
            {var subQ0=sQuery(id+"F2.wireOp",EDGE,"E18");var subQ1=sQuery(id+"F2.wireOp",EDGE,"E15");Q193=makeQuery(id+"FPISK7QOFB9ojP9_2.opFillet","BLEND_EDGE",EDGE,{"blendedFrom":[makeQuery(id+"F3.opExtrude","CAP_VERTEX",VERTEX,{"disambiguationData":[OSD([subQ1,subQ0])],"isStart":false}),makeQuery(id+"F3.opExtrude","SWEPT_EDGE",EDGE,{"disambiguationData":[OSD([subQ1,subQ0])]})],"blendedInto":[]});}
            var Q194;
            {var subQ0=sQuery(id+"F2.wireOp",EDGE,"E23");var subQ1=sQuery(id+"F2.wireOp",EDGE,"E20");Q194=makeQuery(id+"FPISK7QOFB9ojP9_2.opFillet","BLEND_EDGE",EDGE,{"blendedFrom":[makeQuery(id+"F3.opExtrude","CAP_VERTEX",VERTEX,{"disambiguationData":[OSD([subQ1,subQ0])],"isStart":true}),makeQuery(id+"F3.opExtrude","SWEPT_EDGE",EDGE,{"disambiguationData":[OSD([subQ1,subQ0])]})],"blendedInto":[]});}
            var Q195;
            {var subQ0=sQuery(id+"F2.wireOp",EDGE,"E18");var subQ1=sQuery(id+"F2.wireOp",EDGE,"E15");Q195=makeQuery(id+"FPISK7QOFB9ojP9_2.opFillet","BLEND_EDGE",EDGE,{"blendedFrom":[makeQuery(id+"F3.opExtrude","CAP_VERTEX",VERTEX,{"disambiguationData":[OSD([subQ1,subQ0])],"isStart":true}),makeQuery(id+"F3.opExtrude","SWEPT_EDGE",EDGE,{"disambiguationData":[OSD([subQ1,subQ0])]})],"blendedInto":[]});}
            var Q196;
            {var subQ0=sQuery(id+"F2.wireOp",EDGE,"E13");Q196=makeQuery(id+"FPISK7QOFB9ojP9_2.opFillet","BLEND_EDGE",EDGE,{"blendedFrom":[makeQuery(id+"F3.opExtrude","CAP_VERTEX",VERTEX,{"disambiguationData":[OSD([subQ0,sQuery(id+"F2.wireOp",EDGE,"E15")])],"isStart":false}),makeQuery(id+"F3.opExtrude","CAP_EDGE",EDGE,{"disambiguationData":[OSD([subQ0])],"isStart":false})],"blendedInto":[]});}
            var Q197;
            {var subQ0=sQuery(id+"F2.wireOp",EDGE,"E22");Q197=makeQuery(id+"FPISK7QOFB9ojP9_2.opFillet","BLEND_EDGE",EDGE,{"blendedFrom":[makeQuery(id+"F3.opExtrude","CAP_VERTEX",VERTEX,{"disambiguationData":[OSD([sQuery(id+"F2.wireOp",EDGE,"E21"),subQ0])],"isStart":true}),makeQuery(id+"F3.opExtrude","CAP_EDGE",EDGE,{"disambiguationData":[OSD([sQuery(id+"F2.wireOp",EDGE,"E10"),subQ0])],"isStart":true})],"blendedInto":[]});}
            var Q198;
            {var subQ0=sQuery(id+"F2.wireOp",EDGE,"E12");Q198=makeQuery(id+"FPISK7QOFB9ojP9_2.opFillet","BLEND_EDGE",EDGE,{"blendedFrom":[makeQuery(id+"F3.opExtrude","CAP_EDGE",EDGE,{"disambiguationData":[OSD([subQ0])],"isStart":false}),makeQuery(id+"F3.opExtrude","CAP_FACE",FACE,{"disambiguationData":[OSD([sQuery(id+"F2.wireOp",EDGE,"E7"),sQuery(id+"F2.wireOp",EDGE,"E8"),sQuery(id+"F2.wireOp",EDGE,"E9"),sQuery(id+"F2.wireOp",EDGE,"E10"),sQuery(id+"F2.wireOp",EDGE,"E11"),subQ0,sQuery(id+"F2.wireOp",EDGE,"E13"),sQuery(id+"F2.wireOp",EDGE,"E14"),sQuery(id+"F2.wireOp",EDGE,"E15"),sQuery(id+"F2.wireOp",EDGE,"E16"),sQuery(id+"F2.wireOp",EDGE,"E17"),sQuery(id+"F2.wireOp",EDGE,"E18"),sQuery(id+"F2.wireOp",EDGE,"E19"),sQuery(id+"F2.wireOp",EDGE,"E20"),sQuery(id+"F2.wireOp",EDGE,"E21"),sQuery(id+"F2.wireOp",EDGE,"E22"),sQuery(id+"F2.wireOp",EDGE,"E23"),sQuery(id+"F2.wireOp",EDGE,"E24")])],"isStart":false})],"blendedInto":[makeQuery(id+"F3.opExtrude","CAP_FACE",FACE,{"disambiguationData":[OSD([sQuery(id+"F2.wireOp",EDGE,"E7"),sQuery(id+"F2.wireOp",EDGE,"E8"),sQuery(id+"F2.wireOp",EDGE,"E9"),sQuery(id+"F2.wireOp",EDGE,"E10"),sQuery(id+"F2.wireOp",EDGE,"E11"),subQ0,sQuery(id+"F2.wireOp",EDGE,"E13"),sQuery(id+"F2.wireOp",EDGE,"E14"),sQuery(id+"F2.wireOp",EDGE,"E15"),sQuery(id+"F2.wireOp",EDGE,"E16"),sQuery(id+"F2.wireOp",EDGE,"E17"),sQuery(id+"F2.wireOp",EDGE,"E18"),sQuery(id+"F2.wireOp",EDGE,"E19"),sQuery(id+"F2.wireOp",EDGE,"E20"),sQuery(id+"F2.wireOp",EDGE,"E21"),sQuery(id+"F2.wireOp",EDGE,"E22"),sQuery(id+"F2.wireOp",EDGE,"E23"),sQuery(id+"F2.wireOp",EDGE,"E24")])],"isStart":false})]});}
            var Q199;
            {var subQ0=sQuery(id+"F2.wireOp",EDGE,"E17");var subQ1=sQuery(id+"F2.wireOp",EDGE,"E16");Q199=makeQuery(id+"FPISK7QOFB9ojP9_2.opFillet","BLEND_EDGE",EDGE,{"blendedFrom":[makeQuery(id+"F3.opExtrude","CAP_VERTEX",VERTEX,{"disambiguationData":[OSD([subQ1,subQ0])],"isStart":false}),makeQuery(id+"F3.opExtrude","SWEPT_EDGE",EDGE,{"disambiguationData":[OSD([subQ1,subQ0])]})],"blendedInto":[]});}
            var Q200;
            {var subQ0=sQuery(id+"F2.wireOp",EDGE,"E15");Q200=makeQuery(id+"FPISK7QOFB9ojP9_2.opFillet","BLEND_EDGE",EDGE,{"blendedFrom":[makeQuery(id+"F3.opExtrude","CAP_VERTEX",VERTEX,{"disambiguationData":[OSD([sQuery(id+"F2.wireOp",EDGE,"E13"),subQ0])],"isStart":true}),makeQuery(id+"F3.opExtrude","CAP_EDGE",EDGE,{"disambiguationData":[OSD([subQ0])],"isStart":true})],"blendedInto":[]});}
            var Q201;
            {var subQ0=sQuery(id+"F2.wireOp",EDGE,"E21");Q201=makeQuery(id+"FPISK7QOFB9ojP9_2.opFillet","BLEND_EDGE",EDGE,{"blendedFrom":[makeQuery(id+"F3.opExtrude","CAP_VERTEX",VERTEX,{"disambiguationData":[OSD([subQ0,sQuery(id+"F2.wireOp",EDGE,"E22")])],"isStart":true}),makeQuery(id+"F3.opExtrude","CAP_EDGE",EDGE,{"disambiguationData":[OSD([sQuery(id+"F2.wireOp",EDGE,"E11"),subQ0])],"isStart":true})],"blendedInto":[]});}
            var Q202;
            {var subQ0=sQuery(id+"F2.wireOp",EDGE,"E12");Q202=makeQuery(id+"FPISK7QOFB9ojP9_2.opFillet","BLEND_EDGE",EDGE,{"blendedFrom":[makeQuery(id+"F3.opExtrude","CAP_EDGE",EDGE,{"disambiguationData":[OSD([subQ0])],"isStart":false}),makeQuery(id+"F3.opExtrude","SWEPT_FACE",FACE,{"disambiguationData":[OSD([subQ0])]})],"blendedInto":[makeQuery(id+"F3.opExtrude","SWEPT_FACE",FACE,{"disambiguationData":[OSD([subQ0])]})]});}
            var Q203;
            {var subQ0=sQuery(id+"F2.wireOp",EDGE,"E23");Q203=makeQuery(id+"FPISK7QOFB9ojP9_2.opFillet","BLEND_EDGE",EDGE,{"blendedFrom":[makeQuery(id+"F3.opExtrude","CAP_VERTEX",VERTEX,{"disambiguationData":[OSD([sQuery(id+"F2.wireOp",EDGE,"E20"),subQ0])],"isStart":true}),makeQuery(id+"F3.opExtrude","CAP_EDGE",EDGE,{"disambiguationData":[OSD([subQ0])],"isStart":true})],"blendedInto":[]});}
            var Q204;
            {var subQ0=sQuery(id+"F2.wireOp",EDGE,"E15");var subQ1=sQuery(id+"F2.wireOp",EDGE,"E13");Q204=makeQuery(id+"FPISK7QOFB9ojP9_2.opFillet","BLEND_EDGE",EDGE,{"blendedFrom":[makeQuery(id+"F3.opExtrude","CAP_VERTEX",VERTEX,{"disambiguationData":[OSD([subQ1,subQ0])],"isStart":true}),makeQuery(id+"F3.opExtrude","CAP_FACE",FACE,{"disambiguationData":[OSD([sQuery(id+"F2.wireOp",EDGE,"E7"),sQuery(id+"F2.wireOp",EDGE,"E8"),sQuery(id+"F2.wireOp",EDGE,"E9"),sQuery(id+"F2.wireOp",EDGE,"E10"),sQuery(id+"F2.wireOp",EDGE,"E11"),sQuery(id+"F2.wireOp",EDGE,"E12"),subQ1,sQuery(id+"F2.wireOp",EDGE,"E14"),subQ0,sQuery(id+"F2.wireOp",EDGE,"E16"),sQuery(id+"F2.wireOp",EDGE,"E17"),sQuery(id+"F2.wireOp",EDGE,"E18"),sQuery(id+"F2.wireOp",EDGE,"E19"),sQuery(id+"F2.wireOp",EDGE,"E20"),sQuery(id+"F2.wireOp",EDGE,"E21"),sQuery(id+"F2.wireOp",EDGE,"E22"),sQuery(id+"F2.wireOp",EDGE,"E23"),sQuery(id+"F2.wireOp",EDGE,"E24")])],"isStart":true})],"blendedInto":[makeQuery(id+"F3.opExtrude","CAP_FACE",FACE,{"disambiguationData":[OSD([sQuery(id+"F2.wireOp",EDGE,"E7"),sQuery(id+"F2.wireOp",EDGE,"E8"),sQuery(id+"F2.wireOp",EDGE,"E9"),sQuery(id+"F2.wireOp",EDGE,"E10"),sQuery(id+"F2.wireOp",EDGE,"E11"),sQuery(id+"F2.wireOp",EDGE,"E12"),subQ1,sQuery(id+"F2.wireOp",EDGE,"E14"),subQ0,sQuery(id+"F2.wireOp",EDGE,"E16"),sQuery(id+"F2.wireOp",EDGE,"E17"),sQuery(id+"F2.wireOp",EDGE,"E18"),sQuery(id+"F2.wireOp",EDGE,"E19"),sQuery(id+"F2.wireOp",EDGE,"E20"),sQuery(id+"F2.wireOp",EDGE,"E21"),sQuery(id+"F2.wireOp",EDGE,"E22"),sQuery(id+"F2.wireOp",EDGE,"E23"),sQuery(id+"F2.wireOp",EDGE,"E24")])],"isStart":true})]});}
            var Q205;
            {var subQ0=sQuery(id+"F2.wireOp",EDGE,"E20");var subQ1=sQuery(id+"F2.wireOp",EDGE,"E18");Q205=makeQuery(id+"FPISK7QOFB9ojP9_2.opFillet","BLEND_EDGE",EDGE,{"blendedFrom":[makeQuery(id+"F3.opExtrude","CAP_VERTEX",VERTEX,{"disambiguationData":[OSD([subQ1,subQ0])],"isStart":true}),makeQuery(id+"F3.opExtrude","CAP_FACE",FACE,{"disambiguationData":[OSD([sQuery(id+"F2.wireOp",EDGE,"E7"),sQuery(id+"F2.wireOp",EDGE,"E8"),sQuery(id+"F2.wireOp",EDGE,"E9"),sQuery(id+"F2.wireOp",EDGE,"E10"),sQuery(id+"F2.wireOp",EDGE,"E11"),sQuery(id+"F2.wireOp",EDGE,"E12"),sQuery(id+"F2.wireOp",EDGE,"E13"),sQuery(id+"F2.wireOp",EDGE,"E14"),sQuery(id+"F2.wireOp",EDGE,"E15"),sQuery(id+"F2.wireOp",EDGE,"E16"),sQuery(id+"F2.wireOp",EDGE,"E17"),subQ1,sQuery(id+"F2.wireOp",EDGE,"E19"),subQ0,sQuery(id+"F2.wireOp",EDGE,"E21"),sQuery(id+"F2.wireOp",EDGE,"E22"),sQuery(id+"F2.wireOp",EDGE,"E23"),sQuery(id+"F2.wireOp",EDGE,"E24")])],"isStart":true})],"blendedInto":[makeQuery(id+"F3.opExtrude","CAP_FACE",FACE,{"disambiguationData":[OSD([sQuery(id+"F2.wireOp",EDGE,"E7"),sQuery(id+"F2.wireOp",EDGE,"E8"),sQuery(id+"F2.wireOp",EDGE,"E9"),sQuery(id+"F2.wireOp",EDGE,"E10"),sQuery(id+"F2.wireOp",EDGE,"E11"),sQuery(id+"F2.wireOp",EDGE,"E12"),sQuery(id+"F2.wireOp",EDGE,"E13"),sQuery(id+"F2.wireOp",EDGE,"E14"),sQuery(id+"F2.wireOp",EDGE,"E15"),sQuery(id+"F2.wireOp",EDGE,"E16"),sQuery(id+"F2.wireOp",EDGE,"E17"),subQ1,sQuery(id+"F2.wireOp",EDGE,"E19"),subQ0,sQuery(id+"F2.wireOp",EDGE,"E21"),sQuery(id+"F2.wireOp",EDGE,"E22"),sQuery(id+"F2.wireOp",EDGE,"E23"),sQuery(id+"F2.wireOp",EDGE,"E24")])],"isStart":true})]});}
            var Q206;
            {var subQ0=sQuery(id+"F2.wireOp",EDGE,"E12");var subQ1=sQuery(id+"F2.wireOp",EDGE,"E7");Q206=makeQuery(id+"FPISK7QOFB9ojP9_2.opFillet","BLEND_EDGE",EDGE,{"blendedFrom":[makeQuery(id+"F3.opExtrude","CAP_VERTEX",VERTEX,{"disambiguationData":[OSD([subQ1,subQ0])],"isStart":false}),makeQuery(id+"F3.opExtrude","SWEPT_EDGE",EDGE,{"disambiguationData":[OSD([subQ1,subQ0])]})],"blendedInto":[]});}
            var Q207;
            {var subQ0=sQuery(id+"F2.wireOp",EDGE,"E23");var subQ1=sQuery(id+"F2.wireOp",EDGE,"E20");Q207=makeQuery(id+"FPISK7QOFB9ojP9_2.opFillet","BLEND_EDGE",EDGE,{"blendedFrom":[makeQuery(id+"F3.opExtrude","CAP_VERTEX",VERTEX,{"disambiguationData":[OSD([subQ1,subQ0])],"isStart":true}),makeQuery(id+"F3.opExtrude","CAP_FACE",FACE,{"disambiguationData":[OSD([sQuery(id+"F2.wireOp",EDGE,"E7"),sQuery(id+"F2.wireOp",EDGE,"E8"),sQuery(id+"F2.wireOp",EDGE,"E9"),sQuery(id+"F2.wireOp",EDGE,"E10"),sQuery(id+"F2.wireOp",EDGE,"E11"),sQuery(id+"F2.wireOp",EDGE,"E12"),sQuery(id+"F2.wireOp",EDGE,"E13"),sQuery(id+"F2.wireOp",EDGE,"E14"),sQuery(id+"F2.wireOp",EDGE,"E15"),sQuery(id+"F2.wireOp",EDGE,"E16"),sQuery(id+"F2.wireOp",EDGE,"E17"),sQuery(id+"F2.wireOp",EDGE,"E18"),sQuery(id+"F2.wireOp",EDGE,"E19"),subQ1,sQuery(id+"F2.wireOp",EDGE,"E21"),sQuery(id+"F2.wireOp",EDGE,"E22"),subQ0,sQuery(id+"F2.wireOp",EDGE,"E24")])],"isStart":true})],"blendedInto":[makeQuery(id+"F3.opExtrude","CAP_FACE",FACE,{"disambiguationData":[OSD([sQuery(id+"F2.wireOp",EDGE,"E7"),sQuery(id+"F2.wireOp",EDGE,"E8"),sQuery(id+"F2.wireOp",EDGE,"E9"),sQuery(id+"F2.wireOp",EDGE,"E10"),sQuery(id+"F2.wireOp",EDGE,"E11"),sQuery(id+"F2.wireOp",EDGE,"E12"),sQuery(id+"F2.wireOp",EDGE,"E13"),sQuery(id+"F2.wireOp",EDGE,"E14"),sQuery(id+"F2.wireOp",EDGE,"E15"),sQuery(id+"F2.wireOp",EDGE,"E16"),sQuery(id+"F2.wireOp",EDGE,"E17"),sQuery(id+"F2.wireOp",EDGE,"E18"),sQuery(id+"F2.wireOp",EDGE,"E19"),subQ1,sQuery(id+"F2.wireOp",EDGE,"E21"),sQuery(id+"F2.wireOp",EDGE,"E22"),subQ0,sQuery(id+"F2.wireOp",EDGE,"E24")])],"isStart":true})]});}
            var Q208;
            {var subQ0=sQuery(id+"F2.wireOp",EDGE,"E18");var subQ1=sQuery(id+"F2.wireOp",EDGE,"E15");Q208=makeQuery(id+"FPISK7QOFB9ojP9_2.opFillet","BLEND_EDGE",EDGE,{"blendedFrom":[makeQuery(id+"F3.opExtrude","CAP_VERTEX",VERTEX,{"disambiguationData":[OSD([subQ1,subQ0])],"isStart":true}),makeQuery(id+"F3.opExtrude","CAP_FACE",FACE,{"disambiguationData":[OSD([sQuery(id+"F2.wireOp",EDGE,"E7"),sQuery(id+"F2.wireOp",EDGE,"E8"),sQuery(id+"F2.wireOp",EDGE,"E9"),sQuery(id+"F2.wireOp",EDGE,"E10"),sQuery(id+"F2.wireOp",EDGE,"E11"),sQuery(id+"F2.wireOp",EDGE,"E12"),sQuery(id+"F2.wireOp",EDGE,"E13"),sQuery(id+"F2.wireOp",EDGE,"E14"),subQ1,sQuery(id+"F2.wireOp",EDGE,"E16"),sQuery(id+"F2.wireOp",EDGE,"E17"),subQ0,sQuery(id+"F2.wireOp",EDGE,"E19"),sQuery(id+"F2.wireOp",EDGE,"E20"),sQuery(id+"F2.wireOp",EDGE,"E21"),sQuery(id+"F2.wireOp",EDGE,"E22"),sQuery(id+"F2.wireOp",EDGE,"E23"),sQuery(id+"F2.wireOp",EDGE,"E24")])],"isStart":true})],"blendedInto":[makeQuery(id+"F3.opExtrude","CAP_FACE",FACE,{"disambiguationData":[OSD([sQuery(id+"F2.wireOp",EDGE,"E7"),sQuery(id+"F2.wireOp",EDGE,"E8"),sQuery(id+"F2.wireOp",EDGE,"E9"),sQuery(id+"F2.wireOp",EDGE,"E10"),sQuery(id+"F2.wireOp",EDGE,"E11"),sQuery(id+"F2.wireOp",EDGE,"E12"),sQuery(id+"F2.wireOp",EDGE,"E13"),sQuery(id+"F2.wireOp",EDGE,"E14"),subQ1,sQuery(id+"F2.wireOp",EDGE,"E16"),sQuery(id+"F2.wireOp",EDGE,"E17"),subQ0,sQuery(id+"F2.wireOp",EDGE,"E19"),sQuery(id+"F2.wireOp",EDGE,"E20"),sQuery(id+"F2.wireOp",EDGE,"E21"),sQuery(id+"F2.wireOp",EDGE,"E22"),sQuery(id+"F2.wireOp",EDGE,"E23"),sQuery(id+"F2.wireOp",EDGE,"E24")])],"isStart":true})]});}
            var Q209;
            {var subQ0=sQuery(id+"F2.wireOp",EDGE,"E23");Q209=makeQuery(id+"FPISK7QOFB9ojP9_2.opFillet","BLEND_EDGE",EDGE,{"blendedFrom":[makeQuery(id+"F3.opExtrude","CAP_VERTEX",VERTEX,{"disambiguationData":[OSD([subQ0,sQuery(id+"F2.wireOp",EDGE,"E24")])],"isStart":true}),makeQuery(id+"F3.opExtrude","CAP_EDGE",EDGE,{"disambiguationData":[OSD([subQ0])],"isStart":true})],"blendedInto":[]});}
            var Q210;
            {var subQ0=sQuery(id+"F2.wireOp",EDGE,"E24");Q210=makeQuery(id+"FPISK7QOFB9ojP9_2.opFillet","BLEND_EDGE",EDGE,{"blendedFrom":[makeQuery(id+"F3.opExtrude","CAP_VERTEX",VERTEX,{"disambiguationData":[OSD([sQuery(id+"F2.wireOp",EDGE,"E11"),subQ0])],"isStart":false}),makeQuery(id+"F3.opExtrude","CAP_EDGE",EDGE,{"disambiguationData":[OSD([subQ0])],"isStart":false})],"blendedInto":[]});}
            var Q211;
            {var subQ0=sQuery(id+"F2.wireOp",EDGE,"E15");var subQ1=sQuery(id+"F2.wireOp",EDGE,"E13");Q211=makeQuery(id+"FPISK7QOFB9ojP9_2.opFillet","BLEND_EDGE",EDGE,{"blendedFrom":[makeQuery(id+"F3.opExtrude","CAP_VERTEX",VERTEX,{"disambiguationData":[OSD([subQ1,subQ0])],"isStart":false}),makeQuery(id+"F3.opExtrude","SWEPT_EDGE",EDGE,{"disambiguationData":[OSD([subQ1,subQ0])]})],"blendedInto":[]});}
            var Q212;
            {var subQ0=sQuery(id+"F2.wireOp",EDGE,"E24");Q212=makeQuery(id+"FPISK7QOFB9ojP9_2.opFillet","BLEND_EDGE",EDGE,{"blendedFrom":[makeQuery(id+"F3.opExtrude","CAP_EDGE",EDGE,{"disambiguationData":[OSD([subQ0])],"isStart":true}),makeQuery(id+"F3.opExtrude","CAP_FACE",FACE,{"disambiguationData":[OSD([sQuery(id+"F2.wireOp",EDGE,"E7"),sQuery(id+"F2.wireOp",EDGE,"E8"),sQuery(id+"F2.wireOp",EDGE,"E9"),sQuery(id+"F2.wireOp",EDGE,"E10"),sQuery(id+"F2.wireOp",EDGE,"E11"),sQuery(id+"F2.wireOp",EDGE,"E12"),sQuery(id+"F2.wireOp",EDGE,"E13"),sQuery(id+"F2.wireOp",EDGE,"E14"),sQuery(id+"F2.wireOp",EDGE,"E15"),sQuery(id+"F2.wireOp",EDGE,"E16"),sQuery(id+"F2.wireOp",EDGE,"E17"),sQuery(id+"F2.wireOp",EDGE,"E18"),sQuery(id+"F2.wireOp",EDGE,"E19"),sQuery(id+"F2.wireOp",EDGE,"E20"),sQuery(id+"F2.wireOp",EDGE,"E21"),sQuery(id+"F2.wireOp",EDGE,"E22"),sQuery(id+"F2.wireOp",EDGE,"E23"),subQ0])],"isStart":true})],"blendedInto":[makeQuery(id+"F3.opExtrude","CAP_FACE",FACE,{"disambiguationData":[OSD([sQuery(id+"F2.wireOp",EDGE,"E7"),sQuery(id+"F2.wireOp",EDGE,"E8"),sQuery(id+"F2.wireOp",EDGE,"E9"),sQuery(id+"F2.wireOp",EDGE,"E10"),sQuery(id+"F2.wireOp",EDGE,"E11"),sQuery(id+"F2.wireOp",EDGE,"E12"),sQuery(id+"F2.wireOp",EDGE,"E13"),sQuery(id+"F2.wireOp",EDGE,"E14"),sQuery(id+"F2.wireOp",EDGE,"E15"),sQuery(id+"F2.wireOp",EDGE,"E16"),sQuery(id+"F2.wireOp",EDGE,"E17"),sQuery(id+"F2.wireOp",EDGE,"E18"),sQuery(id+"F2.wireOp",EDGE,"E19"),sQuery(id+"F2.wireOp",EDGE,"E20"),sQuery(id+"F2.wireOp",EDGE,"E21"),sQuery(id+"F2.wireOp",EDGE,"E22"),sQuery(id+"F2.wireOp",EDGE,"E23"),subQ0])],"isStart":true})]});}
            var Q213;
            {var subQ0=sQuery(id+"F2.wireOp",EDGE,"E12");Q213=makeQuery(id+"FPISK7QOFB9ojP9_2.opFillet","BLEND_EDGE",EDGE,{"blendedFrom":[makeQuery(id+"F3.opExtrude","CAP_EDGE",EDGE,{"disambiguationData":[OSD([subQ0])],"isStart":true}),makeQuery(id+"F3.opExtrude","SWEPT_FACE",FACE,{"disambiguationData":[OSD([subQ0])]})],"blendedInto":[makeQuery(id+"F3.opExtrude","SWEPT_FACE",FACE,{"disambiguationData":[OSD([subQ0])]})]});}
            var Q214;
            {var subQ0=sQuery(id+"F2.wireOp",EDGE,"E22");var subQ1=sQuery(id+"F2.wireOp",EDGE,"E21");Q214=makeQuery(id+"FPISK7QOFB9ojP9_2.opFillet","BLEND_EDGE",EDGE,{"blendedFrom":[makeQuery(id+"F3.opExtrude","CAP_VERTEX",VERTEX,{"disambiguationData":[OSD([subQ1,subQ0])],"isStart":false}),makeQuery(id+"F3.opExtrude","SWEPT_EDGE",EDGE,{"disambiguationData":[OSD([subQ1,subQ0])]})],"blendedInto":[]});}
            var Q215;
            {var subQ0=sQuery(id+"F2.wireOp",EDGE,"E24");Q215=makeQuery(id+"FPISK7QOFB9ojP9_2.opFillet","BLEND_EDGE",EDGE,{"blendedFrom":[makeQuery(id+"F3.opExtrude","CAP_EDGE",EDGE,{"disambiguationData":[OSD([subQ0])],"isStart":false}),makeQuery(id+"F3.opExtrude","SWEPT_FACE",FACE,{"disambiguationData":[OSD([subQ0])]})],"blendedInto":[makeQuery(id+"F3.opExtrude","SWEPT_FACE",FACE,{"disambiguationData":[OSD([subQ0])]})]});}
            var Q216;
            {var subQ0=sQuery(id+"F2.wireOp",EDGE,"E18");Q216=makeQuery(id+"FPISK7QOFB9ojP9_2.opFillet","BLEND_EDGE",EDGE,{"blendedFrom":[makeQuery(id+"F3.opExtrude","CAP_VERTEX",VERTEX,{"disambiguationData":[OSD([subQ0,sQuery(id+"F2.wireOp",EDGE,"E20")])],"isStart":true}),makeQuery(id+"F3.opExtrude","CAP_EDGE",EDGE,{"disambiguationData":[OSD([subQ0])],"isStart":true})],"blendedInto":[]});}
            var Q217;
            {var subQ0=sQuery(id+"F2.wireOp",EDGE,"E17");var subQ1=sQuery(id+"F2.wireOp",EDGE,"E16");Q217=makeQuery(id+"FPISK7QOFB9ojP9_2.opFillet","BLEND_EDGE",EDGE,{"blendedFrom":[makeQuery(id+"F3.opExtrude","CAP_VERTEX",VERTEX,{"disambiguationData":[OSD([subQ1,subQ0])],"isStart":true}),makeQuery(id+"F3.opExtrude","SWEPT_EDGE",EDGE,{"disambiguationData":[OSD([subQ1,subQ0])]})],"blendedInto":[]});}
            var Q218;
            {var subQ0=sQuery(id+"F2.wireOp",EDGE,"E24");Q218=makeQuery(id+"FPISK7QOFB9ojP9_2.opFillet","BLEND_EDGE",EDGE,{"blendedFrom":[makeQuery(id+"F3.opExtrude","CAP_EDGE",EDGE,{"disambiguationData":[OSD([subQ0])],"isStart":true}),makeQuery(id+"F3.opExtrude","SWEPT_FACE",FACE,{"disambiguationData":[OSD([subQ0])]})],"blendedInto":[makeQuery(id+"F3.opExtrude","SWEPT_FACE",FACE,{"disambiguationData":[OSD([subQ0])]})]});}
            var Q219;
            {var subQ0=sQuery(id+"F2.wireOp",EDGE,"E13");Q219=makeQuery(id+"FPISK7QOFB9ojP9_2.opFillet","BLEND_EDGE",EDGE,{"blendedFrom":[makeQuery(id+"F3.opExtrude","CAP_VERTEX",VERTEX,{"disambiguationData":[OSD([subQ0,sQuery(id+"F2.wireOp",EDGE,"E15")])],"isStart":true}),makeQuery(id+"F3.opExtrude","CAP_EDGE",EDGE,{"disambiguationData":[OSD([subQ0])],"isStart":true})],"blendedInto":[]});}
            var Q220;
            {var subQ0=sQuery(id+"F2.wireOp",EDGE,"E17");Q220=makeQuery(id+"FPISK7QOFB9ojP9_2.opFillet","BLEND_EDGE",EDGE,{"blendedFrom":[makeQuery(id+"F3.opExtrude","CAP_VERTEX",VERTEX,{"disambiguationData":[OSD([sQuery(id+"F2.wireOp",EDGE,"E16"),subQ0])],"isStart":true}),makeQuery(id+"F3.opExtrude","CAP_EDGE",EDGE,{"disambiguationData":[OSD([sQuery(id+"F2.wireOp",EDGE,"E8"),subQ0])],"isStart":true})],"blendedInto":[]});}
            var Q221;
            {var subQ0=sQuery(id+"F2.wireOp",EDGE,"E24");Q221=makeQuery(id+"FPISK7QOFB9ojP9_2.opFillet","BLEND_EDGE",EDGE,{"blendedFrom":[makeQuery(id+"F3.opExtrude","CAP_VERTEX",VERTEX,{"disambiguationData":[OSD([sQuery(id+"F2.wireOp",EDGE,"E23"),subQ0])],"isStart":true}),makeQuery(id+"F3.opExtrude","CAP_EDGE",EDGE,{"disambiguationData":[OSD([subQ0])],"isStart":true})],"blendedInto":[]});}
            var Q222;
            {var subQ0=sQuery(id+"F2.wireOp",EDGE,"E12");Q222=makeQuery(id+"FPISK7QOFB9ojP9_2.opFillet","BLEND_EDGE",EDGE,{"blendedFrom":[makeQuery(id+"F3.opExtrude","CAP_EDGE",EDGE,{"disambiguationData":[OSD([subQ0])],"isStart":true}),makeQuery(id+"F3.opExtrude","CAP_FACE",FACE,{"disambiguationData":[OSD([sQuery(id+"F2.wireOp",EDGE,"E7"),sQuery(id+"F2.wireOp",EDGE,"E8"),sQuery(id+"F2.wireOp",EDGE,"E9"),sQuery(id+"F2.wireOp",EDGE,"E10"),sQuery(id+"F2.wireOp",EDGE,"E11"),subQ0,sQuery(id+"F2.wireOp",EDGE,"E13"),sQuery(id+"F2.wireOp",EDGE,"E14"),sQuery(id+"F2.wireOp",EDGE,"E15"),sQuery(id+"F2.wireOp",EDGE,"E16"),sQuery(id+"F2.wireOp",EDGE,"E17"),sQuery(id+"F2.wireOp",EDGE,"E18"),sQuery(id+"F2.wireOp",EDGE,"E19"),sQuery(id+"F2.wireOp",EDGE,"E20"),sQuery(id+"F2.wireOp",EDGE,"E21"),sQuery(id+"F2.wireOp",EDGE,"E22"),sQuery(id+"F2.wireOp",EDGE,"E23"),sQuery(id+"F2.wireOp",EDGE,"E24")])],"isStart":true})],"blendedInto":[makeQuery(id+"F3.opExtrude","CAP_FACE",FACE,{"disambiguationData":[OSD([sQuery(id+"F2.wireOp",EDGE,"E7"),sQuery(id+"F2.wireOp",EDGE,"E8"),sQuery(id+"F2.wireOp",EDGE,"E9"),sQuery(id+"F2.wireOp",EDGE,"E10"),sQuery(id+"F2.wireOp",EDGE,"E11"),subQ0,sQuery(id+"F2.wireOp",EDGE,"E13"),sQuery(id+"F2.wireOp",EDGE,"E14"),sQuery(id+"F2.wireOp",EDGE,"E15"),sQuery(id+"F2.wireOp",EDGE,"E16"),sQuery(id+"F2.wireOp",EDGE,"E17"),sQuery(id+"F2.wireOp",EDGE,"E18"),sQuery(id+"F2.wireOp",EDGE,"E19"),sQuery(id+"F2.wireOp",EDGE,"E20"),sQuery(id+"F2.wireOp",EDGE,"E21"),sQuery(id+"F2.wireOp",EDGE,"E22"),sQuery(id+"F2.wireOp",EDGE,"E23"),sQuery(id+"F2.wireOp",EDGE,"E24")])],"isStart":true})]});}
            var Q223;
            {var subQ0=sQuery(id+"F2.wireOp",EDGE,"E13");var subQ1=sQuery(id+"F2.wireOp",EDGE,"E12");Q223=makeQuery(id+"FPISK7QOFB9ojP9_2.opFillet","BLEND_EDGE",EDGE,{"blendedFrom":[makeQuery(id+"F3.opExtrude","CAP_VERTEX",VERTEX,{"disambiguationData":[OSD([subQ1,subQ0])],"isStart":true}),makeQuery(id+"F3.opExtrude","SWEPT_EDGE",EDGE,{"disambiguationData":[OSD([subQ1,subQ0])]})],"blendedInto":[]});}
            var Q224;
            {var subQ0=sQuery(id+"F2.wireOp",EDGE,"E24");var subQ1=sQuery(id+"F2.wireOp",EDGE,"E11");Q224=makeQuery(id+"FPISK7QOFB9ojP9_2.opFillet","BLEND_EDGE",EDGE,{"blendedFrom":[makeQuery(id+"F3.opExtrude","CAP_VERTEX",VERTEX,{"disambiguationData":[OSD([subQ1,subQ0])],"isStart":false}),makeQuery(id+"F3.opExtrude","SWEPT_EDGE",EDGE,{"disambiguationData":[OSD([subQ1,subQ0])]})],"blendedInto":[]});}
            var Q225;
            {var subQ0=sQuery(id+"F2.wireOp",EDGE,"E13");Q225=makeQuery(id+"FPISK7QOFB9ojP9_2.opFillet","BLEND_EDGE",EDGE,{"blendedFrom":[makeQuery(id+"F3.opExtrude","CAP_VERTEX",VERTEX,{"disambiguationData":[OSD([sQuery(id+"F2.wireOp",EDGE,"E12"),subQ0])],"isStart":true}),makeQuery(id+"F3.opExtrude","CAP_EDGE",EDGE,{"disambiguationData":[OSD([subQ0])],"isStart":true})],"blendedInto":[]});}
            fillet(context, id + "F4", {"entities" : qUnion([Q0, Q1, Q2, Q3, Q4, Q5, Q6, Q7, Q8, Q9, Q10, Q11, Q12, Q13, Q14, Q15, Q16, Q17, Q18, Q19, Q20, Q21, Q22, Q23, Q24, Q25, Q26, Q27, Q28, Q29, Q30, Q31, Q32, Q33, Q34, Q35, Q36, Q37, Q38, Q39, Q40, Q41, Q42, Q43, Q44, Q45, Q46, Q47, Q48, Q49, Q50, Q51, Q52, Q53, Q54, Q55, Q56, Q57, Q58, Q59, Q60, Q61, Q62, Q63, Q64, Q65, Q66, Q67, Q68, Q69, Q70, Q71, Q72, Q73, Q74, Q75, Q76, Q77, Q78, Q79, Q80, Q81, Q82, Q83, Q84, Q85, Q86, Q87, Q88, Q89, Q90, Q91, Q92, Q93, Q94, Q95, Q96, Q97, Q98, Q99, Q100, Q101, Q102, Q103, Q104, Q105, Q106, Q107, Q108, Q109, Q110, Q111, Q112, Q113, Q114, Q115, Q116, Q117, Q118, Q119, Q120, Q121, Q122, Q123, Q124, Q125, Q126, Q127, Q128, Q129, Q130, Q131, Q132, Q133, Q134, Q135, Q136, Q137, Q138, Q139, Q140, Q141, Q142, Q143, Q144, Q145, Q146, Q147, Q148, Q149, Q150, Q151, Q152, Q153, Q154, Q155, Q156, Q157, Q158, Q159, Q160, Q161, Q162, Q163, Q164, Q165, Q166, Q167, Q168, Q169, Q170, Q171, Q172, Q173, Q174, Q175, Q176, Q177, Q178, Q179, Q180, Q181, Q182, Q183, Q184, Q185, Q186, Q187, Q188, Q189, Q190, Q191, Q192, Q193, Q194, Q195, Q196, Q197, Q198, Q199, Q200, Q201, Q202, Q203, Q204, Q205, Q206, Q207, Q208, Q209, Q210, Q211, Q212, Q213, Q214, Q215, Q216, Q217, Q218, Q219, Q220, Q221, Q222, Q223, Q224, Q225]), "radius" : 0.5 * mm, "tangentPropagation" : true, "allowEdgeOverflow" : false});
        }
        {
            var Q0;
            Q0=qCreatedBy(makeId("Right.planeOp"),FACE);
            var sketch = newSketch(context, id + "F5", { "sketchPlane" : qUnion([Q0])});
            skLineSegment(sketch, "E25.bottom", {"start": v(46.97, 37) * mm, "end": v(60.18, 37) * mm});
            skLineSegment(sketch, "E25.top", {"start": v(46.97, 33.7) * mm, "end": v(60.18, 33.7) * mm});
            skLineSegment(sketch, "E25.left", {"start": v(46.97, 37) * mm, "end": v(46.97, 33.7) * mm});
            skLineSegment(sketch, "E25.right", {"start": v(60.18, 37) * mm, "end": v(60.18, 33.7) * mm});
            skSolve(sketch);
        }
        {
            var Q0;
            Q0=makeQuery(id+"F5.imprint","IMPRINT",FACE,{"disambiguationData":[TD([[makeQuery(id+"F5.imprint","IMPRINT",EDGE,{"derivedFrom":sQuery(id+"F5.wireOp",EDGE,"E25.bottom")}),-1.0]])]});
            extrude(context, id + "F6", {"entities" : qUnion([Q0]), "depth" : 12.7 * mm, "symmetric" : true});
        }
        {
            var Q0;
            Q0=qCreatedBy(makeId("Top.planeOp"),FACE);
            var sketch = newSketch(context, id + "F7", { "sketchPlane" : qUnion([Q0])});
            skCircle(sketch, "E26", {"center": v(44, 46.07) * mm, "radius": 3.18 * mm});
            skSolve(sketch);
        }
        {
            var Q0;
            Q0 = qSketchRegion(id + "F7", true);
            extrude(context, id + "F8", {"entities" : qUnion([Q0]), "depth" : 6.35 * mm});
        }
        {
            var Q0;
            Q0=makeQuery(id+"F6.opExtrude","SWEPT_FACE",FACE,{"disambiguationData":[OSD([sQuery(id+"F5.wireOp",EDGE,"E25.bottom")])]});
            var sketch = newSketch(context, id + "F9", { "sketchPlane" : qUnion([Q0])});
            skCircle(sketch, "E27", {"center": v(0, 53.58) * mm, "radius": 3.18 * mm});
            skPoint(sketch, "E27.centerSnap0", {"position": v(-6.35, 53.58) * mm});
            skPoint(sketch, "E27.centerSnap1", {"position": v(0, 60.18) * mm});
            skSolve(sketch);
        }
        {
            var Q0;
            Q0=makeQuery(id+"F9.imprint","IMPRINT",FACE,{"disambiguationData":[TD([[makeQuery(id+"F9.imprint","IMPRINT",EDGE,{"derivedFrom":sQuery(id+"F9.wireOp",EDGE,"E27")}),1.0]])]});
            var Q1;
            Q1=sQuery(id+"F9.wireOp",EDGE,"E27");
            extrude(context, id + "F10", {"entities" : qUnion([Q0]), "operationType" : NewBodyOperationType.ADD, "surfaceEntities" : qUnion([Q1]), "depth" : 6.35 * mm});
        }
        {
            var Q0;
            Q0=makeQuery(id+"F6.opExtrude","CAP_EDGE",EDGE,{"disambiguationData":[OSD([sQuery(id+"F5.wireOp",EDGE,"E25.bottom")])],"isStart":false});
            var Q1;
            Q1=makeQuery(id+"F6.opExtrude","SWEPT_FACE",FACE,{"disambiguationData":[OSD([sQuery(id+"F5.wireOp",EDGE,"E25.right")])]});
            var Q2;
            Q2=makeQuery(id+"F6.opExtrude","CAP_EDGE",EDGE,{"disambiguationData":[OSD([sQuery(id+"F5.wireOp",EDGE,"E25.top")])],"isStart":true});
            var Q3;
            Q3=makeQuery(id+"F6.opExtrude","CAP_EDGE",EDGE,{"disambiguationData":[OSD([sQuery(id+"F5.wireOp",EDGE,"E25.top")])],"isStart":false});
            var Q4;
            Q4=makeQuery(id+"F10.opExtrude","SWEPT_FACE",FACE,{"disambiguationData":[OSD([sQuery(id+"F9.wireOp",EDGE,"E27")])]});
            var Q5;
            Q5=makeQuery(id+"F10.opExtrude","CAP_EDGE",EDGE,{"disambiguationData":[OSD([sQuery(id+"F9.wireOp",EDGE,"E27")])],"isStart":false});
            var Q6;
            Q6=makeQuery(id+"F10.opExtrude","CAP_EDGE",EDGE,{"disambiguationData":[OSD([sQuery(id+"F9.wireOp",EDGE,"E27")])],"isStart":true});
            var Q7;
            Q7=makeQuery(id+"F6.opExtrude","CAP_EDGE",EDGE,{"disambiguationData":[OSD([sQuery(id+"F5.wireOp",EDGE,"E25.left")])],"isStart":false});
            var Q8;
            Q8=makeQuery(id+"F6.opExtrude","SWEPT_EDGE",EDGE,{"disambiguationData":[OSD([sQuery(id+"F5.wireOp",EDGE,"E25.bottom"),sQuery(id+"F5.wireOp",EDGE,"E25.right")])]});
            var Q9;
            Q9=makeQuery(id+"F10.opExtrude","CAP_FACE",FACE,{"disambiguationData":[OSD([sQuery(id+"F9.wireOp",EDGE,"E27")])],"isStart":false});
            var Q10;
            Q10=makeQuery(id+"F6.opExtrude","SWEPT_EDGE",EDGE,{"disambiguationData":[OSD([sQuery(id+"F5.wireOp",EDGE,"E25.top"),sQuery(id+"F5.wireOp",EDGE,"E25.left")])]});
            var Q11;
            Q11=makeQuery(id+"F6.opExtrude","CAP_FACE",FACE,{"disambiguationData":[OSD([sQuery(id+"F5.wireOp",EDGE,"E25.bottom"),sQuery(id+"F5.wireOp",EDGE,"E25.top"),sQuery(id+"F5.wireOp",EDGE,"E25.left"),sQuery(id+"F5.wireOp",EDGE,"E25.right")])],"isStart":false});
            var Q12;
            Q12=makeQuery(id+"F6.opExtrude","SWEPT_EDGE",EDGE,{"disambiguationData":[OSD([sQuery(id+"F5.wireOp",EDGE,"E25.top"),sQuery(id+"F5.wireOp",EDGE,"E25.right")])]});
            var Q13;
            Q13=makeQuery(id+"F6.opExtrude","SWEPT_FACE",FACE,{"disambiguationData":[OSD([sQuery(id+"F5.wireOp",EDGE,"E25.top")])]});
            var Q14;
            Q14=makeQuery(id+"F6.opExtrude","CAP_EDGE",EDGE,{"disambiguationData":[OSD([sQuery(id+"F5.wireOp",EDGE,"E25.right")])],"isStart":true});
            var Q15;
            Q15=makeQuery(id+"F6.opExtrude","CAP_EDGE",EDGE,{"disambiguationData":[OSD([sQuery(id+"F5.wireOp",EDGE,"E25.right")])],"isStart":false});
            var Q16;
            Q16=makeQuery(id+"F6.opExtrude","SWEPT_FACE",FACE,{"disambiguationData":[OSD([sQuery(id+"F5.wireOp",EDGE,"E25.bottom")])]});
            var Q17;
            Q17=makeQuery(id+"F6.opExtrude","CAP_FACE",FACE,{"disambiguationData":[OSD([sQuery(id+"F5.wireOp",EDGE,"E25.bottom"),sQuery(id+"F5.wireOp",EDGE,"E25.top"),sQuery(id+"F5.wireOp",EDGE,"E25.left"),sQuery(id+"F5.wireOp",EDGE,"E25.right")])],"isStart":true});
            var Q18;
            Q18=makeQuery(id+"F6.opExtrude","CAP_EDGE",EDGE,{"disambiguationData":[OSD([sQuery(id+"F5.wireOp",EDGE,"E25.bottom")])],"isStart":true});
            var Q19;
            Q19=makeQuery(id+"F6.opExtrude","SWEPT_FACE",FACE,{"disambiguationData":[OSD([sQuery(id+"F5.wireOp",EDGE,"E25.left")])]});
            var Q20;
            Q20=makeQuery(id+"F6.opExtrude","SWEPT_EDGE",EDGE,{"disambiguationData":[OSD([sQuery(id+"F5.wireOp",EDGE,"E25.bottom"),sQuery(id+"F5.wireOp",EDGE,"E25.left")])]});
            var Q21;
            Q21=makeQuery(id+"F6.opExtrude","CAP_EDGE",EDGE,{"disambiguationData":[OSD([sQuery(id+"F5.wireOp",EDGE,"E25.left")])],"isStart":true});
            fillet(context, id + "F11", {"entities" : qUnion([Q0, Q1, Q2, Q3, Q4, Q5, Q6, Q7, Q8, Q9, Q10, Q11, Q12, Q13, Q14, Q15, Q16, Q17, Q18, Q19, Q20, Q21]), "radius" : 1.27 * mm, "tangentPropagation" : true, "allowEdgeOverflow" : false});
        }
        {
            var Q0;
            Q0=qCreatedBy(makeId("Top.planeOp"),FACE);
            var sketch = newSketch(context, id + "F12", { "sketchPlane" : qUnion([Q0])});
            skLineSegment(sketch, "E28.bottom", {"start": v(0, 15.93) * mm, "end": v(-25.4, 15.93) * mm});
            skLineSegment(sketch, "E28.top", {"start": v(0, 28.63) * mm, "end": v(-25.4, 28.63) * mm});
            skLineSegment(sketch, "E28.left", {"start": v(0, 15.93) * mm, "end": v(0, 28.63) * mm});
            skLineSegment(sketch, "E28.right", {"start": v(-25.4, 15.93) * mm, "end": v(-25.4, 28.63) * mm});
            skCircle(sketch, "E29", {"center": v(0, 22.28) * mm, "radius": 6.35 * mm});
            skCircle(sketch, "E30", {"center": v(-25.4, 22.28) * mm, "radius": 6.35 * mm});
            skCircle(sketch, "E31", {"center": v(-25.4, 22.28) * mm, "radius": 3.18 * mm});
            skCircle(sketch, "E32", {"center": v(0, 22.28) * mm, "radius": 3.18 * mm});
            skSolve(sketch);
        }
        {
            var Q0;
            {var subQ0=sQuery(id+"F12.wireOp",EDGE,"E28.bottom");Q0=makeQuery(id+"F12.imprint","IMPRINT",FACE,{"disambiguationData":[TD([[makeQuery(id+"F12.imprint","IMPRINT",EDGE,{"derivedFrom":subQ0}),-1.0]])]});}
            var Q1;
            {var subQ1=sQuery(id+"F12.wireOp",EDGE,"E28.right");var subQ3=sQuery(id+"F12.wireOp",EDGE,"E31");var subQ4=makeQuery(id+"F12.imprint","INTERSECT",VERTEX,{"disambiguationData":[OD(0.0)],"derivedFrom":[subQ1,subQ3]});Q1=makeQuery(id+"F12.imprint","IMPRINT",FACE,{"disambiguationData":[TD([[makeQuery(id+"F12.imprint","IMPRINT",EDGE,{"disambiguationData":[TD([[subQ4,-1.0]])],"derivedFrom":subQ3}),-1.0]])]});}
            var Q2;
            {var subQ1=sQuery(id+"F12.wireOp",EDGE,"E28.right");var subQ3=sQuery(id+"F12.wireOp",EDGE,"E31");var subQ4=makeQuery(id+"F12.imprint","INTERSECT",VERTEX,{"disambiguationData":[OD(0.0)],"derivedFrom":[subQ1,subQ3]});Q2=makeQuery(id+"F12.imprint","IMPRINT",FACE,{"disambiguationData":[TD([[makeQuery(id+"F12.imprint","IMPRINT",EDGE,{"disambiguationData":[TD([[subQ4,1.0]])],"derivedFrom":subQ3}),-1.0]])]});}
            var Q3;
            {var subQ1=sQuery(id+"F12.wireOp",EDGE,"E28.left");var subQ3=sQuery(id+"F12.wireOp",EDGE,"E32");var subQ4=makeQuery(id+"F12.imprint","INTERSECT",VERTEX,{"disambiguationData":[OD(0.0)],"derivedFrom":[subQ1,subQ3]});Q3=makeQuery(id+"F12.imprint","IMPRINT",FACE,{"disambiguationData":[TD([[makeQuery(id+"F12.imprint","IMPRINT",EDGE,{"disambiguationData":[TD([[subQ4,1.0]])],"derivedFrom":subQ3}),-1.0]])]});}
            var Q4;
            {var subQ1=sQuery(id+"F12.wireOp",EDGE,"E28.left");var subQ3=sQuery(id+"F12.wireOp",EDGE,"E32");var subQ4=makeQuery(id+"F12.imprint","INTERSECT",VERTEX,{"disambiguationData":[OD(0.0)],"derivedFrom":[subQ1,subQ3]});Q4=makeQuery(id+"F12.imprint","IMPRINT",FACE,{"disambiguationData":[TD([[makeQuery(id+"F12.imprint","IMPRINT",EDGE,{"disambiguationData":[TD([[subQ4,-1.0]])],"derivedFrom":subQ3}),-1.0]])]});}
            extrude(context, id + "F13", {"entities" : qUnion([Q0, Q1, Q2, Q3, Q4]), "depth" : 2.54 * mm});
        }
        {
            var Q0;
            Q0=makeQuery(id+"F3.opExtrude","SWEPT_FACE",FACE,{"disambiguationData":[OSD([sQuery(id+"F2.wireOp",EDGE,"E10"),sQuery(id+"F2.wireOp",EDGE,"E22")])]});
            var sketch = newSketch(context, id + "F14", { "sketchPlane" : qUnion([Q0])});
            skLineSegment(sketch, "E33", {"start": v(-0.5, 33.64) * mm, "end": v(-25.9, 33.64) * mm});
            skLineSegment(sketch, "E34", {"start": v(-25.9, 33.64) * mm, "end": v(-25.9, 28.3) * mm});
            skLineSegment(sketch, "E35.bottom", {"start": v(-51.3, 33.64) * mm, "end": v(-25.9, 33.64) * mm});
            skLineSegment(sketch, "E35.top", {"start": v(-51.3, 28.3) * mm, "end": v(-25.9, 28.3) * mm});
            skLineSegment(sketch, "E35.left", {"start": v(-51.3, 33.64) * mm, "end": v(-51.3, 28.3) * mm});
            skSolve(sketch);
        }
        {
            var Q0;
            Q0=makeQuery(id+"F14.imprint","IMPRINT",FACE,{"disambiguationData":[TD([[makeQuery(id+"F14.imprint","IMPRINT",EDGE,{"derivedFrom":sQuery(id+"F14.wireOp",EDGE,"E35.bottom")}),1.0]])]});
            extrude(context, id + "F15", {"entities" : qUnion([Q0]), "operationType" : NewBodyOperationType.ADD, "depth" : 7.62 * mm});
        }
        {
            var Q0;
            Q0=makeQuery(id+"F15.opExtrude","SWEPT_FACE",FACE,{"disambiguationData":[OSD([sQuery(id+"F14.wireOp",EDGE,"E35.bottom")])]});
            var sketch = newSketch(context, id + "F16", { "sketchPlane" : qUnion([Q0])});
            skLineSegment(sketch, "E36.bottom", {"start": v(28.45, 8.83) * mm, "end": v(48.77, 8.83) * mm});
            skLineSegment(sketch, "E36.top", {"start": v(28.45, 6.3) * mm, "end": v(48.77, 6.3) * mm});
            skLineSegment(sketch, "E36.left", {"start": v(28.45, 8.83) * mm, "end": v(28.45, 6.3) * mm});
            skLineSegment(sketch, "E36.right", {"start": v(48.77, 8.83) * mm, "end": v(48.77, 6.3) * mm});
            skPoint(sketch, "E36.middle", {"position": v(38.6, 7.56) * mm});
            skPoint(sketch, "E36.middle.positionSnap0", {"position": v(25.9, 7.56) * mm});
            skPoint(sketch, "E36.middle.positionSnap1", {"position": v(38.6, 11.37) * mm});
            skPoint(sketch, "E36.centerSnap0", {"position": v(25.9, 7.56) * mm});
            skPoint(sketch, "E36.centerSnap1", {"position": v(38.6, 11.37) * mm});
            skSolve(sketch);
        }
        {
            var Q0;
            Q0=makeQuery(id+"F16.imprint","IMPRINT",FACE,{"disambiguationData":[TD([[makeQuery(id+"F16.imprint","IMPRINT",EDGE,{"derivedFrom":sQuery(id+"F16.wireOp",EDGE,"E36.bottom")}),-1.0]])]});
            extrude(context, id + "F17", {"entities" : qUnion([Q0]), "operationType" : NewBodyOperationType.REMOVE, "endBound" : BoundingType.THROUGH_ALL, "oppositeDirection" : true, "depth" : 25.4 * mm});
        }
        {
            var Q0;
            Q0=makeQuery(id+"F15.opExtrude","SWEPT_EDGE",EDGE,{"disambiguationData":[OSD([sQuery(id+"F14.wireOp",EDGE,"E33"),sQuery(id+"F14.wireOp",EDGE,"E35.bottom"),sQuery(id+"F14.wireOp",EDGE,"E34")])]});
            var Q1;
            Q1=makeQuery(id+"F15.opExtrude","SWEPT_EDGE",EDGE,{"disambiguationData":[OSD([sQuery(id+"F2.wireOp",EDGE,"E10"),sQuery(id+"F2.wireOp",EDGE,"E21"),sQuery(id+"F2.wireOp",EDGE,"E22"),sQuery(id+"F14.wireOp",EDGE,"E35.bottom"),sQuery(id+"F14.wireOp",EDGE,"E35.left")])]});
            var Q2;
            Q2=makeQuery(id+"F15.opExtrude","SWEPT_EDGE",EDGE,{"disambiguationData":[OSD([sQuery(id+"F2.wireOp",EDGE,"E10"),sQuery(id+"F2.wireOp",EDGE,"E19"),sQuery(id+"F2.wireOp",EDGE,"E22"),sQuery(id+"F14.wireOp",EDGE,"E35.top"),sQuery(id+"F14.wireOp",EDGE,"E34")])]});
            var Q3;
            Q3=makeQuery(id+"F15.opExtrude","CAP_EDGE",EDGE,{"disambiguationData":[OSD([sQuery(id+"F14.wireOp",EDGE,"E35.top")])],"isStart":false});
            var Q4;
            Q4=makeQuery(id+"F15.opExtrude","SWEPT_EDGE",EDGE,{"disambiguationData":[OSD([sQuery(id+"F2.wireOp",EDGE,"E10"),sQuery(id+"F2.wireOp",EDGE,"E19"),sQuery(id+"F2.wireOp",EDGE,"E22"),sQuery(id+"F14.wireOp",EDGE,"E35.top"),sQuery(id+"F14.wireOp",EDGE,"E35.left")])]});
            var Q5;
            Q5=makeQuery(id+"F15.opExtrude","CAP_EDGE",EDGE,{"disambiguationData":[OSD([sQuery(id+"F14.wireOp",EDGE,"E35.bottom")])],"isStart":false});
            var Q6;
            Q6=makeQuery(id+"F15.opExtrude","CAP_EDGE",EDGE,{"disambiguationData":[OSD([sQuery(id+"F14.wireOp",EDGE,"E35.left")])],"isStart":false});
            var Q7;
            Q7=makeQuery(id+"F15.opExtrude","CAP_EDGE",EDGE,{"disambiguationData":[OSD([sQuery(id+"F14.wireOp",EDGE,"E34")])],"isStart":false});
            fillet(context, id + "F18", {"entities" : qUnion([Q0, Q1, Q2, Q3, Q4, Q5, Q6, Q7]), "radius" : 2.54 * mm, "tangentPropagation" : true, "allowEdgeOverflow" : false});
        }
        {
            var Q0;
            Q0=makeQuery(id+"F3.opExtrude","SWEPT_FACE",FACE,{"disambiguationData":[OSD([sQuery(id+"F2.wireOp",EDGE,"E8"),sQuery(id+"F2.wireOp",EDGE,"E17")])]});
            var sketch = newSketch(context, id + "F19", { "sketchPlane" : qUnion([Q0])});
            skLineSegment(sketch, "E37", {"start": v(0.5, 33.64) * mm, "end": v(25.9, 33.64) * mm});
            skLineSegment(sketch, "E38", {"start": v(25.9, 33.64) * mm, "end": v(25.9, 28.3) * mm});
            skLineSegment(sketch, "E39", {"start": v(25.9, 28.3) * mm, "end": v(51.3, 28.3) * mm});
            skLineSegment(sketch, "E40", {"start": v(51.3, 28.3) * mm, "end": v(51.3, 33.64) * mm});
            skLineSegment(sketch, "E41", {"start": v(51.3, 33.64) * mm, "end": v(25.9, 33.64) * mm});
            skSolve(sketch);
        }
        {
            var Q0;
            Q0=makeQuery(id+"F19.imprint","IMPRINT",FACE,{"disambiguationData":[TD([[makeQuery(id+"F19.imprint","IMPRINT",EDGE,{"derivedFrom":sQuery(id+"F19.wireOp",EDGE,"E38")}),1.0]])]});
            extrude(context, id + "F20", {"entities" : qUnion([Q0]), "operationType" : NewBodyOperationType.ADD, "depth" : 7.62 * mm});
        }
        {
            var Q0;
            Q0=makeQuery(id+"F20.opExtrude","SWEPT_FACE",FACE,{"disambiguationData":[OSD([sQuery(id+"F19.wireOp",EDGE,"E41")])]});
            var sketch = newSketch(context, id + "F21", { "sketchPlane" : qUnion([Q0])});
            skLineSegment(sketch, "E42.bottom", {"start": v(28.45, -17.84) * mm, "end": v(48.77, -17.84) * mm});
            skLineSegment(sketch, "E42.top", {"start": v(28.45, -20.38) * mm, "end": v(48.77, -20.38) * mm});
            skLineSegment(sketch, "E42.left", {"start": v(28.45, -17.84) * mm, "end": v(28.45, -20.38) * mm});
            skLineSegment(sketch, "E42.right", {"start": v(48.77, -17.84) * mm, "end": v(48.77, -20.38) * mm});
            skPoint(sketch, "E42.middle", {"position": v(38.6, -19.1) * mm});
            skPoint(sketch, "E42.middle.positionSnap0", {"position": v(25.9, -19.1) * mm});
            skPoint(sketch, "E42.middle.positionSnap1", {"position": v(38.6, -15.3) * mm});
            skPoint(sketch, "E42.centerSnap0", {"position": v(25.9, -19.1) * mm});
            skPoint(sketch, "E42.centerSnap1", {"position": v(38.6, -15.3) * mm});
            skSolve(sketch);
        }
        {
            var Q0;
            Q0=makeQuery(id+"F21.imprint","IMPRINT",FACE,{"disambiguationData":[TD([[makeQuery(id+"F21.imprint","IMPRINT",EDGE,{"derivedFrom":sQuery(id+"F21.wireOp",EDGE,"E42.bottom")}),-1.0]])]});
            extrude(context, id + "F22", {"entities" : qUnion([Q0]), "operationType" : NewBodyOperationType.REMOVE, "endBound" : BoundingType.THROUGH_ALL, "oppositeDirection" : true, "depth" : 25.4 * mm});
        }
        {
            var Q0;
            Q0=makeQuery(id+"F20.opExtrude","CAP_EDGE",EDGE,{"disambiguationData":[OSD([sQuery(id+"F19.wireOp",EDGE,"E40")])],"isStart":false});
            var Q1;
            Q1=makeQuery(id+"F20.opExtrude","SWEPT_EDGE",EDGE,{"disambiguationData":[OSD([sQuery(id+"F2.wireOp",EDGE,"E8"),sQuery(id+"F2.wireOp",EDGE,"E14"),sQuery(id+"F2.wireOp",EDGE,"E17"),sQuery(id+"F19.wireOp",EDGE,"E40"),sQuery(id+"F19.wireOp",EDGE,"E41")])]});
            var Q2;
            Q2=makeQuery(id+"F20.opExtrude","SWEPT_EDGE",EDGE,{"disambiguationData":[OSD([sQuery(id+"F2.wireOp",EDGE,"E8"),sQuery(id+"F2.wireOp",EDGE,"E16"),sQuery(id+"F2.wireOp",EDGE,"E17"),sQuery(id+"F19.wireOp",EDGE,"E39"),sQuery(id+"F19.wireOp",EDGE,"E40")])]});
            var Q3;
            Q3=makeQuery(id+"F20.opExtrude","CAP_EDGE",EDGE,{"disambiguationData":[OSD([sQuery(id+"F19.wireOp",EDGE,"E41")])],"isStart":false});
            var Q4;
            Q4=makeQuery(id+"F20.opExtrude","CAP_EDGE",EDGE,{"disambiguationData":[OSD([sQuery(id+"F19.wireOp",EDGE,"E39")])],"isStart":false});
            var Q5;
            Q5=makeQuery(id+"F20.opExtrude","CAP_EDGE",EDGE,{"disambiguationData":[OSD([sQuery(id+"F19.wireOp",EDGE,"E38")])],"isStart":false});
            var Q6;
            Q6=makeQuery(id+"F20.opExtrude","SWEPT_EDGE",EDGE,{"disambiguationData":[OSD([sQuery(id+"F2.wireOp",EDGE,"E8"),sQuery(id+"F2.wireOp",EDGE,"E16"),sQuery(id+"F2.wireOp",EDGE,"E17"),sQuery(id+"F19.wireOp",EDGE,"E38"),sQuery(id+"F19.wireOp",EDGE,"E39")])]});
            var Q7;
            Q7=makeQuery(id+"F20.opExtrude","SWEPT_EDGE",EDGE,{"disambiguationData":[OSD([sQuery(id+"F19.wireOp",EDGE,"E37"),sQuery(id+"F19.wireOp",EDGE,"E38"),sQuery(id+"F19.wireOp",EDGE,"E41")])]});
            fillet(context, id + "F23", {"entities" : qUnion([Q0, Q1, Q2, Q3, Q4, Q5, Q6, Q7]), "radius" : 2.54 * mm, "tangentPropagation" : true, "allowEdgeOverflow" : false});
        }
        {
            var Q0;
            {var subQ0=sQuery(id+"F2.wireOp",EDGE,"E17");var subQ3=sQuery(id+"F2.wireOp",EDGE,"E8");Q0=makeQuery(id+"F20.boolean.opBoolean","SPLIT",FACE,{"disambiguationData":[TD([makeQuery(id+"F20.opExtrude","SWEPT_FACE",FACE,{"disambiguationData":[OSD([sQuery(id+"F19.wireOp",EDGE,"E40")])]})])],"derivedFrom":makeQuery(id+"F3.opExtrude","SWEPT_FACE",FACE,{"disambiguationData":[OSD([subQ3,subQ0])]})});}
            var sketch = newSketch(context, id + "F24", { "sketchPlane" : qUnion([Q0])});
            skLineSegment(sketch, "E43", {"start": v(202.7, 33.64) * mm, "end": v(177.3, 33.64) * mm});
            skLineSegment(sketch, "E44", {"start": v(177.3, 33.64) * mm, "end": v(177.3, 28.3) * mm});
            skLineSegment(sketch, "E45", {"start": v(177.3, 28.3) * mm, "end": v(151.9, 28.3) * mm});
            skLineSegment(sketch, "E46", {"start": v(151.9, 28.3) * mm, "end": v(151.9, 33.64) * mm});
            skLineSegment(sketch, "E47", {"start": v(151.9, 33.64) * mm, "end": v(177.3, 33.64) * mm});
            skSolve(sketch);
        }
        {
            var Q0;
            Q0=makeQuery(id+"F24.imprint","IMPRINT",FACE,{"disambiguationData":[TD([[makeQuery(id+"F24.imprint","IMPRINT",EDGE,{"derivedFrom":sQuery(id+"F24.wireOp",EDGE,"E44")}),-1.0]])]});
            extrude(context, id + "F25", {"entities" : qUnion([Q0]), "operationType" : NewBodyOperationType.ADD, "depth" : 7.62 * mm});
        }
        {
            var Q0;
            Q0=makeQuery(id+"F25.opExtrude","SWEPT_FACE",FACE,{"disambiguationData":[OSD([sQuery(id+"F24.wireOp",EDGE,"E47")])]});
            var sketch = newSketch(context, id + "F26", { "sketchPlane" : qUnion([Q0])});
            skLineSegment(sketch, "E48.bottom", {"start": v(154.43, -17.84) * mm, "end": v(174.75, -17.84) * mm});
            skLineSegment(sketch, "E48.top", {"start": v(154.43, -20.38) * mm, "end": v(174.75, -20.38) * mm});
            skLineSegment(sketch, "E48.left", {"start": v(154.43, -17.84) * mm, "end": v(154.43, -20.38) * mm});
            skLineSegment(sketch, "E48.right", {"start": v(174.75, -17.84) * mm, "end": v(174.75, -20.38) * mm});
            skPoint(sketch, "E48.middle", {"position": v(164.6, -19.1) * mm});
            skPoint(sketch, "E48.middle.positionSnap0", {"position": v(151.9, -19.1) * mm});
            skPoint(sketch, "E48.middle.positionSnap1", {"position": v(164.6, -15.3) * mm});
            skPoint(sketch, "E48.centerSnap0", {"position": v(151.9, -19.1) * mm});
            skPoint(sketch, "E48.centerSnap1", {"position": v(164.6, -15.3) * mm});
            skSolve(sketch);
        }
        {
            var Q0;
            Q0=makeQuery(id+"F26.imprint","IMPRINT",FACE,{"disambiguationData":[TD([[makeQuery(id+"F26.imprint","IMPRINT",EDGE,{"derivedFrom":sQuery(id+"F26.wireOp",EDGE,"E48.bottom")}),-1.0]])]});
            extrude(context, id + "F27", {"entities" : qUnion([Q0]), "operationType" : NewBodyOperationType.REMOVE, "endBound" : BoundingType.THROUGH_ALL, "oppositeDirection" : true, "depth" : 25.4 * mm});
        }
        {
            var Q0;
            Q0=makeQuery(id+"F25.opExtrude","CAP_EDGE",EDGE,{"disambiguationData":[OSD([sQuery(id+"F24.wireOp",EDGE,"E44")])],"isStart":false});
            var Q1;
            Q1=makeQuery(id+"F25.opExtrude","SWEPT_EDGE",EDGE,{"disambiguationData":[OSD([sQuery(id+"F24.wireOp",EDGE,"E43"),sQuery(id+"F24.wireOp",EDGE,"E44"),sQuery(id+"F24.wireOp",EDGE,"E47")])]});
            var Q2;
            Q2=makeQuery(id+"F25.opExtrude","SWEPT_EDGE",EDGE,{"disambiguationData":[OSD([sQuery(id+"F2.wireOp",EDGE,"E8"),sQuery(id+"F2.wireOp",EDGE,"E16"),sQuery(id+"F2.wireOp",EDGE,"E17"),sQuery(id+"F24.wireOp",EDGE,"E44"),sQuery(id+"F24.wireOp",EDGE,"E45")])]});
            var Q3;
            Q3=makeQuery(id+"F25.opExtrude","CAP_EDGE",EDGE,{"disambiguationData":[OSD([sQuery(id+"F24.wireOp",EDGE,"E47")])],"isStart":false});
            var Q4;
            Q4=makeQuery(id+"F25.opExtrude","CAP_EDGE",EDGE,{"disambiguationData":[OSD([sQuery(id+"F24.wireOp",EDGE,"E45")])],"isStart":false});
            var Q5;
            Q5=makeQuery(id+"F25.opExtrude","CAP_EDGE",EDGE,{"disambiguationData":[OSD([sQuery(id+"F24.wireOp",EDGE,"E46")])],"isStart":false});
            var Q6;
            Q6=makeQuery(id+"F25.opExtrude","SWEPT_EDGE",EDGE,{"disambiguationData":[OSD([sQuery(id+"F2.wireOp",EDGE,"E8"),sQuery(id+"F2.wireOp",EDGE,"E14"),sQuery(id+"F2.wireOp",EDGE,"E17"),sQuery(id+"F24.wireOp",EDGE,"E46"),sQuery(id+"F24.wireOp",EDGE,"E47")])]});
            var Q7;
            Q7=makeQuery(id+"F25.opExtrude","SWEPT_EDGE",EDGE,{"disambiguationData":[OSD([sQuery(id+"F2.wireOp",EDGE,"E8"),sQuery(id+"F2.wireOp",EDGE,"E16"),sQuery(id+"F2.wireOp",EDGE,"E17"),sQuery(id+"F24.wireOp",EDGE,"E45"),sQuery(id+"F24.wireOp",EDGE,"E46")])]});
            var Q8;
            {var subQ0=sQuery(id+"F2.wireOp",EDGE,"E22");var subQ3=sQuery(id+"F2.wireOp",EDGE,"E10");Q8=makeQuery(id+"F15.boolean.opBoolean","SPLIT",FACE,{"disambiguationData":[TD([makeQuery(id+"F15.opExtrude","SWEPT_FACE",FACE,{"disambiguationData":[OSD([sQuery(id+"F14.wireOp",EDGE,"E35.left")])]})])],"derivedFrom":makeQuery(id+"F3.opExtrude","SWEPT_FACE",FACE,{"disambiguationData":[OSD([subQ3,subQ0])]})});}
            fillet(context, id + "F28", {"entities" : qUnion([Q0, Q1, Q2, Q3, Q4, Q5, Q6, Q7, Q8]), "radius" : 2.54 * mm, "tangentPropagation" : true, "allowEdgeOverflow" : false});
        }
        {
            var Q0;
            {var subQ0=sQuery(id+"F14.wireOp",EDGE,"E35.left");Q0=makeQuery(id+"F14.imprint","IMPRINT",FACE,{"disambiguationData":[TD([[makeQuery(id+"F14.imprint","IMPRINT",EDGE,{"derivedFrom":subQ0}),-1.0]])]});}
            var sketch = newSketch(context, id + "F29", { "sketchPlane" : qUnion([Q0])});
            skLineSegment(sketch, "E49", {"start": v(-202.66, 33.46) * mm, "end": v(-177.26, 33.46) * mm});
            skLineSegment(sketch, "E50", {"start": v(-177.26, 33.46) * mm, "end": v(-177.26, 28.13) * mm});
            skLineSegment(sketch, "E51", {"start": v(-177.26, 28.13) * mm, "end": v(-151.86, 28.13) * mm});
            skLineSegment(sketch, "E52", {"start": v(-151.86, 28.13) * mm, "end": v(-151.86, 33.46) * mm});
            skLineSegment(sketch, "E53", {"start": v(-151.86, 33.46) * mm, "end": v(-177.26, 33.46) * mm});
            skSolve(sketch);
        }
        {
            var Q0;
            {var subQ0=sQuery(id+"F29.wireOp",EDGE,"E53");Q0=makeQuery(id+"F29.imprint","IMPRINT",FACE,{"disambiguationData":[TD([[makeQuery(id+"F29.imprint","IMPRINT",EDGE,{"derivedFrom":subQ0}),1.0]])]});}
            extrude(context, id + "F30", {"entities" : qUnion([Q0]), "operationType" : NewBodyOperationType.ADD, "depth" : 7.62 * mm});
        }
        {
            var Q0;
            Q0=makeQuery(id+"F30.opExtrude","SWEPT_FACE",FACE,{"disambiguationData":[OSD([sQuery(id+"F29.wireOp",EDGE,"E53")])]});
            var sketch = newSketch(context, id + "F31", { "sketchPlane" : qUnion([Q0])});
            skLineSegment(sketch, "E54.bottom", {"start": v(154.4, 8.83) * mm, "end": v(174.72, 8.83) * mm});
            skLineSegment(sketch, "E54.top", {"start": v(154.4, 6.3) * mm, "end": v(174.72, 6.3) * mm});
            skLineSegment(sketch, "E54.left", {"start": v(154.4, 8.83) * mm, "end": v(154.4, 6.3) * mm});
            skLineSegment(sketch, "E54.right", {"start": v(174.72, 8.83) * mm, "end": v(174.72, 6.3) * mm});
            skPoint(sketch, "E54.middle", {"position": v(164.56, 7.56) * mm});
            skPoint(sketch, "E54.middle.positionSnap0", {"position": v(177.26, 7.56) * mm});
            skPoint(sketch, "E54.middle.positionSnap1", {"position": v(164.56, 11.37) * mm});
            skPoint(sketch, "E54.centerSnap0", {"position": v(177.26, 7.56) * mm});
            skPoint(sketch, "E54.centerSnap1", {"position": v(164.56, 11.37) * mm});
            skSolve(sketch);
        }
        {
            var Q0;
            Q0=makeQuery(id+"F31.imprint","IMPRINT",FACE,{"disambiguationData":[TD([[makeQuery(id+"F31.imprint","IMPRINT",EDGE,{"derivedFrom":sQuery(id+"F31.wireOp",EDGE,"E54.bottom")}),-1.0]])]});
            extrude(context, id + "F32", {"entities" : qUnion([Q0]), "operationType" : NewBodyOperationType.REMOVE, "endBound" : BoundingType.THROUGH_ALL, "oppositeDirection" : true, "depth" : 25.4 * mm});
        }
        {
            var Q0;
            Q0=makeQuery(id+"F30.opExtrude","CAP_EDGE",EDGE,{"disambiguationData":[OSD([sQuery(id+"F29.wireOp",EDGE,"E50")])],"isStart":false});
            var Q1;
            Q1=makeQuery(id+"F30.opExtrude","SWEPT_EDGE",EDGE,{"disambiguationData":[OSD([sQuery(id+"F2.wireOp",EDGE,"E10"),sQuery(id+"F2.wireOp",EDGE,"E19"),sQuery(id+"F2.wireOp",EDGE,"E22"),sQuery(id+"F29.wireOp",EDGE,"E50")])]});
            var Q2;
            Q2=makeQuery(id+"F30.opExtrude","SWEPT_EDGE",EDGE,{"disambiguationData":[OSD([sQuery(id+"F29.wireOp",EDGE,"E50"),sQuery(id+"F29.wireOp",EDGE,"E53")])]});
            var Q3;
            Q3=makeQuery(id+"F30.opExtrude","CAP_EDGE",EDGE,{"disambiguationData":[OSD([sQuery(id+"F29.wireOp",EDGE,"E53")])],"isStart":false});
            var Q4;
            Q4=makeQuery(id+"F30.opExtrude","CAP_EDGE",EDGE,{"disambiguationData":[OSD([sQuery(id+"F2.wireOp",EDGE,"E10"),sQuery(id+"F2.wireOp",EDGE,"E19"),sQuery(id+"F2.wireOp",EDGE,"E22")])],"isStart":false});
            var Q5;
            Q5=makeQuery(id+"F30.opExtrude","CAP_EDGE",EDGE,{"disambiguationData":[OSD([sQuery(id+"F29.wireOp",EDGE,"E52")])],"isStart":false});
            var Q6;
            Q6=makeQuery(id+"F30.opExtrude","SWEPT_EDGE",EDGE,{"disambiguationData":[OSD([sQuery(id+"F2.wireOp",EDGE,"E10"),sQuery(id+"F2.wireOp",EDGE,"E19"),sQuery(id+"F2.wireOp",EDGE,"E22"),sQuery(id+"F29.wireOp",EDGE,"E52")])]});
            fillet(context, id + "F33", {"entities" : qUnion([Q0, Q1, Q2, Q3, Q4, Q5, Q6]), "radius" : 2.54 * mm, "tangentPropagation" : true, "allowEdgeOverflow" : false});
        }
        {
            var Q0;
            Q0=makeQuery(id+"F30.opExtrude","SWEPT_EDGE",EDGE,{"disambiguationData":[OSD([sQuery(id+"F29.wireOp",EDGE,"E52"),sQuery(id+"F29.wireOp",EDGE,"E53")])]});
            fillet(context, id + "F34", {"entities" : qUnion([Q0]), "radius" : 2.54 * mm, "tangentPropagation" : true, "allowEdgeOverflow" : false});
        }
        {
            var Q0;
            Q0=qCreatedBy(makeId("Front.planeOp"),FACE);
            var sketch = newSketch(context, id + "F35", { "sketchPlane" : qUnion([Q0])});
            skLineSegment(sketch, "E55", {"start": v(40.16, -20.02) * mm, "end": v(40.16, -30.18) * mm});
            skLineSegment(sketch, "E56", {"start": v(42.7, -17.48) * mm, "end": v(45.24, -17.48) * mm});
            skLineSegment(sketch, "E57", {"start": v(47.78, -20.02) * mm, "end": v(47.78, -27.64) * mm});
            skLineSegment(sketch, "E58", {"start": v(40.16, -35.26) * mm, "end": v(40.16, -30.18) * mm});
            skLineSegment(sketch, "E59", {"start": v(42.7, -37.8) * mm, "end": v(47.78, -37.8) * mm});
            skLineSegment(sketch, "E60", {"start": v(83.34, -37.8) * mm, "end": v(47.78, -37.8) * mm});
            skLineSegment(sketch, "E61", {"start": v(85.88, -35.26) * mm, "end": v(85.88, -32.72) * mm});
            skLineSegment(sketch, "E62", {"start": v(83.34, -30.18) * mm, "end": v(50.32, -30.18) * mm});
            skPoint(sketch, "E63.visualSharp", {"position": v(40.16, -37.8) * mm});
            skArc(sketch, "E63.filletArc", {"start": v(40.5, -36.53) * mm, "mid": v(41.43, -37.46) * mm, "end": v(42.7, -37.8) * mm});
            skPoint(sketch, "E64.visualSharp", {"position": v(85.88, -37.8) * mm});
            skArc(sketch, "E64.filletArc", {"start": v(83.34, -37.8) * mm, "mid": v(85.13, -37.06) * mm, "end": v(85.88, -35.26) * mm});
            skPoint(sketch, "E65.visualSharp", {"position": v(85.88, -30.18) * mm});
            skArc(sketch, "E65.filletArc", {"start": v(85.88, -32.72) * mm, "mid": v(85.13, -30.92) * mm, "end": v(83.34, -30.18) * mm});
            skPoint(sketch, "E66.visualSharp", {"position": v(47.78, -30.18) * mm});
            skArc(sketch, "E66.filletArc", {"start": v(47.78, -27.64) * mm, "mid": v(48.52, -29.44) * mm, "end": v(50.32, -30.18) * mm});
            skPoint(sketch, "E67.visualSharp", {"position": v(40.16, -17.48) * mm});
            skArc(sketch, "E67.filletArc", {"start": v(42.7, -17.48) * mm, "mid": v(40.9, -18.22) * mm, "end": v(40.16, -20.02) * mm});
            skPoint(sketch, "E68.visualSharp", {"position": v(47.78, -17.48) * mm});
            skArc(sketch, "E68.filletArc", {"start": v(47.78, -20.02) * mm, "mid": v(47.03, -18.22) * mm, "end": v(45.24, -17.48) * mm});
            skLineSegment(sketch, "E69", {"start": v(38.3, -35.26) * mm, "end": v(33.8, -35.26) * mm});
            skArc(sketch, "E70", {"start": v(32.93, -33.06) * mm, "mid": v(37.57, -27.1) * mm, "end": v(40.16, -20.02) * mm});
            skPoint(sketch, "E71.visualSharp", {"position": v(40.16, -35.26) * mm});
            skArc(sketch, "E71.filletArc", {"start": v(40.5, -36.53) * mm, "mid": v(39.57, -35.6) * mm, "end": v(38.3, -35.26) * mm});
            skPoint(sketch, "E72.visualSharp", {"position": v(30.23, -35.26) * mm});
            skArc(sketch, "E72.filletArc", {"start": v(32.93, -33.06) * mm, "mid": v(32.62, -34.46) * mm, "end": v(33.8, -35.26) * mm});
            skSolve(sketch);
        }
        {
            var Q0;
            Q0=makeQuery(id+"F35.imprint","IMPRINT",FACE,{"disambiguationData":[TD([[makeQuery(id+"F35.imprint","IMPRINT",EDGE,{"derivedFrom":sQuery(id+"F35.wireOp",EDGE,"E56")}),-1.0]])]});
            extrude(context, id + "F36", {"entities" : qUnion([Q0]), "depth" : 38.1 * mm, "symmetric" : true});
        }
        {
            var Q0;
            Q0=qCreatedBy(makeId("Front.planeOp"),FACE);
            var sketch = newSketch(context, id + "F37", { "sketchPlane" : qUnion([Q0])});
            skLineSegment(sketch, "E73.bottom", {"start": v(59.86, -15.6) * mm, "end": v(64.86, -15.6) * mm});
            skLineSegment(sketch, "E73.top", {"start": v(59.86, -25.6) * mm, "end": v(64.86, -25.6) * mm});
            skLineSegment(sketch, "E73.left", {"start": v(59.86, -15.6) * mm, "end": v(59.86, -25.6) * mm});
            skLineSegment(sketch, "E73.right", {"start": v(64.86, -15.6) * mm, "end": v(64.86, -25.6) * mm});
            skSolve(sketch);
        }
        {
            var Q0;
            Q0=makeQuery(id+"F37.imprint","IMPRINT",FACE,{"disambiguationData":[TD([[makeQuery(id+"F37.imprint","IMPRINT",EDGE,{"derivedFrom":sQuery(id+"F37.wireOp",EDGE,"E73.bottom")}),-1.0]])]});
            extrude(context, id + "F38", {"entities" : qUnion([Q0]), "depth" : 38 * mm, "symmetric" : true});
        }
    });
